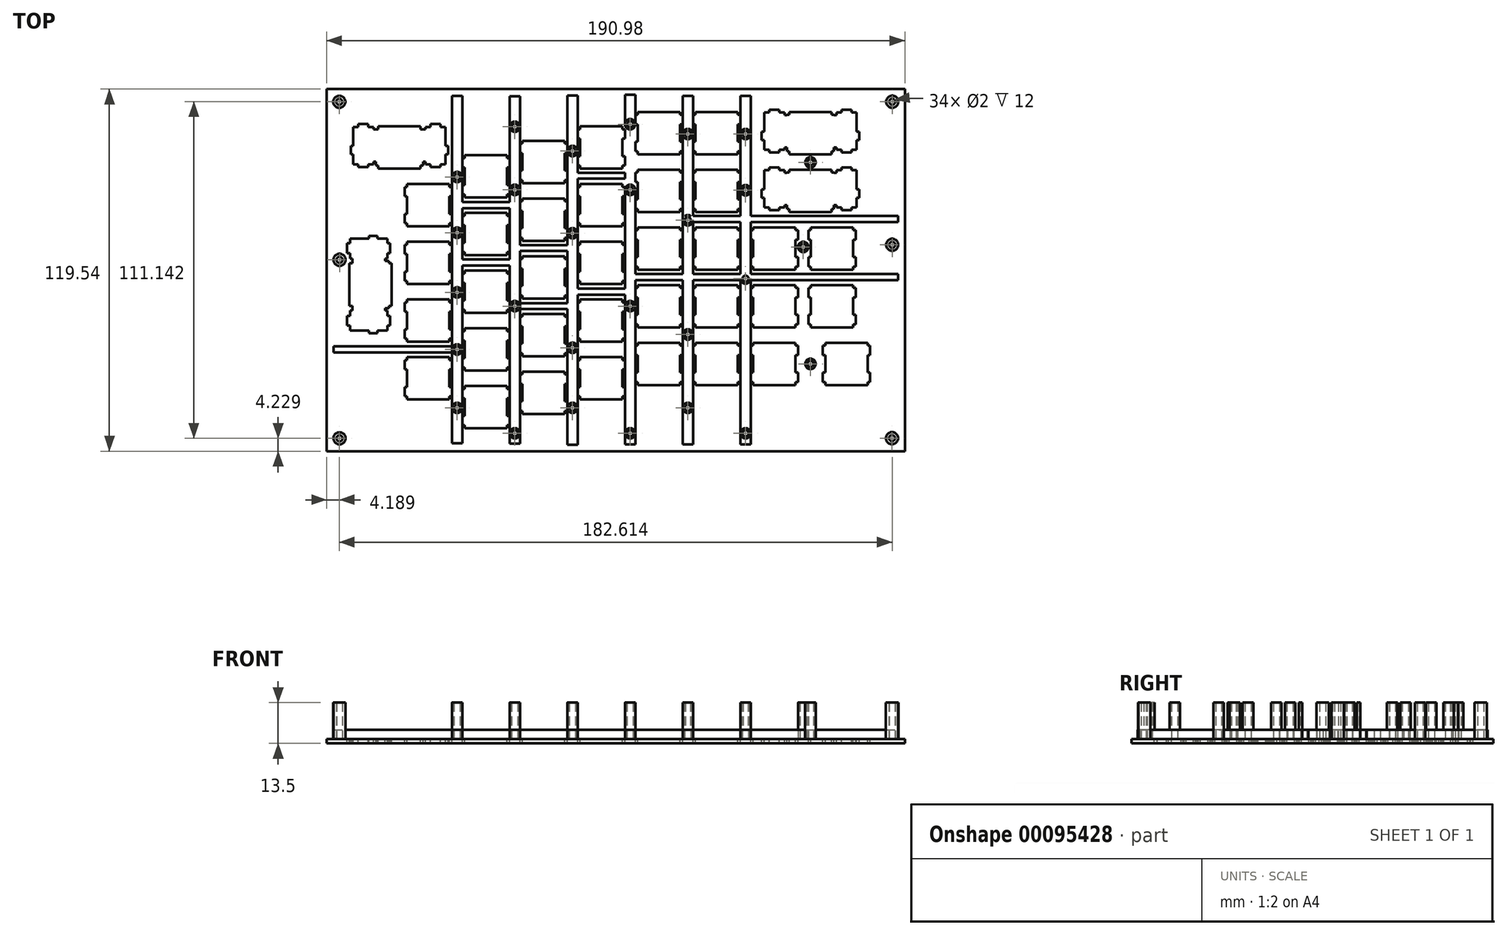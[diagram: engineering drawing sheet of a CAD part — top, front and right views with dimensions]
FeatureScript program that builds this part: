
annotation { "Feature Type Name" : "Feature", "Feature Type Description" : "" }
export const myFeature = defineFeature(function(context is Context, id is Id, definition is map)
    precondition{}
    {
        {
            var Q0;
            Q0=qCreatedBy(makeId("Top.planeOp"),FACE);
            var sketch = newSketch(context, id + "F0", { "sketchPlane" : qUnion([Q0])});
            skLineSegment(sketch, "E0", {"start": v(-95.49, 59.77) * mm, "end": v(95.49, 59.77) * mm});
            skLineSegment(sketch, "E1", {"start": v(95.49, 59.77) * mm, "end": v(95.49, -59.77) * mm});
            skLineSegment(sketch, "E2", {"start": v(95.49, -59.77) * mm, "end": v(-95.49, -59.77) * mm});
            skLineSegment(sketch, "E3", {"start": v(-95.49, -59.77) * mm, "end": v(-95.49, 59.77) * mm});
            skLineSegment(sketch, "E4", {"start": v(-74.96, -2.24) * mm, "end": v(-74.96, -3.04) * mm});
            skLineSegment(sketch, "E5", {"start": v(-74.96, -3.04) * mm, "end": v(-76.23, -3.04) * mm});
            skLineSegment(sketch, "E6", {"start": v(-76.23, -3.04) * mm, "end": v(-76.23, -3.81) * mm});
            skLineSegment(sketch, "E7", {"start": v(-76.23, -3.81) * mm, "end": v(-75.43, -3.81) * mm});
            skLineSegment(sketch, "E8", {"start": v(-75.43, -3.81) * mm, "end": v(-75.43, -5.54) * mm});
            skLineSegment(sketch, "E9", {"start": v(-75.43, -5.54) * mm, "end": v(-74.51, -5.54) * mm});
            skLineSegment(sketch, "E10", {"start": v(-74.51, -5.54) * mm, "end": v(-74.51, -8.84) * mm});
            skLineSegment(sketch, "E11", {"start": v(-74.51, -8.84) * mm, "end": v(-75.43, -8.84) * mm});
            skLineSegment(sketch, "E12", {"start": v(-75.43, -8.84) * mm, "end": v(-75.43, -10.46) * mm});
            skLineSegment(sketch, "E13", {"start": v(-75.43, -10.46) * mm, "end": v(-78.66, -10.46) * mm});
            skLineSegment(sketch, "E14", {"start": v(-78.66, -10.46) * mm, "end": v(-78.66, -11.34) * mm});
            skLineSegment(sketch, "E15", {"start": v(-78.66, -11.34) * mm, "end": v(-81.46, -11.34) * mm});
            skLineSegment(sketch, "E16", {"start": v(-81.46, -11.34) * mm, "end": v(-81.46, -10.46) * mm});
            skLineSegment(sketch, "E17", {"start": v(-81.46, -10.46) * mm, "end": v(-87.73, -10.46) * mm});
            skLineSegment(sketch, "E18", {"start": v(-87.73, -10.46) * mm, "end": v(-87.73, -8.84) * mm});
            skLineSegment(sketch, "E19", {"start": v(-87.73, -8.84) * mm, "end": v(-88.71, -8.84) * mm});
            skLineSegment(sketch, "E20", {"start": v(-88.71, -8.84) * mm, "end": v(-88.71, -5.54) * mm});
            skLineSegment(sketch, "E21", {"start": v(-88.71, -5.54) * mm, "end": v(-87.73, -5.54) * mm});
            skLineSegment(sketch, "E22", {"start": v(-87.73, -5.54) * mm, "end": v(-87.73, -3.81) * mm});
            skLineSegment(sketch, "E23", {"start": v(-87.73, -3.81) * mm, "end": v(-86.93, -3.81) * mm});
            skLineSegment(sketch, "E24", {"start": v(-86.93, -3.81) * mm, "end": v(-86.93, -3.04) * mm});
            skLineSegment(sketch, "E25", {"start": v(-86.93, -3.04) * mm, "end": v(-86.96, -3.04) * mm});
            skLineSegment(sketch, "E26", {"start": v(-86.96, -3.04) * mm, "end": v(-86.96, -2.24) * mm});
            skLineSegment(sketch, "E27", {"start": v(-86.96, -2.24) * mm, "end": v(-87.96, -2.24) * mm});
            skLineSegment(sketch, "E28", {"start": v(-87.96, -2.24) * mm, "end": v(-87.96, 11.76) * mm});
            skLineSegment(sketch, "E29", {"start": v(-87.96, 11.76) * mm, "end": v(-86.96, 11.76) * mm});
            skLineSegment(sketch, "E30", {"start": v(-86.96, 11.76) * mm, "end": v(-86.96, 12.56) * mm});
            skLineSegment(sketch, "E31", {"start": v(-86.96, 12.56) * mm, "end": v(-86.93, 12.56) * mm});
            skLineSegment(sketch, "E32", {"start": v(-86.93, 12.56) * mm, "end": v(-86.93, 13.34) * mm});
            skLineSegment(sketch, "E33", {"start": v(-86.93, 13.34) * mm, "end": v(-87.73, 13.34) * mm});
            skLineSegment(sketch, "E34", {"start": v(-87.73, 13.34) * mm, "end": v(-87.73, 15.06) * mm});
            skLineSegment(sketch, "E35", {"start": v(-87.73, 15.06) * mm, "end": v(-88.71, 15.06) * mm});
            skLineSegment(sketch, "E36", {"start": v(-88.71, 15.06) * mm, "end": v(-88.71, 18.36) * mm});
            skLineSegment(sketch, "E37", {"start": v(-88.71, 18.36) * mm, "end": v(-87.73, 18.36) * mm});
            skLineSegment(sketch, "E38", {"start": v(-87.73, 18.36) * mm, "end": v(-87.73, 19.99) * mm});
            skLineSegment(sketch, "E39", {"start": v(-87.73, 19.99) * mm, "end": v(-81.46, 19.99) * mm});
            skLineSegment(sketch, "E40", {"start": v(-81.46, 19.99) * mm, "end": v(-81.46, 20.86) * mm});
            skLineSegment(sketch, "E41", {"start": v(-81.46, 20.86) * mm, "end": v(-78.66, 20.86) * mm});
            skLineSegment(sketch, "E42", {"start": v(-78.66, 20.86) * mm, "end": v(-78.66, 19.99) * mm});
            skLineSegment(sketch, "E43", {"start": v(-78.66, 19.99) * mm, "end": v(-75.43, 19.99) * mm});
            skLineSegment(sketch, "E44", {"start": v(-75.43, 19.99) * mm, "end": v(-75.43, 18.36) * mm});
            skLineSegment(sketch, "E45", {"start": v(-75.43, 18.36) * mm, "end": v(-74.51, 18.36) * mm});
            skLineSegment(sketch, "E46", {"start": v(-74.51, 18.36) * mm, "end": v(-74.51, 15.06) * mm});
            skLineSegment(sketch, "E47", {"start": v(-74.51, 15.06) * mm, "end": v(-75.43, 15.06) * mm});
            skLineSegment(sketch, "E48", {"start": v(-75.43, 15.06) * mm, "end": v(-75.43, 13.34) * mm});
            skLineSegment(sketch, "E49", {"start": v(-75.43, 13.34) * mm, "end": v(-76.23, 13.34) * mm});
            skLineSegment(sketch, "E50", {"start": v(-76.23, 13.34) * mm, "end": v(-76.23, 12.56) * mm});
            skLineSegment(sketch, "E51", {"start": v(-76.23, 12.56) * mm, "end": v(-74.96, 12.56) * mm});
            skLineSegment(sketch, "E52", {"start": v(-74.96, 12.56) * mm, "end": v(-74.96, 11.76) * mm});
            skLineSegment(sketch, "E53", {"start": v(-74.96, 11.76) * mm, "end": v(-73.96, 11.76) * mm});
            skLineSegment(sketch, "E54", {"start": v(-73.96, 11.76) * mm, "end": v(-73.96, -2.24) * mm});
            skLineSegment(sketch, "E55", {"start": v(-73.96, -2.24) * mm, "end": v(-74.96, -2.24) * mm});
            skLineSegment(sketch, "E56", {"start": v(-56.21, -40.98) * mm, "end": v(-56.21, -47.25) * mm});
            skLineSegment(sketch, "E57", {"start": v(-56.21, -47.25) * mm, "end": v(-57.84, -47.25) * mm});
            skLineSegment(sketch, "E58", {"start": v(-57.84, -47.25) * mm, "end": v(-57.84, -48.23) * mm});
            skLineSegment(sketch, "E59", {"start": v(-57.84, -48.23) * mm, "end": v(-61.14, -48.23) * mm});
            skLineSegment(sketch, "E60", {"start": v(-61.14, -48.23) * mm, "end": v(-61.14, -47.25) * mm});
            skLineSegment(sketch, "E61", {"start": v(-61.14, -47.25) * mm, "end": v(-62.86, -47.25) * mm});
            skLineSegment(sketch, "E62", {"start": v(-62.86, -47.25) * mm, "end": v(-62.86, -46.45) * mm});
            skLineSegment(sketch, "E63", {"start": v(-62.86, -46.45) * mm, "end": v(-63.64, -46.45) * mm});
            skLineSegment(sketch, "E64", {"start": v(-63.64, -46.45) * mm, "end": v(-63.64, -46.48) * mm});
            skLineSegment(sketch, "E65", {"start": v(-63.64, -46.48) * mm, "end": v(-64.44, -46.48) * mm});
            skLineSegment(sketch, "E66", {"start": v(-64.44, -46.48) * mm, "end": v(-64.44, -47.48) * mm});
            skLineSegment(sketch, "E67", {"start": v(-64.44, -47.48) * mm, "end": v(-78.44, -47.48) * mm});
            skLineSegment(sketch, "E68", {"start": v(-78.44, -47.48) * mm, "end": v(-78.44, -46.48) * mm});
            skLineSegment(sketch, "E69", {"start": v(-78.44, -46.48) * mm, "end": v(-79.24, -46.48) * mm});
            skLineSegment(sketch, "E70", {"start": v(-79.24, -46.48) * mm, "end": v(-79.24, -46.45) * mm});
            skLineSegment(sketch, "E71", {"start": v(-79.24, -46.45) * mm, "end": v(-80.01, -46.45) * mm});
            skLineSegment(sketch, "E72", {"start": v(-80.01, -46.45) * mm, "end": v(-80.01, -47.25) * mm});
            skLineSegment(sketch, "E73", {"start": v(-80.01, -47.25) * mm, "end": v(-81.74, -47.25) * mm});
            skLineSegment(sketch, "E74", {"start": v(-81.74, -47.25) * mm, "end": v(-81.74, -48.23) * mm});
            skLineSegment(sketch, "E75", {"start": v(-81.74, -48.23) * mm, "end": v(-85.04, -48.23) * mm});
            skLineSegment(sketch, "E76", {"start": v(-85.04, -48.23) * mm, "end": v(-85.04, -47.25) * mm});
            skLineSegment(sketch, "E77", {"start": v(-85.04, -47.25) * mm, "end": v(-86.66, -47.25) * mm});
            skLineSegment(sketch, "E78", {"start": v(-86.66, -47.25) * mm, "end": v(-86.66, -40.98) * mm});
            skLineSegment(sketch, "E79", {"start": v(-86.66, -40.98) * mm, "end": v(-87.54, -40.98) * mm});
            skLineSegment(sketch, "E80", {"start": v(-87.54, -40.98) * mm, "end": v(-87.54, -38.18) * mm});
            skLineSegment(sketch, "E81", {"start": v(-87.54, -38.18) * mm, "end": v(-86.66, -38.18) * mm});
            skLineSegment(sketch, "E82", {"start": v(-86.66, -38.18) * mm, "end": v(-86.66, -34.95) * mm});
            skLineSegment(sketch, "E83", {"start": v(-86.66, -34.95) * mm, "end": v(-85.04, -34.95) * mm});
            skLineSegment(sketch, "E84", {"start": v(-85.04, -34.95) * mm, "end": v(-85.04, -34.03) * mm});
            skLineSegment(sketch, "E85", {"start": v(-85.04, -34.03) * mm, "end": v(-81.74, -34.03) * mm});
            skLineSegment(sketch, "E86", {"start": v(-81.74, -34.03) * mm, "end": v(-81.74, -34.95) * mm});
            skLineSegment(sketch, "E87", {"start": v(-81.74, -34.95) * mm, "end": v(-80.01, -34.95) * mm});
            skLineSegment(sketch, "E88", {"start": v(-80.01, -34.95) * mm, "end": v(-80.01, -35.75) * mm});
            skLineSegment(sketch, "E89", {"start": v(-80.01, -35.75) * mm, "end": v(-79.24, -35.75) * mm});
            skLineSegment(sketch, "E90", {"start": v(-79.24, -35.75) * mm, "end": v(-79.24, -34.48) * mm});
            skLineSegment(sketch, "E91", {"start": v(-79.24, -34.48) * mm, "end": v(-78.44, -34.48) * mm});
            skLineSegment(sketch, "E92", {"start": v(-78.44, -34.48) * mm, "end": v(-78.44, -33.48) * mm});
            skLineSegment(sketch, "E93", {"start": v(-78.44, -33.48) * mm, "end": v(-64.44, -33.48) * mm});
            skLineSegment(sketch, "E94", {"start": v(-64.44, -33.48) * mm, "end": v(-64.44, -34.48) * mm});
            skLineSegment(sketch, "E95", {"start": v(-64.44, -34.48) * mm, "end": v(-63.64, -34.48) * mm});
            skLineSegment(sketch, "E96", {"start": v(-63.64, -34.48) * mm, "end": v(-63.64, -35.75) * mm});
            skLineSegment(sketch, "E97", {"start": v(-63.64, -35.75) * mm, "end": v(-62.86, -35.75) * mm});
            skLineSegment(sketch, "E98", {"start": v(-62.86, -35.75) * mm, "end": v(-62.86, -34.95) * mm});
            skLineSegment(sketch, "E99", {"start": v(-62.86, -34.95) * mm, "end": v(-61.14, -34.95) * mm});
            skLineSegment(sketch, "E100", {"start": v(-61.14, -34.95) * mm, "end": v(-61.14, -34.03) * mm});
            skLineSegment(sketch, "E101", {"start": v(-61.14, -34.03) * mm, "end": v(-57.84, -34.03) * mm});
            skLineSegment(sketch, "E102", {"start": v(-57.84, -34.03) * mm, "end": v(-57.84, -34.95) * mm});
            skLineSegment(sketch, "E103", {"start": v(-57.84, -34.95) * mm, "end": v(-56.21, -34.95) * mm});
            skLineSegment(sketch, "E104", {"start": v(-56.21, -34.95) * mm, "end": v(-56.21, -38.18) * mm});
            skLineSegment(sketch, "E105", {"start": v(-56.21, -38.18) * mm, "end": v(-55.34, -38.18) * mm});
            skLineSegment(sketch, "E106", {"start": v(-55.34, -38.18) * mm, "end": v(-55.34, -40.98) * mm});
            skLineSegment(sketch, "E107", {"start": v(-55.34, -40.98) * mm, "end": v(-56.21, -40.98) * mm});
            skLineSegment(sketch, "E108", {"start": v(-54.91, 29.72) * mm, "end": v(-54.91, 28.72) * mm});
            skLineSegment(sketch, "E109", {"start": v(-54.91, 28.72) * mm, "end": v(-68.91, 28.72) * mm});
            skLineSegment(sketch, "E110", {"start": v(-68.91, 28.72) * mm, "end": v(-68.91, 29.72) * mm});
            skLineSegment(sketch, "E111", {"start": v(-68.91, 29.72) * mm, "end": v(-69.71, 29.72) * mm});
            skLineSegment(sketch, "E112", {"start": v(-69.71, 29.72) * mm, "end": v(-69.71, 32.82) * mm});
            skLineSegment(sketch, "E113", {"start": v(-69.71, 32.82) * mm, "end": v(-68.91, 32.82) * mm});
            skLineSegment(sketch, "E114", {"start": v(-68.91, 32.82) * mm, "end": v(-68.91, 38.62) * mm});
            skLineSegment(sketch, "E115", {"start": v(-68.91, 38.62) * mm, "end": v(-69.71, 38.62) * mm});
            skLineSegment(sketch, "E116", {"start": v(-69.71, 38.62) * mm, "end": v(-69.71, 41.72) * mm});
            skLineSegment(sketch, "E117", {"start": v(-69.71, 41.72) * mm, "end": v(-68.91, 41.72) * mm});
            skLineSegment(sketch, "E118", {"start": v(-68.91, 41.72) * mm, "end": v(-68.91, 42.72) * mm});
            skLineSegment(sketch, "E119", {"start": v(-68.91, 42.72) * mm, "end": v(-54.91, 42.72) * mm});
            skLineSegment(sketch, "E120", {"start": v(-54.91, 42.72) * mm, "end": v(-54.91, 41.72) * mm});
            skLineSegment(sketch, "E121", {"start": v(-54.91, 41.72) * mm, "end": v(-54.11, 41.72) * mm});
            skLineSegment(sketch, "E122", {"start": v(-54.11, 41.72) * mm, "end": v(-54.11, 38.62) * mm});
            skLineSegment(sketch, "E123", {"start": v(-54.11, 38.62) * mm, "end": v(-54.91, 38.62) * mm});
            skLineSegment(sketch, "E124", {"start": v(-54.91, 38.62) * mm, "end": v(-54.91, 32.82) * mm});
            skLineSegment(sketch, "E125", {"start": v(-54.91, 32.82) * mm, "end": v(-54.11, 32.82) * mm});
            skLineSegment(sketch, "E126", {"start": v(-54.11, 32.82) * mm, "end": v(-54.11, 29.72) * mm});
            skLineSegment(sketch, "E127", {"start": v(-54.11, 29.72) * mm, "end": v(-54.91, 29.72) * mm});
            skLineSegment(sketch, "E128", {"start": v(-54.91, 10.67) * mm, "end": v(-54.91, 9.67) * mm});
            skLineSegment(sketch, "E129", {"start": v(-54.91, 9.67) * mm, "end": v(-68.91, 9.67) * mm});
            skLineSegment(sketch, "E130", {"start": v(-68.91, 9.67) * mm, "end": v(-68.91, 10.67) * mm});
            skLineSegment(sketch, "E131", {"start": v(-68.91, 10.67) * mm, "end": v(-69.71, 10.67) * mm});
            skLineSegment(sketch, "E132", {"start": v(-69.71, 10.67) * mm, "end": v(-69.71, 13.77) * mm});
            skLineSegment(sketch, "E133", {"start": v(-69.71, 13.77) * mm, "end": v(-68.91, 13.77) * mm});
            skLineSegment(sketch, "E134", {"start": v(-68.91, 13.77) * mm, "end": v(-68.91, 19.57) * mm});
            skLineSegment(sketch, "E135", {"start": v(-68.91, 19.57) * mm, "end": v(-69.71, 19.57) * mm});
            skLineSegment(sketch, "E136", {"start": v(-69.71, 19.57) * mm, "end": v(-69.71, 22.67) * mm});
            skLineSegment(sketch, "E137", {"start": v(-69.71, 22.67) * mm, "end": v(-68.91, 22.67) * mm});
            skLineSegment(sketch, "E138", {"start": v(-68.91, 22.67) * mm, "end": v(-68.91, 23.67) * mm});
            skLineSegment(sketch, "E139", {"start": v(-68.91, 23.67) * mm, "end": v(-54.91, 23.67) * mm});
            skLineSegment(sketch, "E140", {"start": v(-54.91, 23.67) * mm, "end": v(-54.91, 22.67) * mm});
            skLineSegment(sketch, "E141", {"start": v(-54.91, 22.67) * mm, "end": v(-54.11, 22.67) * mm});
            skLineSegment(sketch, "E142", {"start": v(-54.11, 22.67) * mm, "end": v(-54.11, 19.57) * mm});
            skLineSegment(sketch, "E143", {"start": v(-54.11, 19.57) * mm, "end": v(-54.91, 19.57) * mm});
            skLineSegment(sketch, "E144", {"start": v(-54.91, 19.57) * mm, "end": v(-54.91, 13.77) * mm});
            skLineSegment(sketch, "E145", {"start": v(-54.91, 13.77) * mm, "end": v(-54.11, 13.77) * mm});
            skLineSegment(sketch, "E146", {"start": v(-54.11, 13.77) * mm, "end": v(-54.11, 10.67) * mm});
            skLineSegment(sketch, "E147", {"start": v(-54.11, 10.67) * mm, "end": v(-54.91, 10.67) * mm});
            skLineSegment(sketch, "E148", {"start": v(-54.91, -8.38) * mm, "end": v(-54.91, -9.38) * mm});
            skLineSegment(sketch, "E149", {"start": v(-54.91, -9.38) * mm, "end": v(-68.91, -9.38) * mm});
            skLineSegment(sketch, "E150", {"start": v(-68.91, -9.38) * mm, "end": v(-68.91, -8.38) * mm});
            skLineSegment(sketch, "E151", {"start": v(-68.91, -8.38) * mm, "end": v(-69.71, -8.38) * mm});
            skLineSegment(sketch, "E152", {"start": v(-69.71, -8.38) * mm, "end": v(-69.71, -5.28) * mm});
            skLineSegment(sketch, "E153", {"start": v(-69.71, -5.28) * mm, "end": v(-68.91, -5.28) * mm});
            skLineSegment(sketch, "E154", {"start": v(-68.91, -5.28) * mm, "end": v(-68.91, 0.52) * mm});
            skLineSegment(sketch, "E155", {"start": v(-68.91, 0.52) * mm, "end": v(-69.71, 0.52) * mm});
            skLineSegment(sketch, "E156", {"start": v(-69.71, 0.52) * mm, "end": v(-69.71, 3.62) * mm});
            skLineSegment(sketch, "E157", {"start": v(-69.71, 3.62) * mm, "end": v(-68.91, 3.62) * mm});
            skLineSegment(sketch, "E158", {"start": v(-68.91, 3.62) * mm, "end": v(-68.91, 4.62) * mm});
            skLineSegment(sketch, "E159", {"start": v(-68.91, 4.62) * mm, "end": v(-54.91, 4.62) * mm});
            skLineSegment(sketch, "E160", {"start": v(-54.91, 4.62) * mm, "end": v(-54.91, 3.62) * mm});
            skLineSegment(sketch, "E161", {"start": v(-54.91, 3.62) * mm, "end": v(-54.11, 3.62) * mm});
            skLineSegment(sketch, "E162", {"start": v(-54.11, 3.62) * mm, "end": v(-54.11, 0.52) * mm});
            skLineSegment(sketch, "E163", {"start": v(-54.11, 0.52) * mm, "end": v(-54.91, 0.52) * mm});
            skLineSegment(sketch, "E164", {"start": v(-54.91, 0.52) * mm, "end": v(-54.91, -5.28) * mm});
            skLineSegment(sketch, "E165", {"start": v(-54.91, -5.28) * mm, "end": v(-54.11, -5.28) * mm});
            skLineSegment(sketch, "E166", {"start": v(-54.11, -5.28) * mm, "end": v(-54.11, -8.38) * mm});
            skLineSegment(sketch, "E167", {"start": v(-54.11, -8.38) * mm, "end": v(-54.91, -8.38) * mm});
            skLineSegment(sketch, "E168", {"start": v(-54.91, -27.43) * mm, "end": v(-54.91, -28.43) * mm});
            skLineSegment(sketch, "E169", {"start": v(-54.91, -28.43) * mm, "end": v(-68.91, -28.43) * mm});
            skLineSegment(sketch, "E170", {"start": v(-68.91, -28.43) * mm, "end": v(-68.91, -27.43) * mm});
            skLineSegment(sketch, "E171", {"start": v(-68.91, -27.43) * mm, "end": v(-69.71, -27.43) * mm});
            skLineSegment(sketch, "E172", {"start": v(-69.71, -27.43) * mm, "end": v(-69.71, -24.33) * mm});
            skLineSegment(sketch, "E173", {"start": v(-69.71, -24.33) * mm, "end": v(-68.91, -24.33) * mm});
            skLineSegment(sketch, "E174", {"start": v(-68.91, -24.33) * mm, "end": v(-68.91, -18.53) * mm});
            skLineSegment(sketch, "E175", {"start": v(-68.91, -18.53) * mm, "end": v(-69.71, -18.53) * mm});
            skLineSegment(sketch, "E176", {"start": v(-69.71, -18.53) * mm, "end": v(-69.71, -15.43) * mm});
            skLineSegment(sketch, "E177", {"start": v(-69.71, -15.43) * mm, "end": v(-68.91, -15.43) * mm});
            skLineSegment(sketch, "E178", {"start": v(-68.91, -15.43) * mm, "end": v(-68.91, -14.43) * mm});
            skLineSegment(sketch, "E179", {"start": v(-68.91, -14.43) * mm, "end": v(-54.91, -14.43) * mm});
            skLineSegment(sketch, "E180", {"start": v(-54.91, -14.43) * mm, "end": v(-54.91, -15.43) * mm});
            skLineSegment(sketch, "E181", {"start": v(-54.91, -15.43) * mm, "end": v(-54.11, -15.43) * mm});
            skLineSegment(sketch, "E182", {"start": v(-54.11, -15.43) * mm, "end": v(-54.11, -18.53) * mm});
            skLineSegment(sketch, "E183", {"start": v(-54.11, -18.53) * mm, "end": v(-54.91, -18.53) * mm});
            skLineSegment(sketch, "E184", {"start": v(-54.91, -18.53) * mm, "end": v(-54.91, -24.33) * mm});
            skLineSegment(sketch, "E185", {"start": v(-54.91, -24.33) * mm, "end": v(-54.11, -24.33) * mm});
            skLineSegment(sketch, "E186", {"start": v(-54.11, -24.33) * mm, "end": v(-54.11, -27.43) * mm});
            skLineSegment(sketch, "E187", {"start": v(-54.11, -27.43) * mm, "end": v(-54.91, -27.43) * mm});
            skLineSegment(sketch, "E188", {"start": v(-35.86, 39.24) * mm, "end": v(-35.86, 38.24) * mm});
            skLineSegment(sketch, "E189", {"start": v(-35.86, 38.24) * mm, "end": v(-49.86, 38.24) * mm});
            skLineSegment(sketch, "E190", {"start": v(-49.86, 38.24) * mm, "end": v(-49.86, 39.24) * mm});
            skLineSegment(sketch, "E191", {"start": v(-49.86, 39.24) * mm, "end": v(-50.66, 39.24) * mm});
            skLineSegment(sketch, "E192", {"start": v(-50.66, 39.24) * mm, "end": v(-50.66, 42.34) * mm});
            skLineSegment(sketch, "E193", {"start": v(-50.66, 42.34) * mm, "end": v(-49.86, 42.34) * mm});
            skLineSegment(sketch, "E194", {"start": v(-49.86, 42.34) * mm, "end": v(-49.86, 48.14) * mm});
            skLineSegment(sketch, "E195", {"start": v(-49.86, 48.14) * mm, "end": v(-50.66, 48.14) * mm});
            skLineSegment(sketch, "E196", {"start": v(-50.66, 48.14) * mm, "end": v(-50.66, 51.24) * mm});
            skLineSegment(sketch, "E197", {"start": v(-50.66, 51.24) * mm, "end": v(-49.86, 51.24) * mm});
            skLineSegment(sketch, "E198", {"start": v(-49.86, 51.24) * mm, "end": v(-49.86, 52.24) * mm});
            skLineSegment(sketch, "E199", {"start": v(-49.86, 52.24) * mm, "end": v(-35.86, 52.24) * mm});
            skLineSegment(sketch, "E200", {"start": v(-35.86, 52.24) * mm, "end": v(-35.86, 51.24) * mm});
            skLineSegment(sketch, "E201", {"start": v(-35.86, 51.24) * mm, "end": v(-35.06, 51.24) * mm});
            skLineSegment(sketch, "E202", {"start": v(-35.06, 51.24) * mm, "end": v(-35.06, 48.14) * mm});
            skLineSegment(sketch, "E203", {"start": v(-35.06, 48.14) * mm, "end": v(-35.86, 48.14) * mm});
            skLineSegment(sketch, "E204", {"start": v(-35.86, 48.14) * mm, "end": v(-35.86, 42.34) * mm});
            skLineSegment(sketch, "E205", {"start": v(-35.86, 42.34) * mm, "end": v(-35.06, 42.34) * mm});
            skLineSegment(sketch, "E206", {"start": v(-35.06, 42.34) * mm, "end": v(-35.06, 39.24) * mm});
            skLineSegment(sketch, "E207", {"start": v(-35.06, 39.24) * mm, "end": v(-35.86, 39.24) * mm});
            skLineSegment(sketch, "E208", {"start": v(-35.86, 20.2) * mm, "end": v(-35.86, 19.2) * mm});
            skLineSegment(sketch, "E209", {"start": v(-35.86, 19.2) * mm, "end": v(-49.86, 19.2) * mm});
            skLineSegment(sketch, "E210", {"start": v(-49.86, 19.2) * mm, "end": v(-49.86, 20.2) * mm});
            skLineSegment(sketch, "E211", {"start": v(-49.86, 20.2) * mm, "end": v(-50.66, 20.2) * mm});
            skLineSegment(sketch, "E212", {"start": v(-50.66, 20.2) * mm, "end": v(-50.66, 23.3) * mm});
            skLineSegment(sketch, "E213", {"start": v(-50.66, 23.3) * mm, "end": v(-49.86, 23.3) * mm});
            skLineSegment(sketch, "E214", {"start": v(-49.86, 23.3) * mm, "end": v(-49.86, 29.1) * mm});
            skLineSegment(sketch, "E215", {"start": v(-49.86, 29.1) * mm, "end": v(-50.66, 29.1) * mm});
            skLineSegment(sketch, "E216", {"start": v(-50.66, 29.1) * mm, "end": v(-50.66, 32.2) * mm});
            skLineSegment(sketch, "E217", {"start": v(-50.66, 32.2) * mm, "end": v(-49.86, 32.2) * mm});
            skLineSegment(sketch, "E218", {"start": v(-49.86, 32.2) * mm, "end": v(-49.86, 33.2) * mm});
            skLineSegment(sketch, "E219", {"start": v(-49.86, 33.2) * mm, "end": v(-35.86, 33.2) * mm});
            skLineSegment(sketch, "E220", {"start": v(-35.86, 33.2) * mm, "end": v(-35.86, 32.2) * mm});
            skLineSegment(sketch, "E221", {"start": v(-35.86, 32.2) * mm, "end": v(-35.06, 32.2) * mm});
            skLineSegment(sketch, "E222", {"start": v(-35.06, 32.2) * mm, "end": v(-35.06, 29.1) * mm});
            skLineSegment(sketch, "E223", {"start": v(-35.06, 29.1) * mm, "end": v(-35.86, 29.1) * mm});
            skLineSegment(sketch, "E224", {"start": v(-35.86, 29.1) * mm, "end": v(-35.86, 23.3) * mm});
            skLineSegment(sketch, "E225", {"start": v(-35.86, 23.3) * mm, "end": v(-35.06, 23.3) * mm});
            skLineSegment(sketch, "E226", {"start": v(-35.06, 23.3) * mm, "end": v(-35.06, 20.2) * mm});
            skLineSegment(sketch, "E227", {"start": v(-35.06, 20.2) * mm, "end": v(-35.86, 20.2) * mm});
            skLineSegment(sketch, "E228", {"start": v(-35.86, 1.14) * mm, "end": v(-35.86, 0.14) * mm});
            skLineSegment(sketch, "E229", {"start": v(-35.86, 0.14) * mm, "end": v(-49.86, 0.14) * mm});
            skLineSegment(sketch, "E230", {"start": v(-49.86, 0.14) * mm, "end": v(-49.86, 1.14) * mm});
            skLineSegment(sketch, "E231", {"start": v(-49.86, 1.14) * mm, "end": v(-50.66, 1.14) * mm});
            skLineSegment(sketch, "E232", {"start": v(-50.66, 1.14) * mm, "end": v(-50.66, 4.24) * mm});
            skLineSegment(sketch, "E233", {"start": v(-50.66, 4.24) * mm, "end": v(-49.86, 4.24) * mm});
            skLineSegment(sketch, "E234", {"start": v(-49.86, 4.24) * mm, "end": v(-49.86, 10.04) * mm});
            skLineSegment(sketch, "E235", {"start": v(-49.86, 10.04) * mm, "end": v(-50.66, 10.04) * mm});
            skLineSegment(sketch, "E236", {"start": v(-50.66, 10.04) * mm, "end": v(-50.66, 13.14) * mm});
            skLineSegment(sketch, "E237", {"start": v(-50.66, 13.14) * mm, "end": v(-49.86, 13.14) * mm});
            skLineSegment(sketch, "E238", {"start": v(-49.86, 13.14) * mm, "end": v(-49.86, 14.14) * mm});
            skLineSegment(sketch, "E239", {"start": v(-49.86, 14.14) * mm, "end": v(-35.86, 14.14) * mm});
            skLineSegment(sketch, "E240", {"start": v(-35.86, 14.14) * mm, "end": v(-35.86, 13.14) * mm});
            skLineSegment(sketch, "E241", {"start": v(-35.86, 13.14) * mm, "end": v(-35.06, 13.14) * mm});
            skLineSegment(sketch, "E242", {"start": v(-35.06, 13.14) * mm, "end": v(-35.06, 10.04) * mm});
            skLineSegment(sketch, "E243", {"start": v(-35.06, 10.04) * mm, "end": v(-35.86, 10.04) * mm});
            skLineSegment(sketch, "E244", {"start": v(-35.86, 10.04) * mm, "end": v(-35.86, 4.24) * mm});
            skLineSegment(sketch, "E245", {"start": v(-35.86, 4.24) * mm, "end": v(-35.06, 4.24) * mm});
            skLineSegment(sketch, "E246", {"start": v(-35.06, 4.24) * mm, "end": v(-35.06, 1.14) * mm});
            skLineSegment(sketch, "E247", {"start": v(-35.06, 1.14) * mm, "end": v(-35.86, 1.14) * mm});
            skLineSegment(sketch, "E248", {"start": v(-35.86, -17.9) * mm, "end": v(-35.86, -18.9) * mm});
            skLineSegment(sketch, "E249", {"start": v(-35.86, -18.9) * mm, "end": v(-49.86, -18.9) * mm});
            skLineSegment(sketch, "E250", {"start": v(-49.86, -18.9) * mm, "end": v(-49.86, -17.9) * mm});
            skLineSegment(sketch, "E251", {"start": v(-49.86, -17.9) * mm, "end": v(-50.66, -17.9) * mm});
            skLineSegment(sketch, "E252", {"start": v(-50.66, -17.9) * mm, "end": v(-50.66, -14.8) * mm});
            skLineSegment(sketch, "E253", {"start": v(-50.66, -14.8) * mm, "end": v(-49.86, -14.8) * mm});
            skLineSegment(sketch, "E254", {"start": v(-49.86, -14.8) * mm, "end": v(-49.86, -9) * mm});
            skLineSegment(sketch, "E255", {"start": v(-49.86, -9) * mm, "end": v(-50.66, -9) * mm});
            skLineSegment(sketch, "E256", {"start": v(-50.66, -9) * mm, "end": v(-50.66, -5.9) * mm});
            skLineSegment(sketch, "E257", {"start": v(-50.66, -5.9) * mm, "end": v(-49.86, -5.9) * mm});
            skLineSegment(sketch, "E258", {"start": v(-49.86, -5.9) * mm, "end": v(-49.86, -4.9) * mm});
            skLineSegment(sketch, "E259", {"start": v(-49.86, -4.9) * mm, "end": v(-35.86, -4.9) * mm});
            skLineSegment(sketch, "E260", {"start": v(-35.86, -4.9) * mm, "end": v(-35.86, -5.9) * mm});
            skLineSegment(sketch, "E261", {"start": v(-35.86, -5.9) * mm, "end": v(-35.06, -5.9) * mm});
            skLineSegment(sketch, "E262", {"start": v(-35.06, -5.9) * mm, "end": v(-35.06, -9) * mm});
            skLineSegment(sketch, "E263", {"start": v(-35.06, -9) * mm, "end": v(-35.86, -9) * mm});
            skLineSegment(sketch, "E264", {"start": v(-35.86, -9) * mm, "end": v(-35.86, -14.8) * mm});
            skLineSegment(sketch, "E265", {"start": v(-35.86, -14.8) * mm, "end": v(-35.06, -14.8) * mm});
            skLineSegment(sketch, "E266", {"start": v(-35.06, -14.8) * mm, "end": v(-35.06, -17.9) * mm});
            skLineSegment(sketch, "E267", {"start": v(-35.06, -17.9) * mm, "end": v(-35.86, -17.9) * mm});
            skLineSegment(sketch, "E268", {"start": v(-35.86, -36.96) * mm, "end": v(-35.86, -37.96) * mm});
            skLineSegment(sketch, "E269", {"start": v(-35.86, -37.96) * mm, "end": v(-49.86, -37.96) * mm});
            skLineSegment(sketch, "E270", {"start": v(-49.86, -37.96) * mm, "end": v(-49.86, -36.96) * mm});
            skLineSegment(sketch, "E271", {"start": v(-49.86, -36.96) * mm, "end": v(-50.66, -36.96) * mm});
            skLineSegment(sketch, "E272", {"start": v(-50.66, -36.96) * mm, "end": v(-50.66, -33.86) * mm});
            skLineSegment(sketch, "E273", {"start": v(-50.66, -33.86) * mm, "end": v(-49.86, -33.86) * mm});
            skLineSegment(sketch, "E274", {"start": v(-49.86, -33.86) * mm, "end": v(-49.86, -28.06) * mm});
            skLineSegment(sketch, "E275", {"start": v(-49.86, -28.06) * mm, "end": v(-50.66, -28.06) * mm});
            skLineSegment(sketch, "E276", {"start": v(-50.66, -28.06) * mm, "end": v(-50.66, -24.96) * mm});
            skLineSegment(sketch, "E277", {"start": v(-50.66, -24.96) * mm, "end": v(-49.86, -24.96) * mm});
            skLineSegment(sketch, "E278", {"start": v(-49.86, -24.96) * mm, "end": v(-49.86, -23.96) * mm});
            skLineSegment(sketch, "E279", {"start": v(-49.86, -23.96) * mm, "end": v(-35.86, -23.96) * mm});
            skLineSegment(sketch, "E280", {"start": v(-35.86, -23.96) * mm, "end": v(-35.86, -24.96) * mm});
            skLineSegment(sketch, "E281", {"start": v(-35.86, -24.96) * mm, "end": v(-35.06, -24.96) * mm});
            skLineSegment(sketch, "E282", {"start": v(-35.06, -24.96) * mm, "end": v(-35.06, -28.06) * mm});
            skLineSegment(sketch, "E283", {"start": v(-35.06, -28.06) * mm, "end": v(-35.86, -28.06) * mm});
            skLineSegment(sketch, "E284", {"start": v(-35.86, -28.06) * mm, "end": v(-35.86, -33.86) * mm});
            skLineSegment(sketch, "E285", {"start": v(-35.86, -33.86) * mm, "end": v(-35.06, -33.86) * mm});
            skLineSegment(sketch, "E286", {"start": v(-35.06, -33.86) * mm, "end": v(-35.06, -36.96) * mm});
            skLineSegment(sketch, "E287", {"start": v(-35.06, -36.96) * mm, "end": v(-35.86, -36.96) * mm});
            skLineSegment(sketch, "E288", {"start": v(-16.81, 34.48) * mm, "end": v(-16.81, 33.48) * mm});
            skLineSegment(sketch, "E289", {"start": v(-16.81, 33.48) * mm, "end": v(-30.81, 33.48) * mm});
            skLineSegment(sketch, "E290", {"start": v(-30.81, 33.48) * mm, "end": v(-30.81, 34.48) * mm});
            skLineSegment(sketch, "E291", {"start": v(-30.81, 34.48) * mm, "end": v(-31.61, 34.48) * mm});
            skLineSegment(sketch, "E292", {"start": v(-31.61, 34.48) * mm, "end": v(-31.61, 37.58) * mm});
            skLineSegment(sketch, "E293", {"start": v(-31.61, 37.58) * mm, "end": v(-30.81, 37.58) * mm});
            skLineSegment(sketch, "E294", {"start": v(-30.81, 37.58) * mm, "end": v(-30.81, 43.38) * mm});
            skLineSegment(sketch, "E295", {"start": v(-30.81, 43.38) * mm, "end": v(-31.61, 43.38) * mm});
            skLineSegment(sketch, "E296", {"start": v(-31.61, 43.38) * mm, "end": v(-31.61, 46.48) * mm});
            skLineSegment(sketch, "E297", {"start": v(-31.61, 46.48) * mm, "end": v(-30.81, 46.48) * mm});
            skLineSegment(sketch, "E298", {"start": v(-30.81, 46.48) * mm, "end": v(-30.81, 47.48) * mm});
            skLineSegment(sketch, "E299", {"start": v(-30.81, 47.48) * mm, "end": v(-16.81, 47.48) * mm});
            skLineSegment(sketch, "E300", {"start": v(-16.81, 47.48) * mm, "end": v(-16.81, 46.48) * mm});
            skLineSegment(sketch, "E301", {"start": v(-16.81, 46.48) * mm, "end": v(-16.01, 46.48) * mm});
            skLineSegment(sketch, "E302", {"start": v(-16.01, 46.48) * mm, "end": v(-16.01, 43.38) * mm});
            skLineSegment(sketch, "E303", {"start": v(-16.01, 43.38) * mm, "end": v(-16.81, 43.38) * mm});
            skLineSegment(sketch, "E304", {"start": v(-16.81, 43.38) * mm, "end": v(-16.81, 37.58) * mm});
            skLineSegment(sketch, "E305", {"start": v(-16.81, 37.58) * mm, "end": v(-16.01, 37.58) * mm});
            skLineSegment(sketch, "E306", {"start": v(-16.01, 37.58) * mm, "end": v(-16.01, 34.48) * mm});
            skLineSegment(sketch, "E307", {"start": v(-16.01, 34.48) * mm, "end": v(-16.81, 34.48) * mm});
            skLineSegment(sketch, "E308", {"start": v(-16.81, 15.43) * mm, "end": v(-16.81, 14.43) * mm});
            skLineSegment(sketch, "E309", {"start": v(-16.81, 14.43) * mm, "end": v(-30.81, 14.43) * mm});
            skLineSegment(sketch, "E310", {"start": v(-30.81, 14.43) * mm, "end": v(-30.81, 15.43) * mm});
            skLineSegment(sketch, "E311", {"start": v(-30.81, 15.43) * mm, "end": v(-31.61, 15.43) * mm});
            skLineSegment(sketch, "E312", {"start": v(-31.61, 15.43) * mm, "end": v(-31.61, 18.53) * mm});
            skLineSegment(sketch, "E313", {"start": v(-31.61, 18.53) * mm, "end": v(-30.81, 18.53) * mm});
            skLineSegment(sketch, "E314", {"start": v(-30.81, 18.53) * mm, "end": v(-30.81, 24.33) * mm});
            skLineSegment(sketch, "E315", {"start": v(-30.81, 24.33) * mm, "end": v(-31.61, 24.33) * mm});
            skLineSegment(sketch, "E316", {"start": v(-31.61, 24.33) * mm, "end": v(-31.61, 27.43) * mm});
            skLineSegment(sketch, "E317", {"start": v(-31.61, 27.43) * mm, "end": v(-30.81, 27.43) * mm});
            skLineSegment(sketch, "E318", {"start": v(-30.81, 27.43) * mm, "end": v(-30.81, 28.43) * mm});
            skLineSegment(sketch, "E319", {"start": v(-30.81, 28.43) * mm, "end": v(-16.81, 28.43) * mm});
            skLineSegment(sketch, "E320", {"start": v(-16.81, 28.43) * mm, "end": v(-16.81, 27.43) * mm});
            skLineSegment(sketch, "E321", {"start": v(-16.81, 27.43) * mm, "end": v(-16.01, 27.43) * mm});
            skLineSegment(sketch, "E322", {"start": v(-16.01, 27.43) * mm, "end": v(-16.01, 24.33) * mm});
            skLineSegment(sketch, "E323", {"start": v(-16.01, 24.33) * mm, "end": v(-16.81, 24.33) * mm});
            skLineSegment(sketch, "E324", {"start": v(-16.81, 24.33) * mm, "end": v(-16.81, 18.53) * mm});
            skLineSegment(sketch, "E325", {"start": v(-16.81, 18.53) * mm, "end": v(-16.01, 18.53) * mm});
            skLineSegment(sketch, "E326", {"start": v(-16.01, 18.53) * mm, "end": v(-16.01, 15.43) * mm});
            skLineSegment(sketch, "E327", {"start": v(-16.01, 15.43) * mm, "end": v(-16.81, 15.43) * mm});
            skLineSegment(sketch, "E328", {"start": v(-16.81, -3.62) * mm, "end": v(-16.81, -4.62) * mm});
            skLineSegment(sketch, "E329", {"start": v(-16.81, -4.62) * mm, "end": v(-30.81, -4.62) * mm});
            skLineSegment(sketch, "E330", {"start": v(-30.81, -4.62) * mm, "end": v(-30.81, -3.62) * mm});
            skLineSegment(sketch, "E331", {"start": v(-30.81, -3.62) * mm, "end": v(-31.61, -3.62) * mm});
            skLineSegment(sketch, "E332", {"start": v(-31.61, -3.62) * mm, "end": v(-31.61, -0.52) * mm});
            skLineSegment(sketch, "E333", {"start": v(-31.61, -0.52) * mm, "end": v(-30.81, -0.52) * mm});
            skLineSegment(sketch, "E334", {"start": v(-30.81, -0.52) * mm, "end": v(-30.81, 5.28) * mm});
            skLineSegment(sketch, "E335", {"start": v(-30.81, 5.28) * mm, "end": v(-31.61, 5.28) * mm});
            skLineSegment(sketch, "E336", {"start": v(-31.61, 5.28) * mm, "end": v(-31.61, 8.38) * mm});
            skLineSegment(sketch, "E337", {"start": v(-31.61, 8.38) * mm, "end": v(-30.81, 8.38) * mm});
            skLineSegment(sketch, "E338", {"start": v(-30.81, 8.38) * mm, "end": v(-30.81, 9.38) * mm});
            skLineSegment(sketch, "E339", {"start": v(-30.81, 9.38) * mm, "end": v(-16.81, 9.38) * mm});
            skLineSegment(sketch, "E340", {"start": v(-16.81, 9.38) * mm, "end": v(-16.81, 8.38) * mm});
            skLineSegment(sketch, "E341", {"start": v(-16.81, 8.38) * mm, "end": v(-16.01, 8.38) * mm});
            skLineSegment(sketch, "E342", {"start": v(-16.01, 8.38) * mm, "end": v(-16.01, 5.28) * mm});
            skLineSegment(sketch, "E343", {"start": v(-16.01, 5.28) * mm, "end": v(-16.81, 5.28) * mm});
            skLineSegment(sketch, "E344", {"start": v(-16.81, 5.28) * mm, "end": v(-16.81, -0.52) * mm});
            skLineSegment(sketch, "E345", {"start": v(-16.81, -0.52) * mm, "end": v(-16.01, -0.52) * mm});
            skLineSegment(sketch, "E346", {"start": v(-16.01, -0.52) * mm, "end": v(-16.01, -3.62) * mm});
            skLineSegment(sketch, "E347", {"start": v(-16.01, -3.62) * mm, "end": v(-16.81, -3.62) * mm});
            skLineSegment(sketch, "E348", {"start": v(-16.81, -22.67) * mm, "end": v(-16.81, -23.67) * mm});
            skLineSegment(sketch, "E349", {"start": v(-16.81, -23.67) * mm, "end": v(-30.81, -23.67) * mm});
            skLineSegment(sketch, "E350", {"start": v(-30.81, -23.67) * mm, "end": v(-30.81, -22.67) * mm});
            skLineSegment(sketch, "E351", {"start": v(-30.81, -22.67) * mm, "end": v(-31.61, -22.67) * mm});
            skLineSegment(sketch, "E352", {"start": v(-31.61, -22.67) * mm, "end": v(-31.61, -19.57) * mm});
            skLineSegment(sketch, "E353", {"start": v(-31.61, -19.57) * mm, "end": v(-30.81, -19.57) * mm});
            skLineSegment(sketch, "E354", {"start": v(-30.81, -19.57) * mm, "end": v(-30.81, -13.77) * mm});
            skLineSegment(sketch, "E355", {"start": v(-30.81, -13.77) * mm, "end": v(-31.61, -13.77) * mm});
            skLineSegment(sketch, "E356", {"start": v(-31.61, -13.77) * mm, "end": v(-31.61, -10.67) * mm});
            skLineSegment(sketch, "E357", {"start": v(-31.61, -10.67) * mm, "end": v(-30.81, -10.67) * mm});
            skLineSegment(sketch, "E358", {"start": v(-30.81, -10.67) * mm, "end": v(-30.81, -9.67) * mm});
            skLineSegment(sketch, "E359", {"start": v(-30.81, -9.67) * mm, "end": v(-16.81, -9.67) * mm});
            skLineSegment(sketch, "E360", {"start": v(-16.81, -9.67) * mm, "end": v(-16.81, -10.67) * mm});
            skLineSegment(sketch, "E361", {"start": v(-16.81, -10.67) * mm, "end": v(-16.01, -10.67) * mm});
            skLineSegment(sketch, "E362", {"start": v(-16.01, -10.67) * mm, "end": v(-16.01, -13.77) * mm});
            skLineSegment(sketch, "E363", {"start": v(-16.01, -13.77) * mm, "end": v(-16.81, -13.77) * mm});
            skLineSegment(sketch, "E364", {"start": v(-16.81, -13.77) * mm, "end": v(-16.81, -19.57) * mm});
            skLineSegment(sketch, "E365", {"start": v(-16.81, -19.57) * mm, "end": v(-16.01, -19.57) * mm});
            skLineSegment(sketch, "E366", {"start": v(-16.01, -19.57) * mm, "end": v(-16.01, -22.67) * mm});
            skLineSegment(sketch, "E367", {"start": v(-16.01, -22.67) * mm, "end": v(-16.81, -22.67) * mm});
            skLineSegment(sketch, "E368", {"start": v(-16.81, -41.72) * mm, "end": v(-16.81, -42.72) * mm});
            skLineSegment(sketch, "E369", {"start": v(-16.81, -42.72) * mm, "end": v(-30.81, -42.72) * mm});
            skLineSegment(sketch, "E370", {"start": v(-30.81, -42.72) * mm, "end": v(-30.81, -41.72) * mm});
            skLineSegment(sketch, "E371", {"start": v(-30.81, -41.72) * mm, "end": v(-31.61, -41.72) * mm});
            skLineSegment(sketch, "E372", {"start": v(-31.61, -41.72) * mm, "end": v(-31.61, -38.62) * mm});
            skLineSegment(sketch, "E373", {"start": v(-31.61, -38.62) * mm, "end": v(-30.81, -38.62) * mm});
            skLineSegment(sketch, "E374", {"start": v(-30.81, -38.62) * mm, "end": v(-30.81, -32.82) * mm});
            skLineSegment(sketch, "E375", {"start": v(-30.81, -32.82) * mm, "end": v(-31.61, -32.82) * mm});
            skLineSegment(sketch, "E376", {"start": v(-31.61, -32.82) * mm, "end": v(-31.61, -29.72) * mm});
            skLineSegment(sketch, "E377", {"start": v(-31.61, -29.72) * mm, "end": v(-30.81, -29.72) * mm});
            skLineSegment(sketch, "E378", {"start": v(-30.81, -29.72) * mm, "end": v(-30.81, -28.72) * mm});
            skLineSegment(sketch, "E379", {"start": v(-30.81, -28.72) * mm, "end": v(-16.81, -28.72) * mm});
            skLineSegment(sketch, "E380", {"start": v(-16.81, -28.72) * mm, "end": v(-16.81, -29.72) * mm});
            skLineSegment(sketch, "E381", {"start": v(-16.81, -29.72) * mm, "end": v(-16.01, -29.72) * mm});
            skLineSegment(sketch, "E382", {"start": v(-16.01, -29.72) * mm, "end": v(-16.01, -32.82) * mm});
            skLineSegment(sketch, "E383", {"start": v(-16.01, -32.82) * mm, "end": v(-16.81, -32.82) * mm});
            skLineSegment(sketch, "E384", {"start": v(-16.81, -32.82) * mm, "end": v(-16.81, -38.62) * mm});
            skLineSegment(sketch, "E385", {"start": v(-16.81, -38.62) * mm, "end": v(-16.01, -38.62) * mm});
            skLineSegment(sketch, "E386", {"start": v(-16.01, -38.62) * mm, "end": v(-16.01, -41.72) * mm});
            skLineSegment(sketch, "E387", {"start": v(-16.01, -41.72) * mm, "end": v(-16.81, -41.72) * mm});
            skLineSegment(sketch, "E388", {"start": v(2.24, 29.72) * mm, "end": v(2.24, 28.72) * mm});
            skLineSegment(sketch, "E389", {"start": v(2.24, 28.72) * mm, "end": v(-11.76, 28.72) * mm});
            skLineSegment(sketch, "E390", {"start": v(-11.76, 28.72) * mm, "end": v(-11.76, 29.72) * mm});
            skLineSegment(sketch, "E391", {"start": v(-11.76, 29.72) * mm, "end": v(-12.56, 29.72) * mm});
            skLineSegment(sketch, "E392", {"start": v(-12.56, 29.72) * mm, "end": v(-12.56, 32.82) * mm});
            skLineSegment(sketch, "E393", {"start": v(-12.56, 32.82) * mm, "end": v(-11.76, 32.82) * mm});
            skLineSegment(sketch, "E394", {"start": v(-11.76, 32.82) * mm, "end": v(-11.76, 38.62) * mm});
            skLineSegment(sketch, "E395", {"start": v(-11.76, 38.62) * mm, "end": v(-12.56, 38.62) * mm});
            skLineSegment(sketch, "E396", {"start": v(-12.56, 38.62) * mm, "end": v(-12.56, 41.72) * mm});
            skLineSegment(sketch, "E397", {"start": v(-12.56, 41.72) * mm, "end": v(-11.76, 41.72) * mm});
            skLineSegment(sketch, "E398", {"start": v(-11.76, 41.72) * mm, "end": v(-11.76, 42.72) * mm});
            skLineSegment(sketch, "E399", {"start": v(-11.76, 42.72) * mm, "end": v(2.24, 42.72) * mm});
            skLineSegment(sketch, "E400", {"start": v(2.24, 42.72) * mm, "end": v(2.24, 41.72) * mm});
            skLineSegment(sketch, "E401", {"start": v(2.24, 41.72) * mm, "end": v(3.04, 41.72) * mm});
            skLineSegment(sketch, "E402", {"start": v(3.04, 41.72) * mm, "end": v(3.04, 38.62) * mm});
            skLineSegment(sketch, "E403", {"start": v(3.04, 38.62) * mm, "end": v(2.24, 38.62) * mm});
            skLineSegment(sketch, "E404", {"start": v(2.24, 38.62) * mm, "end": v(2.24, 32.82) * mm});
            skLineSegment(sketch, "E405", {"start": v(2.24, 32.82) * mm, "end": v(3.04, 32.82) * mm});
            skLineSegment(sketch, "E406", {"start": v(3.04, 32.82) * mm, "end": v(3.04, 29.72) * mm});
            skLineSegment(sketch, "E407", {"start": v(3.04, 29.72) * mm, "end": v(2.24, 29.72) * mm});
            skLineSegment(sketch, "E408", {"start": v(2.24, 10.67) * mm, "end": v(2.24, 9.67) * mm});
            skLineSegment(sketch, "E409", {"start": v(2.24, 9.67) * mm, "end": v(-11.76, 9.67) * mm});
            skLineSegment(sketch, "E410", {"start": v(-11.76, 9.67) * mm, "end": v(-11.76, 10.67) * mm});
            skLineSegment(sketch, "E411", {"start": v(-11.76, 10.67) * mm, "end": v(-12.56, 10.67) * mm});
            skLineSegment(sketch, "E412", {"start": v(-12.56, 10.67) * mm, "end": v(-12.56, 13.77) * mm});
            skLineSegment(sketch, "E413", {"start": v(-12.56, 13.77) * mm, "end": v(-11.76, 13.77) * mm});
            skLineSegment(sketch, "E414", {"start": v(-11.76, 13.77) * mm, "end": v(-11.76, 19.57) * mm});
            skLineSegment(sketch, "E415", {"start": v(-11.76, 19.57) * mm, "end": v(-12.56, 19.57) * mm});
            skLineSegment(sketch, "E416", {"start": v(-12.56, 19.57) * mm, "end": v(-12.56, 22.67) * mm});
            skLineSegment(sketch, "E417", {"start": v(-12.56, 22.67) * mm, "end": v(-11.76, 22.67) * mm});
            skLineSegment(sketch, "E418", {"start": v(-11.76, 22.67) * mm, "end": v(-11.76, 23.67) * mm});
            skLineSegment(sketch, "E419", {"start": v(-11.76, 23.67) * mm, "end": v(2.24, 23.67) * mm});
            skLineSegment(sketch, "E420", {"start": v(2.24, 23.67) * mm, "end": v(2.24, 22.67) * mm});
            skLineSegment(sketch, "E421", {"start": v(2.24, 22.67) * mm, "end": v(3.04, 22.67) * mm});
            skLineSegment(sketch, "E422", {"start": v(3.04, 22.67) * mm, "end": v(3.04, 19.57) * mm});
            skLineSegment(sketch, "E423", {"start": v(3.04, 19.57) * mm, "end": v(2.24, 19.57) * mm});
            skLineSegment(sketch, "E424", {"start": v(2.24, 19.57) * mm, "end": v(2.24, 13.77) * mm});
            skLineSegment(sketch, "E425", {"start": v(2.24, 13.77) * mm, "end": v(3.04, 13.77) * mm});
            skLineSegment(sketch, "E426", {"start": v(3.04, 13.77) * mm, "end": v(3.04, 10.67) * mm});
            skLineSegment(sketch, "E427", {"start": v(3.04, 10.67) * mm, "end": v(2.24, 10.67) * mm});
            skLineSegment(sketch, "E428", {"start": v(2.24, -8.38) * mm, "end": v(2.24, -9.38) * mm});
            skLineSegment(sketch, "E429", {"start": v(2.24, -9.38) * mm, "end": v(-11.76, -9.38) * mm});
            skLineSegment(sketch, "E430", {"start": v(-11.76, -9.38) * mm, "end": v(-11.76, -8.38) * mm});
            skLineSegment(sketch, "E431", {"start": v(-11.76, -8.38) * mm, "end": v(-12.56, -8.38) * mm});
            skLineSegment(sketch, "E432", {"start": v(-12.56, -8.38) * mm, "end": v(-12.56, -5.28) * mm});
            skLineSegment(sketch, "E433", {"start": v(-12.56, -5.28) * mm, "end": v(-11.76, -5.28) * mm});
            skLineSegment(sketch, "E434", {"start": v(-11.76, -5.28) * mm, "end": v(-11.76, 0.52) * mm});
            skLineSegment(sketch, "E435", {"start": v(-11.76, 0.52) * mm, "end": v(-12.56, 0.52) * mm});
            skLineSegment(sketch, "E436", {"start": v(-12.56, 0.52) * mm, "end": v(-12.56, 3.62) * mm});
            skLineSegment(sketch, "E437", {"start": v(-12.56, 3.62) * mm, "end": v(-11.76, 3.62) * mm});
            skLineSegment(sketch, "E438", {"start": v(-11.76, 3.62) * mm, "end": v(-11.76, 4.62) * mm});
            skLineSegment(sketch, "E439", {"start": v(-11.76, 4.62) * mm, "end": v(2.24, 4.62) * mm});
            skLineSegment(sketch, "E440", {"start": v(2.24, 4.62) * mm, "end": v(2.24, 3.62) * mm});
            skLineSegment(sketch, "E441", {"start": v(2.24, 3.62) * mm, "end": v(3.04, 3.62) * mm});
            skLineSegment(sketch, "E442", {"start": v(3.04, 3.62) * mm, "end": v(3.04, 0.52) * mm});
            skLineSegment(sketch, "E443", {"start": v(3.04, 0.52) * mm, "end": v(2.24, 0.52) * mm});
            skLineSegment(sketch, "E444", {"start": v(2.24, 0.52) * mm, "end": v(2.24, -5.28) * mm});
            skLineSegment(sketch, "E445", {"start": v(2.24, -5.28) * mm, "end": v(3.04, -5.28) * mm});
            skLineSegment(sketch, "E446", {"start": v(3.04, -5.28) * mm, "end": v(3.04, -8.38) * mm});
            skLineSegment(sketch, "E447", {"start": v(3.04, -8.38) * mm, "end": v(2.24, -8.38) * mm});
            skLineSegment(sketch, "E448", {"start": v(2.24, -27.43) * mm, "end": v(2.24, -28.43) * mm});
            skLineSegment(sketch, "E449", {"start": v(2.24, -28.43) * mm, "end": v(-11.76, -28.43) * mm});
            skLineSegment(sketch, "E450", {"start": v(-11.76, -28.43) * mm, "end": v(-11.76, -27.43) * mm});
            skLineSegment(sketch, "E451", {"start": v(-11.76, -27.43) * mm, "end": v(-12.56, -27.43) * mm});
            skLineSegment(sketch, "E452", {"start": v(-12.56, -27.43) * mm, "end": v(-12.56, -24.33) * mm});
            skLineSegment(sketch, "E453", {"start": v(-12.56, -24.33) * mm, "end": v(-11.76, -24.33) * mm});
            skLineSegment(sketch, "E454", {"start": v(-11.76, -24.33) * mm, "end": v(-11.76, -18.53) * mm});
            skLineSegment(sketch, "E455", {"start": v(-11.76, -18.53) * mm, "end": v(-12.56, -18.53) * mm});
            skLineSegment(sketch, "E456", {"start": v(-12.56, -18.53) * mm, "end": v(-12.56, -15.43) * mm});
            skLineSegment(sketch, "E457", {"start": v(-12.56, -15.43) * mm, "end": v(-11.76, -15.43) * mm});
            skLineSegment(sketch, "E458", {"start": v(-11.76, -15.43) * mm, "end": v(-11.76, -14.43) * mm});
            skLineSegment(sketch, "E459", {"start": v(-11.76, -14.43) * mm, "end": v(2.24, -14.43) * mm});
            skLineSegment(sketch, "E460", {"start": v(2.24, -14.43) * mm, "end": v(2.24, -15.43) * mm});
            skLineSegment(sketch, "E461", {"start": v(2.24, -15.43) * mm, "end": v(3.04, -15.43) * mm});
            skLineSegment(sketch, "E462", {"start": v(3.04, -15.43) * mm, "end": v(3.04, -18.53) * mm});
            skLineSegment(sketch, "E463", {"start": v(3.04, -18.53) * mm, "end": v(2.24, -18.53) * mm});
            skLineSegment(sketch, "E464", {"start": v(2.24, -18.53) * mm, "end": v(2.24, -24.33) * mm});
            skLineSegment(sketch, "E465", {"start": v(2.24, -24.33) * mm, "end": v(3.04, -24.33) * mm});
            skLineSegment(sketch, "E466", {"start": v(3.04, -24.33) * mm, "end": v(3.04, -27.43) * mm});
            skLineSegment(sketch, "E467", {"start": v(3.04, -27.43) * mm, "end": v(2.24, -27.43) * mm});
            skLineSegment(sketch, "E468", {"start": v(2.24, -46.48) * mm, "end": v(2.24, -47.48) * mm});
            skLineSegment(sketch, "E469", {"start": v(2.24, -47.48) * mm, "end": v(-11.76, -47.48) * mm});
            skLineSegment(sketch, "E470", {"start": v(-11.76, -47.48) * mm, "end": v(-11.76, -46.48) * mm});
            skLineSegment(sketch, "E471", {"start": v(-11.76, -46.48) * mm, "end": v(-12.56, -46.48) * mm});
            skLineSegment(sketch, "E472", {"start": v(-12.56, -46.48) * mm, "end": v(-12.56, -43.38) * mm});
            skLineSegment(sketch, "E473", {"start": v(-12.56, -43.38) * mm, "end": v(-11.76, -43.38) * mm});
            skLineSegment(sketch, "E474", {"start": v(-11.76, -43.38) * mm, "end": v(-11.76, -37.58) * mm});
            skLineSegment(sketch, "E475", {"start": v(-11.76, -37.58) * mm, "end": v(-12.56, -37.58) * mm});
            skLineSegment(sketch, "E476", {"start": v(-12.56, -37.58) * mm, "end": v(-12.56, -34.48) * mm});
            skLineSegment(sketch, "E477", {"start": v(-12.56, -34.48) * mm, "end": v(-11.76, -34.48) * mm});
            skLineSegment(sketch, "E478", {"start": v(-11.76, -34.48) * mm, "end": v(-11.76, -33.48) * mm});
            skLineSegment(sketch, "E479", {"start": v(-11.76, -33.48) * mm, "end": v(2.24, -33.48) * mm});
            skLineSegment(sketch, "E480", {"start": v(2.24, -33.48) * mm, "end": v(2.24, -34.48) * mm});
            skLineSegment(sketch, "E481", {"start": v(2.24, -34.48) * mm, "end": v(3.04, -34.48) * mm});
            skLineSegment(sketch, "E482", {"start": v(3.04, -34.48) * mm, "end": v(3.04, -37.58) * mm});
            skLineSegment(sketch, "E483", {"start": v(3.04, -37.58) * mm, "end": v(2.24, -37.58) * mm});
            skLineSegment(sketch, "E484", {"start": v(2.24, -37.58) * mm, "end": v(2.24, -43.38) * mm});
            skLineSegment(sketch, "E485", {"start": v(2.24, -43.38) * mm, "end": v(3.04, -43.38) * mm});
            skLineSegment(sketch, "E486", {"start": v(3.04, -43.38) * mm, "end": v(3.04, -46.48) * mm});
            skLineSegment(sketch, "E487", {"start": v(3.04, -46.48) * mm, "end": v(2.24, -46.48) * mm});
            skLineSegment(sketch, "E488", {"start": v(21.29, 24.96) * mm, "end": v(21.29, 23.96) * mm});
            skLineSegment(sketch, "E489", {"start": v(21.29, 23.96) * mm, "end": v(7.29, 23.96) * mm});
            skLineSegment(sketch, "E490", {"start": v(7.29, 23.96) * mm, "end": v(7.29, 24.96) * mm});
            skLineSegment(sketch, "E491", {"start": v(7.29, 24.96) * mm, "end": v(6.49, 24.96) * mm});
            skLineSegment(sketch, "E492", {"start": v(6.49, 24.96) * mm, "end": v(6.49, 28.06) * mm});
            skLineSegment(sketch, "E493", {"start": v(6.49, 28.06) * mm, "end": v(7.29, 28.06) * mm});
            skLineSegment(sketch, "E494", {"start": v(7.29, 28.06) * mm, "end": v(7.29, 33.86) * mm});
            skLineSegment(sketch, "E495", {"start": v(7.29, 33.86) * mm, "end": v(6.49, 33.86) * mm});
            skLineSegment(sketch, "E496", {"start": v(6.49, 33.86) * mm, "end": v(6.49, 36.96) * mm});
            skLineSegment(sketch, "E497", {"start": v(6.49, 36.96) * mm, "end": v(7.29, 36.96) * mm});
            skLineSegment(sketch, "E498", {"start": v(7.29, 36.96) * mm, "end": v(7.29, 37.96) * mm});
            skLineSegment(sketch, "E499", {"start": v(7.29, 37.96) * mm, "end": v(21.29, 37.96) * mm});
            skLineSegment(sketch, "E500", {"start": v(21.29, 37.96) * mm, "end": v(21.29, 36.96) * mm});
            skLineSegment(sketch, "E501", {"start": v(21.29, 36.96) * mm, "end": v(22.09, 36.96) * mm});
            skLineSegment(sketch, "E502", {"start": v(22.09, 36.96) * mm, "end": v(22.09, 33.86) * mm});
            skLineSegment(sketch, "E503", {"start": v(22.09, 33.86) * mm, "end": v(21.29, 33.86) * mm});
            skLineSegment(sketch, "E504", {"start": v(21.29, 33.86) * mm, "end": v(21.29, 28.06) * mm});
            skLineSegment(sketch, "E505", {"start": v(21.29, 28.06) * mm, "end": v(22.09, 28.06) * mm});
            skLineSegment(sketch, "E506", {"start": v(22.09, 28.06) * mm, "end": v(22.09, 24.96) * mm});
            skLineSegment(sketch, "E507", {"start": v(22.09, 24.96) * mm, "end": v(21.29, 24.96) * mm});
            skLineSegment(sketch, "E508", {"start": v(21.29, 5.9) * mm, "end": v(21.29, 4.9) * mm});
            skLineSegment(sketch, "E509", {"start": v(21.29, 4.9) * mm, "end": v(7.29, 4.9) * mm});
            skLineSegment(sketch, "E510", {"start": v(7.29, 4.9) * mm, "end": v(7.29, 5.9) * mm});
            skLineSegment(sketch, "E511", {"start": v(7.29, 5.9) * mm, "end": v(6.49, 5.9) * mm});
            skLineSegment(sketch, "E512", {"start": v(6.49, 5.9) * mm, "end": v(6.49, 9) * mm});
            skLineSegment(sketch, "E513", {"start": v(6.49, 9) * mm, "end": v(7.29, 9) * mm});
            skLineSegment(sketch, "E514", {"start": v(7.29, 9) * mm, "end": v(7.29, 14.8) * mm});
            skLineSegment(sketch, "E515", {"start": v(7.29, 14.8) * mm, "end": v(6.49, 14.8) * mm});
            skLineSegment(sketch, "E516", {"start": v(6.49, 14.8) * mm, "end": v(6.49, 17.9) * mm});
            skLineSegment(sketch, "E517", {"start": v(6.49, 17.9) * mm, "end": v(7.29, 17.9) * mm});
            skLineSegment(sketch, "E518", {"start": v(7.29, 17.9) * mm, "end": v(7.29, 18.9) * mm});
            skLineSegment(sketch, "E519", {"start": v(7.29, 18.9) * mm, "end": v(21.29, 18.9) * mm});
            skLineSegment(sketch, "E520", {"start": v(21.29, 18.9) * mm, "end": v(21.29, 17.9) * mm});
            skLineSegment(sketch, "E521", {"start": v(21.29, 17.9) * mm, "end": v(22.09, 17.9) * mm});
            skLineSegment(sketch, "E522", {"start": v(22.09, 17.9) * mm, "end": v(22.09, 14.8) * mm});
            skLineSegment(sketch, "E523", {"start": v(22.09, 14.8) * mm, "end": v(21.29, 14.8) * mm});
            skLineSegment(sketch, "E524", {"start": v(21.29, 14.8) * mm, "end": v(21.29, 9) * mm});
            skLineSegment(sketch, "E525", {"start": v(21.29, 9) * mm, "end": v(22.09, 9) * mm});
            skLineSegment(sketch, "E526", {"start": v(22.09, 9) * mm, "end": v(22.09, 5.9) * mm});
            skLineSegment(sketch, "E527", {"start": v(22.09, 5.9) * mm, "end": v(21.29, 5.9) * mm});
            skLineSegment(sketch, "E528", {"start": v(21.29, -13.14) * mm, "end": v(21.29, -14.14) * mm});
            skLineSegment(sketch, "E529", {"start": v(21.29, -14.14) * mm, "end": v(7.29, -14.14) * mm});
            skLineSegment(sketch, "E530", {"start": v(7.29, -14.14) * mm, "end": v(7.29, -13.14) * mm});
            skLineSegment(sketch, "E531", {"start": v(7.29, -13.14) * mm, "end": v(6.49, -13.14) * mm});
            skLineSegment(sketch, "E532", {"start": v(6.49, -13.14) * mm, "end": v(6.49, -10.04) * mm});
            skLineSegment(sketch, "E533", {"start": v(6.49, -10.04) * mm, "end": v(7.29, -10.04) * mm});
            skLineSegment(sketch, "E534", {"start": v(7.29, -10.04) * mm, "end": v(7.29, -4.24) * mm});
            skLineSegment(sketch, "E535", {"start": v(7.29, -4.24) * mm, "end": v(6.49, -4.24) * mm});
            skLineSegment(sketch, "E536", {"start": v(6.49, -4.24) * mm, "end": v(6.49, -1.14) * mm});
            skLineSegment(sketch, "E537", {"start": v(6.49, -1.14) * mm, "end": v(7.29, -1.14) * mm});
            skLineSegment(sketch, "E538", {"start": v(7.29, -1.14) * mm, "end": v(7.29, -0.14) * mm});
            skLineSegment(sketch, "E539", {"start": v(7.29, -0.14) * mm, "end": v(21.29, -0.14) * mm});
            skLineSegment(sketch, "E540", {"start": v(21.29, -0.14) * mm, "end": v(21.29, -1.14) * mm});
            skLineSegment(sketch, "E541", {"start": v(21.29, -1.14) * mm, "end": v(22.09, -1.14) * mm});
            skLineSegment(sketch, "E542", {"start": v(22.09, -1.14) * mm, "end": v(22.09, -4.24) * mm});
            skLineSegment(sketch, "E543", {"start": v(22.09, -4.24) * mm, "end": v(21.29, -4.24) * mm});
            skLineSegment(sketch, "E544", {"start": v(21.29, -4.24) * mm, "end": v(21.29, -10.04) * mm});
            skLineSegment(sketch, "E545", {"start": v(21.29, -10.04) * mm, "end": v(22.09, -10.04) * mm});
            skLineSegment(sketch, "E546", {"start": v(22.09, -10.04) * mm, "end": v(22.09, -13.14) * mm});
            skLineSegment(sketch, "E547", {"start": v(22.09, -13.14) * mm, "end": v(21.29, -13.14) * mm});
            skLineSegment(sketch, "E548", {"start": v(21.29, -32.2) * mm, "end": v(21.29, -33.2) * mm});
            skLineSegment(sketch, "E549", {"start": v(21.29, -33.2) * mm, "end": v(7.29, -33.2) * mm});
            skLineSegment(sketch, "E550", {"start": v(7.29, -33.2) * mm, "end": v(7.29, -32.2) * mm});
            skLineSegment(sketch, "E551", {"start": v(7.29, -32.2) * mm, "end": v(6.49, -32.2) * mm});
            skLineSegment(sketch, "E552", {"start": v(6.49, -32.2) * mm, "end": v(6.49, -29.1) * mm});
            skLineSegment(sketch, "E553", {"start": v(6.49, -29.1) * mm, "end": v(7.29, -29.1) * mm});
            skLineSegment(sketch, "E554", {"start": v(7.29, -29.1) * mm, "end": v(7.29, -23.3) * mm});
            skLineSegment(sketch, "E555", {"start": v(7.29, -23.3) * mm, "end": v(6.49, -23.3) * mm});
            skLineSegment(sketch, "E556", {"start": v(6.49, -23.3) * mm, "end": v(6.49, -20.2) * mm});
            skLineSegment(sketch, "E557", {"start": v(6.49, -20.2) * mm, "end": v(7.29, -20.2) * mm});
            skLineSegment(sketch, "E558", {"start": v(7.29, -20.2) * mm, "end": v(7.29, -19.2) * mm});
            skLineSegment(sketch, "E559", {"start": v(7.29, -19.2) * mm, "end": v(21.29, -19.2) * mm});
            skLineSegment(sketch, "E560", {"start": v(21.29, -19.2) * mm, "end": v(21.29, -20.2) * mm});
            skLineSegment(sketch, "E561", {"start": v(21.29, -20.2) * mm, "end": v(22.09, -20.2) * mm});
            skLineSegment(sketch, "E562", {"start": v(22.09, -20.2) * mm, "end": v(22.09, -23.3) * mm});
            skLineSegment(sketch, "E563", {"start": v(22.09, -23.3) * mm, "end": v(21.29, -23.3) * mm});
            skLineSegment(sketch, "E564", {"start": v(21.29, -23.3) * mm, "end": v(21.29, -29.1) * mm});
            skLineSegment(sketch, "E565", {"start": v(21.29, -29.1) * mm, "end": v(22.09, -29.1) * mm});
            skLineSegment(sketch, "E566", {"start": v(22.09, -29.1) * mm, "end": v(22.09, -32.2) * mm});
            skLineSegment(sketch, "E567", {"start": v(22.09, -32.2) * mm, "end": v(21.29, -32.2) * mm});
            skLineSegment(sketch, "E568", {"start": v(21.29, -51.24) * mm, "end": v(21.29, -52.24) * mm});
            skLineSegment(sketch, "E569", {"start": v(21.29, -52.24) * mm, "end": v(7.29, -52.24) * mm});
            skLineSegment(sketch, "E570", {"start": v(7.29, -52.24) * mm, "end": v(7.29, -51.24) * mm});
            skLineSegment(sketch, "E571", {"start": v(7.29, -51.24) * mm, "end": v(6.49, -51.24) * mm});
            skLineSegment(sketch, "E572", {"start": v(6.49, -51.24) * mm, "end": v(6.49, -48.14) * mm});
            skLineSegment(sketch, "E573", {"start": v(6.49, -48.14) * mm, "end": v(7.29, -48.14) * mm});
            skLineSegment(sketch, "E574", {"start": v(7.29, -48.14) * mm, "end": v(7.29, -42.34) * mm});
            skLineSegment(sketch, "E575", {"start": v(7.29, -42.34) * mm, "end": v(6.49, -42.34) * mm});
            skLineSegment(sketch, "E576", {"start": v(6.49, -42.34) * mm, "end": v(6.49, -39.24) * mm});
            skLineSegment(sketch, "E577", {"start": v(6.49, -39.24) * mm, "end": v(7.29, -39.24) * mm});
            skLineSegment(sketch, "E578", {"start": v(7.29, -39.24) * mm, "end": v(7.29, -38.24) * mm});
            skLineSegment(sketch, "E579", {"start": v(7.29, -38.24) * mm, "end": v(21.29, -38.24) * mm});
            skLineSegment(sketch, "E580", {"start": v(21.29, -38.24) * mm, "end": v(21.29, -39.24) * mm});
            skLineSegment(sketch, "E581", {"start": v(21.29, -39.24) * mm, "end": v(22.09, -39.24) * mm});
            skLineSegment(sketch, "E582", {"start": v(22.09, -39.24) * mm, "end": v(22.09, -42.34) * mm});
            skLineSegment(sketch, "E583", {"start": v(22.09, -42.34) * mm, "end": v(21.29, -42.34) * mm});
            skLineSegment(sketch, "E584", {"start": v(21.29, -42.34) * mm, "end": v(21.29, -48.14) * mm});
            skLineSegment(sketch, "E585", {"start": v(21.29, -48.14) * mm, "end": v(22.09, -48.14) * mm});
            skLineSegment(sketch, "E586", {"start": v(22.09, -48.14) * mm, "end": v(22.09, -51.24) * mm});
            skLineSegment(sketch, "E587", {"start": v(22.09, -51.24) * mm, "end": v(21.29, -51.24) * mm});
            skLineSegment(sketch, "E588", {"start": v(40.34, 24.96) * mm, "end": v(40.34, 23.96) * mm});
            skLineSegment(sketch, "E589", {"start": v(40.34, 23.96) * mm, "end": v(26.34, 23.96) * mm});
            skLineSegment(sketch, "E590", {"start": v(26.34, 23.96) * mm, "end": v(26.34, 24.96) * mm});
            skLineSegment(sketch, "E591", {"start": v(26.34, 24.96) * mm, "end": v(25.54, 24.96) * mm});
            skLineSegment(sketch, "E592", {"start": v(25.54, 24.96) * mm, "end": v(25.54, 28.06) * mm});
            skLineSegment(sketch, "E593", {"start": v(25.54, 28.06) * mm, "end": v(26.34, 28.06) * mm});
            skLineSegment(sketch, "E594", {"start": v(26.34, 28.06) * mm, "end": v(26.34, 33.86) * mm});
            skLineSegment(sketch, "E595", {"start": v(26.34, 33.86) * mm, "end": v(25.54, 33.86) * mm});
            skLineSegment(sketch, "E596", {"start": v(25.54, 33.86) * mm, "end": v(25.54, 36.96) * mm});
            skLineSegment(sketch, "E597", {"start": v(25.54, 36.96) * mm, "end": v(26.34, 36.96) * mm});
            skLineSegment(sketch, "E598", {"start": v(26.34, 36.96) * mm, "end": v(26.34, 37.96) * mm});
            skLineSegment(sketch, "E599", {"start": v(26.34, 37.96) * mm, "end": v(40.34, 37.96) * mm});
            skLineSegment(sketch, "E600", {"start": v(40.34, 37.96) * mm, "end": v(40.34, 36.96) * mm});
            skLineSegment(sketch, "E601", {"start": v(40.34, 36.96) * mm, "end": v(41.14, 36.96) * mm});
            skLineSegment(sketch, "E602", {"start": v(41.14, 36.96) * mm, "end": v(41.14, 33.86) * mm});
            skLineSegment(sketch, "E603", {"start": v(41.14, 33.86) * mm, "end": v(40.34, 33.86) * mm});
            skLineSegment(sketch, "E604", {"start": v(40.34, 33.86) * mm, "end": v(40.34, 28.06) * mm});
            skLineSegment(sketch, "E605", {"start": v(40.34, 28.06) * mm, "end": v(41.14, 28.06) * mm});
            skLineSegment(sketch, "E606", {"start": v(41.14, 28.06) * mm, "end": v(41.14, 24.96) * mm});
            skLineSegment(sketch, "E607", {"start": v(41.14, 24.96) * mm, "end": v(40.34, 24.96) * mm});
            skLineSegment(sketch, "E608", {"start": v(40.34, 5.9) * mm, "end": v(40.34, 4.9) * mm});
            skLineSegment(sketch, "E609", {"start": v(40.34, 4.9) * mm, "end": v(26.34, 4.9) * mm});
            skLineSegment(sketch, "E610", {"start": v(26.34, 4.9) * mm, "end": v(26.34, 5.9) * mm});
            skLineSegment(sketch, "E611", {"start": v(26.34, 5.9) * mm, "end": v(25.54, 5.9) * mm});
            skLineSegment(sketch, "E612", {"start": v(25.54, 5.9) * mm, "end": v(25.54, 9) * mm});
            skLineSegment(sketch, "E613", {"start": v(25.54, 9) * mm, "end": v(26.34, 9) * mm});
            skLineSegment(sketch, "E614", {"start": v(26.34, 9) * mm, "end": v(26.34, 14.8) * mm});
            skLineSegment(sketch, "E615", {"start": v(26.34, 14.8) * mm, "end": v(25.54, 14.8) * mm});
            skLineSegment(sketch, "E616", {"start": v(25.54, 14.8) * mm, "end": v(25.54, 17.9) * mm});
            skLineSegment(sketch, "E617", {"start": v(25.54, 17.9) * mm, "end": v(26.34, 17.9) * mm});
            skLineSegment(sketch, "E618", {"start": v(26.34, 17.9) * mm, "end": v(26.34, 18.9) * mm});
            skLineSegment(sketch, "E619", {"start": v(26.34, 18.9) * mm, "end": v(40.34, 18.9) * mm});
            skLineSegment(sketch, "E620", {"start": v(40.34, 18.9) * mm, "end": v(40.34, 17.9) * mm});
            skLineSegment(sketch, "E621", {"start": v(40.34, 17.9) * mm, "end": v(41.14, 17.9) * mm});
            skLineSegment(sketch, "E622", {"start": v(41.14, 17.9) * mm, "end": v(41.14, 14.8) * mm});
            skLineSegment(sketch, "E623", {"start": v(41.14, 14.8) * mm, "end": v(40.34, 14.8) * mm});
            skLineSegment(sketch, "E624", {"start": v(40.34, 14.8) * mm, "end": v(40.34, 9) * mm});
            skLineSegment(sketch, "E625", {"start": v(40.34, 9) * mm, "end": v(41.14, 9) * mm});
            skLineSegment(sketch, "E626", {"start": v(41.14, 9) * mm, "end": v(41.14, 5.9) * mm});
            skLineSegment(sketch, "E627", {"start": v(41.14, 5.9) * mm, "end": v(40.34, 5.9) * mm});
            skLineSegment(sketch, "E628", {"start": v(40.34, -13.14) * mm, "end": v(40.34, -14.14) * mm});
            skLineSegment(sketch, "E629", {"start": v(40.34, -14.14) * mm, "end": v(26.34, -14.14) * mm});
            skLineSegment(sketch, "E630", {"start": v(26.34, -14.14) * mm, "end": v(26.34, -13.14) * mm});
            skLineSegment(sketch, "E631", {"start": v(26.34, -13.14) * mm, "end": v(25.54, -13.14) * mm});
            skLineSegment(sketch, "E632", {"start": v(25.54, -13.14) * mm, "end": v(25.54, -10.04) * mm});
            skLineSegment(sketch, "E633", {"start": v(25.54, -10.04) * mm, "end": v(26.34, -10.04) * mm});
            skLineSegment(sketch, "E634", {"start": v(26.34, -10.04) * mm, "end": v(26.34, -4.24) * mm});
            skLineSegment(sketch, "E635", {"start": v(26.34, -4.24) * mm, "end": v(25.54, -4.24) * mm});
            skLineSegment(sketch, "E636", {"start": v(25.54, -4.24) * mm, "end": v(25.54, -1.14) * mm});
            skLineSegment(sketch, "E637", {"start": v(25.54, -1.14) * mm, "end": v(26.34, -1.14) * mm});
            skLineSegment(sketch, "E638", {"start": v(26.34, -1.14) * mm, "end": v(26.34, -0.14) * mm});
            skLineSegment(sketch, "E639", {"start": v(26.34, -0.14) * mm, "end": v(40.34, -0.14) * mm});
            skLineSegment(sketch, "E640", {"start": v(40.34, -0.14) * mm, "end": v(40.34, -1.14) * mm});
            skLineSegment(sketch, "E641", {"start": v(40.34, -1.14) * mm, "end": v(41.14, -1.14) * mm});
            skLineSegment(sketch, "E642", {"start": v(41.14, -1.14) * mm, "end": v(41.14, -4.24) * mm});
            skLineSegment(sketch, "E643", {"start": v(41.14, -4.24) * mm, "end": v(40.34, -4.24) * mm});
            skLineSegment(sketch, "E644", {"start": v(40.34, -4.24) * mm, "end": v(40.34, -10.04) * mm});
            skLineSegment(sketch, "E645", {"start": v(40.34, -10.04) * mm, "end": v(41.14, -10.04) * mm});
            skLineSegment(sketch, "E646", {"start": v(41.14, -10.04) * mm, "end": v(41.14, -13.14) * mm});
            skLineSegment(sketch, "E647", {"start": v(41.14, -13.14) * mm, "end": v(40.34, -13.14) * mm});
            skLineSegment(sketch, "E648", {"start": v(40.34, -32.2) * mm, "end": v(40.34, -33.2) * mm});
            skLineSegment(sketch, "E649", {"start": v(40.34, -33.2) * mm, "end": v(26.34, -33.2) * mm});
            skLineSegment(sketch, "E650", {"start": v(26.34, -33.2) * mm, "end": v(26.34, -32.2) * mm});
            skLineSegment(sketch, "E651", {"start": v(26.34, -32.2) * mm, "end": v(25.54, -32.2) * mm});
            skLineSegment(sketch, "E652", {"start": v(25.54, -32.2) * mm, "end": v(25.54, -29.1) * mm});
            skLineSegment(sketch, "E653", {"start": v(25.54, -29.1) * mm, "end": v(26.34, -29.1) * mm});
            skLineSegment(sketch, "E654", {"start": v(26.34, -29.1) * mm, "end": v(26.34, -23.3) * mm});
            skLineSegment(sketch, "E655", {"start": v(26.34, -23.3) * mm, "end": v(25.54, -23.3) * mm});
            skLineSegment(sketch, "E656", {"start": v(25.54, -23.3) * mm, "end": v(25.54, -20.2) * mm});
            skLineSegment(sketch, "E657", {"start": v(25.54, -20.2) * mm, "end": v(26.34, -20.2) * mm});
            skLineSegment(sketch, "E658", {"start": v(26.34, -20.2) * mm, "end": v(26.34, -19.2) * mm});
            skLineSegment(sketch, "E659", {"start": v(26.34, -19.2) * mm, "end": v(40.34, -19.2) * mm});
            skLineSegment(sketch, "E660", {"start": v(40.34, -19.2) * mm, "end": v(40.34, -20.2) * mm});
            skLineSegment(sketch, "E661", {"start": v(40.34, -20.2) * mm, "end": v(41.14, -20.2) * mm});
            skLineSegment(sketch, "E662", {"start": v(41.14, -20.2) * mm, "end": v(41.14, -23.3) * mm});
            skLineSegment(sketch, "E663", {"start": v(41.14, -23.3) * mm, "end": v(40.34, -23.3) * mm});
            skLineSegment(sketch, "E664", {"start": v(40.34, -23.3) * mm, "end": v(40.34, -29.1) * mm});
            skLineSegment(sketch, "E665", {"start": v(40.34, -29.1) * mm, "end": v(41.14, -29.1) * mm});
            skLineSegment(sketch, "E666", {"start": v(41.14, -29.1) * mm, "end": v(41.14, -32.2) * mm});
            skLineSegment(sketch, "E667", {"start": v(41.14, -32.2) * mm, "end": v(40.34, -32.2) * mm});
            skLineSegment(sketch, "E668", {"start": v(40.34, -51.24) * mm, "end": v(40.34, -52.24) * mm});
            skLineSegment(sketch, "E669", {"start": v(40.34, -52.24) * mm, "end": v(26.34, -52.24) * mm});
            skLineSegment(sketch, "E670", {"start": v(26.34, -52.24) * mm, "end": v(26.34, -51.24) * mm});
            skLineSegment(sketch, "E671", {"start": v(26.34, -51.24) * mm, "end": v(25.54, -51.24) * mm});
            skLineSegment(sketch, "E672", {"start": v(25.54, -51.24) * mm, "end": v(25.54, -48.14) * mm});
            skLineSegment(sketch, "E673", {"start": v(25.54, -48.14) * mm, "end": v(26.34, -48.14) * mm});
            skLineSegment(sketch, "E674", {"start": v(26.34, -48.14) * mm, "end": v(26.34, -42.34) * mm});
            skLineSegment(sketch, "E675", {"start": v(26.34, -42.34) * mm, "end": v(25.54, -42.34) * mm});
            skLineSegment(sketch, "E676", {"start": v(25.54, -42.34) * mm, "end": v(25.54, -39.24) * mm});
            skLineSegment(sketch, "E677", {"start": v(25.54, -39.24) * mm, "end": v(26.34, -39.24) * mm});
            skLineSegment(sketch, "E678", {"start": v(26.34, -39.24) * mm, "end": v(26.34, -38.24) * mm});
            skLineSegment(sketch, "E679", {"start": v(26.34, -38.24) * mm, "end": v(40.34, -38.24) * mm});
            skLineSegment(sketch, "E680", {"start": v(40.34, -38.24) * mm, "end": v(40.34, -39.24) * mm});
            skLineSegment(sketch, "E681", {"start": v(40.34, -39.24) * mm, "end": v(41.14, -39.24) * mm});
            skLineSegment(sketch, "E682", {"start": v(41.14, -39.24) * mm, "end": v(41.14, -42.34) * mm});
            skLineSegment(sketch, "E683", {"start": v(41.14, -42.34) * mm, "end": v(40.34, -42.34) * mm});
            skLineSegment(sketch, "E684", {"start": v(40.34, -42.34) * mm, "end": v(40.34, -48.14) * mm});
            skLineSegment(sketch, "E685", {"start": v(40.34, -48.14) * mm, "end": v(41.14, -48.14) * mm});
            skLineSegment(sketch, "E686", {"start": v(41.14, -48.14) * mm, "end": v(41.14, -51.24) * mm});
            skLineSegment(sketch, "E687", {"start": v(41.14, -51.24) * mm, "end": v(40.34, -51.24) * mm});
            skLineSegment(sketch, "E688", {"start": v(59.39, 24.96) * mm, "end": v(59.39, 23.96) * mm});
            skLineSegment(sketch, "E689", {"start": v(59.39, 23.96) * mm, "end": v(45.39, 23.96) * mm});
            skLineSegment(sketch, "E690", {"start": v(45.39, 23.96) * mm, "end": v(45.39, 24.96) * mm});
            skLineSegment(sketch, "E691", {"start": v(45.39, 24.96) * mm, "end": v(44.59, 24.96) * mm});
            skLineSegment(sketch, "E692", {"start": v(44.59, 24.96) * mm, "end": v(44.59, 28.06) * mm});
            skLineSegment(sketch, "E693", {"start": v(44.59, 28.06) * mm, "end": v(45.39, 28.06) * mm});
            skLineSegment(sketch, "E694", {"start": v(45.39, 28.06) * mm, "end": v(45.39, 33.86) * mm});
            skLineSegment(sketch, "E695", {"start": v(45.39, 33.86) * mm, "end": v(44.59, 33.86) * mm});
            skLineSegment(sketch, "E696", {"start": v(44.59, 33.86) * mm, "end": v(44.59, 36.96) * mm});
            skLineSegment(sketch, "E697", {"start": v(44.59, 36.96) * mm, "end": v(45.39, 36.96) * mm});
            skLineSegment(sketch, "E698", {"start": v(45.39, 36.96) * mm, "end": v(45.39, 37.96) * mm});
            skLineSegment(sketch, "E699", {"start": v(45.39, 37.96) * mm, "end": v(59.39, 37.96) * mm});
            skLineSegment(sketch, "E700", {"start": v(59.39, 37.96) * mm, "end": v(59.39, 36.96) * mm});
            skLineSegment(sketch, "E701", {"start": v(59.39, 36.96) * mm, "end": v(60.19, 36.96) * mm});
            skLineSegment(sketch, "E702", {"start": v(60.19, 36.96) * mm, "end": v(60.19, 33.86) * mm});
            skLineSegment(sketch, "E703", {"start": v(60.19, 33.86) * mm, "end": v(59.39, 33.86) * mm});
            skLineSegment(sketch, "E704", {"start": v(59.39, 33.86) * mm, "end": v(59.39, 28.06) * mm});
            skLineSegment(sketch, "E705", {"start": v(59.39, 28.06) * mm, "end": v(60.19, 28.06) * mm});
            skLineSegment(sketch, "E706", {"start": v(60.19, 28.06) * mm, "end": v(60.19, 24.96) * mm});
            skLineSegment(sketch, "E707", {"start": v(60.19, 24.96) * mm, "end": v(59.39, 24.96) * mm});
            skLineSegment(sketch, "E708", {"start": v(59.39, 5.9) * mm, "end": v(59.39, 4.9) * mm});
            skLineSegment(sketch, "E709", {"start": v(59.39, 4.9) * mm, "end": v(45.39, 4.9) * mm});
            skLineSegment(sketch, "E710", {"start": v(45.39, 4.9) * mm, "end": v(45.39, 5.9) * mm});
            skLineSegment(sketch, "E711", {"start": v(45.39, 5.9) * mm, "end": v(44.59, 5.9) * mm});
            skLineSegment(sketch, "E712", {"start": v(44.59, 5.9) * mm, "end": v(44.59, 9) * mm});
            skLineSegment(sketch, "E713", {"start": v(44.59, 9) * mm, "end": v(45.39, 9) * mm});
            skLineSegment(sketch, "E714", {"start": v(45.39, 9) * mm, "end": v(45.39, 14.8) * mm});
            skLineSegment(sketch, "E715", {"start": v(45.39, 14.8) * mm, "end": v(44.59, 14.8) * mm});
            skLineSegment(sketch, "E716", {"start": v(44.59, 14.8) * mm, "end": v(44.59, 17.9) * mm});
            skLineSegment(sketch, "E717", {"start": v(44.59, 17.9) * mm, "end": v(45.39, 17.9) * mm});
            skLineSegment(sketch, "E718", {"start": v(45.39, 17.9) * mm, "end": v(45.39, 18.9) * mm});
            skLineSegment(sketch, "E719", {"start": v(45.39, 18.9) * mm, "end": v(59.39, 18.9) * mm});
            skLineSegment(sketch, "E720", {"start": v(59.39, 18.9) * mm, "end": v(59.39, 17.9) * mm});
            skLineSegment(sketch, "E721", {"start": v(59.39, 17.9) * mm, "end": v(60.19, 17.9) * mm});
            skLineSegment(sketch, "E722", {"start": v(60.19, 17.9) * mm, "end": v(60.19, 14.8) * mm});
            skLineSegment(sketch, "E723", {"start": v(60.19, 14.8) * mm, "end": v(59.39, 14.8) * mm});
            skLineSegment(sketch, "E724", {"start": v(59.39, 14.8) * mm, "end": v(59.39, 9) * mm});
            skLineSegment(sketch, "E725", {"start": v(59.39, 9) * mm, "end": v(60.19, 9) * mm});
            skLineSegment(sketch, "E726", {"start": v(60.19, 9) * mm, "end": v(60.19, 5.9) * mm});
            skLineSegment(sketch, "E727", {"start": v(60.19, 5.9) * mm, "end": v(59.39, 5.9) * mm});
            skLineSegment(sketch, "E728", {"start": v(59.39, -13.14) * mm, "end": v(59.39, -14.14) * mm});
            skLineSegment(sketch, "E729", {"start": v(59.39, -14.14) * mm, "end": v(45.39, -14.14) * mm});
            skLineSegment(sketch, "E730", {"start": v(45.39, -14.14) * mm, "end": v(45.39, -13.14) * mm});
            skLineSegment(sketch, "E731", {"start": v(45.39, -13.14) * mm, "end": v(44.59, -13.14) * mm});
            skLineSegment(sketch, "E732", {"start": v(44.59, -13.14) * mm, "end": v(44.59, -10.04) * mm});
            skLineSegment(sketch, "E733", {"start": v(44.59, -10.04) * mm, "end": v(45.39, -10.04) * mm});
            skLineSegment(sketch, "E734", {"start": v(45.39, -10.04) * mm, "end": v(45.39, -4.24) * mm});
            skLineSegment(sketch, "E735", {"start": v(45.39, -4.24) * mm, "end": v(44.59, -4.24) * mm});
            skLineSegment(sketch, "E736", {"start": v(44.59, -4.24) * mm, "end": v(44.59, -1.14) * mm});
            skLineSegment(sketch, "E737", {"start": v(44.59, -1.14) * mm, "end": v(45.39, -1.14) * mm});
            skLineSegment(sketch, "E738", {"start": v(45.39, -1.14) * mm, "end": v(45.39, -0.14) * mm});
            skLineSegment(sketch, "E739", {"start": v(45.39, -0.14) * mm, "end": v(59.39, -0.14) * mm});
            skLineSegment(sketch, "E740", {"start": v(59.39, -0.14) * mm, "end": v(59.39, -1.14) * mm});
            skLineSegment(sketch, "E741", {"start": v(59.39, -1.14) * mm, "end": v(60.19, -1.14) * mm});
            skLineSegment(sketch, "E742", {"start": v(60.19, -1.14) * mm, "end": v(60.19, -4.24) * mm});
            skLineSegment(sketch, "E743", {"start": v(60.19, -4.24) * mm, "end": v(59.39, -4.24) * mm});
            skLineSegment(sketch, "E744", {"start": v(59.39, -4.24) * mm, "end": v(59.39, -10.04) * mm});
            skLineSegment(sketch, "E745", {"start": v(59.39, -10.04) * mm, "end": v(60.19, -10.04) * mm});
            skLineSegment(sketch, "E746", {"start": v(60.19, -10.04) * mm, "end": v(60.19, -13.14) * mm});
            skLineSegment(sketch, "E747", {"start": v(60.19, -13.14) * mm, "end": v(59.39, -13.14) * mm});
            skLineSegment(sketch, "E748", {"start": v(78.44, 5.9) * mm, "end": v(78.44, 4.9) * mm});
            skLineSegment(sketch, "E749", {"start": v(78.44, 4.9) * mm, "end": v(64.44, 4.9) * mm});
            skLineSegment(sketch, "E750", {"start": v(64.44, 4.9) * mm, "end": v(64.44, 5.9) * mm});
            skLineSegment(sketch, "E751", {"start": v(64.44, 5.9) * mm, "end": v(63.64, 5.9) * mm});
            skLineSegment(sketch, "E752", {"start": v(63.64, 5.9) * mm, "end": v(63.64, 9) * mm});
            skLineSegment(sketch, "E753", {"start": v(63.64, 9) * mm, "end": v(64.44, 9) * mm});
            skLineSegment(sketch, "E754", {"start": v(64.44, 9) * mm, "end": v(64.44, 14.8) * mm});
            skLineSegment(sketch, "E755", {"start": v(64.44, 14.8) * mm, "end": v(63.64, 14.8) * mm});
            skLineSegment(sketch, "E756", {"start": v(63.64, 14.8) * mm, "end": v(63.64, 17.9) * mm});
            skLineSegment(sketch, "E757", {"start": v(63.64, 17.9) * mm, "end": v(64.44, 17.9) * mm});
            skLineSegment(sketch, "E758", {"start": v(64.44, 17.9) * mm, "end": v(64.44, 18.9) * mm});
            skLineSegment(sketch, "E759", {"start": v(64.44, 18.9) * mm, "end": v(78.44, 18.9) * mm});
            skLineSegment(sketch, "E760", {"start": v(78.44, 18.9) * mm, "end": v(78.44, 17.9) * mm});
            skLineSegment(sketch, "E761", {"start": v(78.44, 17.9) * mm, "end": v(79.24, 17.9) * mm});
            skLineSegment(sketch, "E762", {"start": v(79.24, 17.9) * mm, "end": v(79.24, 14.8) * mm});
            skLineSegment(sketch, "E763", {"start": v(79.24, 14.8) * mm, "end": v(78.44, 14.8) * mm});
            skLineSegment(sketch, "E764", {"start": v(78.44, 14.8) * mm, "end": v(78.44, 9) * mm});
            skLineSegment(sketch, "E765", {"start": v(78.44, 9) * mm, "end": v(79.24, 9) * mm});
            skLineSegment(sketch, "E766", {"start": v(79.24, 9) * mm, "end": v(79.24, 5.9) * mm});
            skLineSegment(sketch, "E767", {"start": v(79.24, 5.9) * mm, "end": v(78.44, 5.9) * mm});
            skLineSegment(sketch, "E768", {"start": v(78.44, -13.14) * mm, "end": v(78.44, -14.14) * mm});
            skLineSegment(sketch, "E769", {"start": v(78.44, -14.14) * mm, "end": v(64.44, -14.14) * mm});
            skLineSegment(sketch, "E770", {"start": v(64.44, -14.14) * mm, "end": v(64.44, -13.14) * mm});
            skLineSegment(sketch, "E771", {"start": v(64.44, -13.14) * mm, "end": v(63.64, -13.14) * mm});
            skLineSegment(sketch, "E772", {"start": v(63.64, -13.14) * mm, "end": v(63.64, -10.04) * mm});
            skLineSegment(sketch, "E773", {"start": v(63.64, -10.04) * mm, "end": v(64.44, -10.04) * mm});
            skLineSegment(sketch, "E774", {"start": v(64.44, -10.04) * mm, "end": v(64.44, -4.24) * mm});
            skLineSegment(sketch, "E775", {"start": v(64.44, -4.24) * mm, "end": v(63.64, -4.24) * mm});
            skLineSegment(sketch, "E776", {"start": v(63.64, -4.24) * mm, "end": v(63.64, -1.14) * mm});
            skLineSegment(sketch, "E777", {"start": v(63.64, -1.14) * mm, "end": v(64.44, -1.14) * mm});
            skLineSegment(sketch, "E778", {"start": v(64.44, -1.14) * mm, "end": v(64.44, -0.14) * mm});
            skLineSegment(sketch, "E779", {"start": v(64.44, -0.14) * mm, "end": v(78.44, -0.14) * mm});
            skLineSegment(sketch, "E780", {"start": v(78.44, -0.14) * mm, "end": v(78.44, -1.14) * mm});
            skLineSegment(sketch, "E781", {"start": v(78.44, -1.14) * mm, "end": v(79.24, -1.14) * mm});
            skLineSegment(sketch, "E782", {"start": v(79.24, -1.14) * mm, "end": v(79.24, -4.24) * mm});
            skLineSegment(sketch, "E783", {"start": v(79.24, -4.24) * mm, "end": v(78.44, -4.24) * mm});
            skLineSegment(sketch, "E784", {"start": v(78.44, -4.24) * mm, "end": v(78.44, -10.04) * mm});
            skLineSegment(sketch, "E785", {"start": v(78.44, -10.04) * mm, "end": v(79.24, -10.04) * mm});
            skLineSegment(sketch, "E786", {"start": v(79.24, -10.04) * mm, "end": v(79.24, -13.14) * mm});
            skLineSegment(sketch, "E787", {"start": v(79.24, -13.14) * mm, "end": v(78.44, -13.14) * mm});
            skLineSegment(sketch, "E788", {"start": v(79.52, -26.7) * mm, "end": v(79.52, -32.96) * mm});
            skLineSegment(sketch, "E789", {"start": v(79.52, -32.96) * mm, "end": v(77.9, -32.96) * mm});
            skLineSegment(sketch, "E790", {"start": v(77.9, -32.96) * mm, "end": v(77.9, -33.94) * mm});
            skLineSegment(sketch, "E791", {"start": v(77.9, -33.94) * mm, "end": v(74.6, -33.94) * mm});
            skLineSegment(sketch, "E792", {"start": v(74.6, -33.94) * mm, "end": v(74.6, -32.96) * mm});
            skLineSegment(sketch, "E793", {"start": v(74.6, -32.96) * mm, "end": v(72.87, -32.96) * mm});
            skLineSegment(sketch, "E794", {"start": v(72.87, -32.96) * mm, "end": v(72.87, -32.16) * mm});
            skLineSegment(sketch, "E795", {"start": v(72.87, -32.16) * mm, "end": v(72.1, -32.16) * mm});
            skLineSegment(sketch, "E796", {"start": v(72.1, -32.16) * mm, "end": v(72.1, -32.2) * mm});
            skLineSegment(sketch, "E797", {"start": v(72.1, -32.2) * mm, "end": v(71.3, -32.2) * mm});
            skLineSegment(sketch, "E798", {"start": v(71.3, -32.2) * mm, "end": v(71.3, -33.2) * mm});
            skLineSegment(sketch, "E799", {"start": v(71.3, -33.2) * mm, "end": v(57.3, -33.2) * mm});
            skLineSegment(sketch, "E800", {"start": v(57.3, -33.2) * mm, "end": v(57.3, -32.2) * mm});
            skLineSegment(sketch, "E801", {"start": v(57.3, -32.2) * mm, "end": v(56.5, -32.2) * mm});
            skLineSegment(sketch, "E802", {"start": v(56.5, -32.2) * mm, "end": v(56.5, -32.16) * mm});
            skLineSegment(sketch, "E803", {"start": v(56.5, -32.16) * mm, "end": v(55.72, -32.16) * mm});
            skLineSegment(sketch, "E804", {"start": v(55.72, -32.16) * mm, "end": v(55.72, -32.96) * mm});
            skLineSegment(sketch, "E805", {"start": v(55.72, -32.96) * mm, "end": v(54, -32.96) * mm});
            skLineSegment(sketch, "E806", {"start": v(54, -32.96) * mm, "end": v(54, -33.94) * mm});
            skLineSegment(sketch, "E807", {"start": v(54, -33.94) * mm, "end": v(50.7, -33.94) * mm});
            skLineSegment(sketch, "E808", {"start": v(50.7, -33.94) * mm, "end": v(50.7, -32.96) * mm});
            skLineSegment(sketch, "E809", {"start": v(50.7, -32.96) * mm, "end": v(49.07, -32.96) * mm});
            skLineSegment(sketch, "E810", {"start": v(49.07, -32.96) * mm, "end": v(49.07, -26.7) * mm});
            skLineSegment(sketch, "E811", {"start": v(49.07, -26.7) * mm, "end": v(48.2, -26.7) * mm});
            skLineSegment(sketch, "E812", {"start": v(48.2, -26.7) * mm, "end": v(48.2, -23.9) * mm});
            skLineSegment(sketch, "E813", {"start": v(48.2, -23.9) * mm, "end": v(49.07, -23.9) * mm});
            skLineSegment(sketch, "E814", {"start": v(49.07, -23.9) * mm, "end": v(49.07, -20.66) * mm});
            skLineSegment(sketch, "E815", {"start": v(49.07, -20.66) * mm, "end": v(50.7, -20.66) * mm});
            skLineSegment(sketch, "E816", {"start": v(50.7, -20.66) * mm, "end": v(50.7, -19.74) * mm});
            skLineSegment(sketch, "E817", {"start": v(50.7, -19.74) * mm, "end": v(54, -19.74) * mm});
            skLineSegment(sketch, "E818", {"start": v(54, -19.74) * mm, "end": v(54, -20.66) * mm});
            skLineSegment(sketch, "E819", {"start": v(54, -20.66) * mm, "end": v(55.72, -20.66) * mm});
            skLineSegment(sketch, "E820", {"start": v(55.72, -20.66) * mm, "end": v(55.72, -21.46) * mm});
            skLineSegment(sketch, "E821", {"start": v(55.72, -21.46) * mm, "end": v(56.5, -21.46) * mm});
            skLineSegment(sketch, "E822", {"start": v(56.5, -21.46) * mm, "end": v(56.5, -20.2) * mm});
            skLineSegment(sketch, "E823", {"start": v(56.5, -20.2) * mm, "end": v(57.3, -20.2) * mm});
            skLineSegment(sketch, "E824", {"start": v(57.3, -20.2) * mm, "end": v(57.3, -19.2) * mm});
            skLineSegment(sketch, "E825", {"start": v(57.3, -19.2) * mm, "end": v(71.3, -19.2) * mm});
            skLineSegment(sketch, "E826", {"start": v(71.3, -19.2) * mm, "end": v(71.3, -20.2) * mm});
            skLineSegment(sketch, "E827", {"start": v(71.3, -20.2) * mm, "end": v(72.1, -20.2) * mm});
            skLineSegment(sketch, "E828", {"start": v(72.1, -20.2) * mm, "end": v(72.1, -21.46) * mm});
            skLineSegment(sketch, "E829", {"start": v(72.1, -21.46) * mm, "end": v(72.87, -21.46) * mm});
            skLineSegment(sketch, "E830", {"start": v(72.87, -21.46) * mm, "end": v(72.87, -20.66) * mm});
            skLineSegment(sketch, "E831", {"start": v(72.87, -20.66) * mm, "end": v(74.6, -20.66) * mm});
            skLineSegment(sketch, "E832", {"start": v(74.6, -20.66) * mm, "end": v(74.6, -19.74) * mm});
            skLineSegment(sketch, "E833", {"start": v(74.6, -19.74) * mm, "end": v(77.9, -19.74) * mm});
            skLineSegment(sketch, "E834", {"start": v(77.9, -19.74) * mm, "end": v(77.9, -20.66) * mm});
            skLineSegment(sketch, "E835", {"start": v(77.9, -20.66) * mm, "end": v(79.52, -20.66) * mm});
            skLineSegment(sketch, "E836", {"start": v(79.52, -20.66) * mm, "end": v(79.52, -23.9) * mm});
            skLineSegment(sketch, "E837", {"start": v(79.52, -23.9) * mm, "end": v(80.4, -23.9) * mm});
            skLineSegment(sketch, "E838", {"start": v(80.4, -23.9) * mm, "end": v(80.4, -26.7) * mm});
            skLineSegment(sketch, "E839", {"start": v(80.4, -26.7) * mm, "end": v(79.52, -26.7) * mm});
            skLineSegment(sketch, "E840", {"start": v(79.52, -45.74) * mm, "end": v(79.52, -52.01) * mm});
            skLineSegment(sketch, "E841", {"start": v(79.52, -52.01) * mm, "end": v(77.9, -52.01) * mm});
            skLineSegment(sketch, "E842", {"start": v(77.9, -52.01) * mm, "end": v(77.9, -53) * mm});
            skLineSegment(sketch, "E843", {"start": v(77.9, -53) * mm, "end": v(74.6, -53) * mm});
            skLineSegment(sketch, "E844", {"start": v(74.6, -53) * mm, "end": v(74.6, -52.01) * mm});
            skLineSegment(sketch, "E845", {"start": v(74.6, -52.01) * mm, "end": v(72.87, -52.01) * mm});
            skLineSegment(sketch, "E846", {"start": v(72.87, -52.01) * mm, "end": v(72.87, -51.21) * mm});
            skLineSegment(sketch, "E847", {"start": v(72.87, -51.21) * mm, "end": v(72.1, -51.21) * mm});
            skLineSegment(sketch, "E848", {"start": v(72.1, -51.21) * mm, "end": v(72.1, -51.24) * mm});
            skLineSegment(sketch, "E849", {"start": v(72.1, -51.24) * mm, "end": v(71.3, -51.24) * mm});
            skLineSegment(sketch, "E850", {"start": v(71.3, -51.24) * mm, "end": v(71.3, -52.24) * mm});
            skLineSegment(sketch, "E851", {"start": v(71.3, -52.24) * mm, "end": v(57.3, -52.24) * mm});
            skLineSegment(sketch, "E852", {"start": v(57.3, -52.24) * mm, "end": v(57.3, -51.24) * mm});
            skLineSegment(sketch, "E853", {"start": v(57.3, -51.24) * mm, "end": v(56.5, -51.24) * mm});
            skLineSegment(sketch, "E854", {"start": v(56.5, -51.24) * mm, "end": v(56.5, -51.21) * mm});
            skLineSegment(sketch, "E855", {"start": v(56.5, -51.21) * mm, "end": v(55.72, -51.21) * mm});
            skLineSegment(sketch, "E856", {"start": v(55.72, -51.21) * mm, "end": v(55.72, -52.01) * mm});
            skLineSegment(sketch, "E857", {"start": v(55.72, -52.01) * mm, "end": v(54, -52.01) * mm});
            skLineSegment(sketch, "E858", {"start": v(54, -52.01) * mm, "end": v(54, -53) * mm});
            skLineSegment(sketch, "E859", {"start": v(54, -53) * mm, "end": v(50.7, -53) * mm});
            skLineSegment(sketch, "E860", {"start": v(50.7, -53) * mm, "end": v(50.7, -52.01) * mm});
            skLineSegment(sketch, "E861", {"start": v(50.7, -52.01) * mm, "end": v(49.07, -52.01) * mm});
            skLineSegment(sketch, "E862", {"start": v(49.07, -52.01) * mm, "end": v(49.07, -45.74) * mm});
            skLineSegment(sketch, "E863", {"start": v(49.07, -45.74) * mm, "end": v(48.2, -45.74) * mm});
            skLineSegment(sketch, "E864", {"start": v(48.2, -45.74) * mm, "end": v(48.2, -42.94) * mm});
            skLineSegment(sketch, "E865", {"start": v(48.2, -42.94) * mm, "end": v(49.07, -42.94) * mm});
            skLineSegment(sketch, "E866", {"start": v(49.07, -42.94) * mm, "end": v(49.07, -39.71) * mm});
            skLineSegment(sketch, "E867", {"start": v(49.07, -39.71) * mm, "end": v(50.7, -39.71) * mm});
            skLineSegment(sketch, "E868", {"start": v(50.7, -39.71) * mm, "end": v(50.7, -38.8) * mm});
            skLineSegment(sketch, "E869", {"start": v(50.7, -38.8) * mm, "end": v(54, -38.8) * mm});
            skLineSegment(sketch, "E870", {"start": v(54, -38.8) * mm, "end": v(54, -39.71) * mm});
            skLineSegment(sketch, "E871", {"start": v(54, -39.71) * mm, "end": v(55.72, -39.71) * mm});
            skLineSegment(sketch, "E872", {"start": v(55.72, -39.71) * mm, "end": v(55.72, -40.51) * mm});
            skLineSegment(sketch, "E873", {"start": v(55.72, -40.51) * mm, "end": v(56.5, -40.51) * mm});
            skLineSegment(sketch, "E874", {"start": v(56.5, -40.51) * mm, "end": v(56.5, -39.24) * mm});
            skLineSegment(sketch, "E875", {"start": v(56.5, -39.24) * mm, "end": v(57.3, -39.24) * mm});
            skLineSegment(sketch, "E876", {"start": v(57.3, -39.24) * mm, "end": v(57.3, -38.24) * mm});
            skLineSegment(sketch, "E877", {"start": v(57.3, -38.24) * mm, "end": v(71.3, -38.24) * mm});
            skLineSegment(sketch, "E878", {"start": v(71.3, -38.24) * mm, "end": v(71.3, -39.24) * mm});
            skLineSegment(sketch, "E879", {"start": v(71.3, -39.24) * mm, "end": v(72.1, -39.24) * mm});
            skLineSegment(sketch, "E880", {"start": v(72.1, -39.24) * mm, "end": v(72.1, -40.51) * mm});
            skLineSegment(sketch, "E881", {"start": v(72.1, -40.51) * mm, "end": v(72.87, -40.51) * mm});
            skLineSegment(sketch, "E882", {"start": v(72.87, -40.51) * mm, "end": v(72.87, -39.71) * mm});
            skLineSegment(sketch, "E883", {"start": v(72.87, -39.71) * mm, "end": v(74.6, -39.71) * mm});
            skLineSegment(sketch, "E884", {"start": v(74.6, -39.71) * mm, "end": v(74.6, -38.8) * mm});
            skLineSegment(sketch, "E885", {"start": v(74.6, -38.8) * mm, "end": v(77.9, -38.8) * mm});
            skLineSegment(sketch, "E886", {"start": v(77.9, -38.8) * mm, "end": v(77.9, -39.71) * mm});
            skLineSegment(sketch, "E887", {"start": v(77.9, -39.71) * mm, "end": v(79.52, -39.71) * mm});
            skLineSegment(sketch, "E888", {"start": v(79.52, -39.71) * mm, "end": v(79.52, -42.94) * mm});
            skLineSegment(sketch, "E889", {"start": v(79.52, -42.94) * mm, "end": v(80.4, -42.94) * mm});
            skLineSegment(sketch, "E890", {"start": v(80.4, -42.94) * mm, "end": v(80.4, -45.74) * mm});
            skLineSegment(sketch, "E891", {"start": v(80.4, -45.74) * mm, "end": v(79.52, -45.74) * mm});
            skLineSegment(sketch, "E892", {"start": v(83.2, 24.96) * mm, "end": v(83.2, 23.96) * mm});
            skLineSegment(sketch, "E893", {"start": v(83.2, 23.96) * mm, "end": v(69.2, 23.96) * mm});
            skLineSegment(sketch, "E894", {"start": v(69.2, 23.96) * mm, "end": v(69.2, 24.96) * mm});
            skLineSegment(sketch, "E895", {"start": v(69.2, 24.96) * mm, "end": v(68.4, 24.96) * mm});
            skLineSegment(sketch, "E896", {"start": v(68.4, 24.96) * mm, "end": v(68.4, 28.06) * mm});
            skLineSegment(sketch, "E897", {"start": v(68.4, 28.06) * mm, "end": v(69.2, 28.06) * mm});
            skLineSegment(sketch, "E898", {"start": v(69.2, 28.06) * mm, "end": v(69.2, 33.86) * mm});
            skLineSegment(sketch, "E899", {"start": v(69.2, 33.86) * mm, "end": v(68.4, 33.86) * mm});
            skLineSegment(sketch, "E900", {"start": v(68.4, 33.86) * mm, "end": v(68.4, 36.96) * mm});
            skLineSegment(sketch, "E901", {"start": v(68.4, 36.96) * mm, "end": v(69.2, 36.96) * mm});
            skLineSegment(sketch, "E902", {"start": v(69.2, 36.96) * mm, "end": v(69.2, 37.96) * mm});
            skLineSegment(sketch, "E903", {"start": v(69.2, 37.96) * mm, "end": v(83.2, 37.96) * mm});
            skLineSegment(sketch, "E904", {"start": v(83.2, 37.96) * mm, "end": v(83.2, 36.96) * mm});
            skLineSegment(sketch, "E905", {"start": v(83.2, 36.96) * mm, "end": v(84, 36.96) * mm});
            skLineSegment(sketch, "E906", {"start": v(84, 36.96) * mm, "end": v(84, 33.86) * mm});
            skLineSegment(sketch, "E907", {"start": v(84, 33.86) * mm, "end": v(83.2, 33.86) * mm});
            skLineSegment(sketch, "E908", {"start": v(83.2, 33.86) * mm, "end": v(83.2, 28.06) * mm});
            skLineSegment(sketch, "E909", {"start": v(83.2, 28.06) * mm, "end": v(84, 28.06) * mm});
            skLineSegment(sketch, "E910", {"start": v(84, 28.06) * mm, "end": v(84, 24.96) * mm});
            skLineSegment(sketch, "E911", {"start": v(84, 24.96) * mm, "end": v(83.2, 24.96) * mm});
            skSolve(sketch);
        }
        {
            var Q0;
            Q0=makeQuery(id+"F0.imprint","IMPRINT",FACE,{"disambiguationData":[TD([[makeQuery(id+"F0.imprint","IMPRINT",EDGE,{"derivedFrom":sQuery(id+"F0.wireOp",EDGE,"E0")}),-1.0]])]});
            extrude(context, id + "F1", {"entities" : qUnion([Q0]), "depth" : 1.5 * mm});
        }
        {
            var Q0;
            Q0=qCreatedBy(makeId("Top.planeOp"),FACE);
            var sketch = newSketch(context, id + "F2", { "sketchPlane" : qUnion([Q0])});
            skLineSegment(sketch, "E912", {"start": v(-81.1, 0) * mm, "end": v(82.96, 0) * mm, "construction": true});
            skSolve(sketch);
        }
        {
            var Q0;
            Q0=makeQuery(id+"F1.opExtrude","SWEPT_BODY",BODY,{"disambiguationData":[OSD([sQuery(id+"F0.wireOp",EDGE,"E0"),sQuery(id+"F0.wireOp",EDGE,"E1"),sQuery(id+"F0.wireOp",EDGE,"E2"),sQuery(id+"F0.wireOp",EDGE,"E3"),sQuery(id+"F0.wireOp",EDGE,"E4"),sQuery(id+"F0.wireOp",EDGE,"E5"),sQuery(id+"F0.wireOp",EDGE,"E6"),sQuery(id+"F0.wireOp",EDGE,"E7"),sQuery(id+"F0.wireOp",EDGE,"E8"),sQuery(id+"F0.wireOp",EDGE,"E9"),sQuery(id+"F0.wireOp",EDGE,"E10"),sQuery(id+"F0.wireOp",EDGE,"E11"),sQuery(id+"F0.wireOp",EDGE,"E12"),sQuery(id+"F0.wireOp",EDGE,"E13"),sQuery(id+"F0.wireOp",EDGE,"E14"),sQuery(id+"F0.wireOp",EDGE,"E15"),sQuery(id+"F0.wireOp",EDGE,"E16"),sQuery(id+"F0.wireOp",EDGE,"E17"),sQuery(id+"F0.wireOp",EDGE,"E18"),sQuery(id+"F0.wireOp",EDGE,"E19"),sQuery(id+"F0.wireOp",EDGE,"E20"),sQuery(id+"F0.wireOp",EDGE,"E21"),sQuery(id+"F0.wireOp",EDGE,"E22"),sQuery(id+"F0.wireOp",EDGE,"E23"),sQuery(id+"F0.wireOp",EDGE,"E24"),sQuery(id+"F0.wireOp",EDGE,"E25"),sQuery(id+"F0.wireOp",EDGE,"E26"),sQuery(id+"F0.wireOp",EDGE,"E27"),sQuery(id+"F0.wireOp",EDGE,"E28"),sQuery(id+"F0.wireOp",EDGE,"E29"),sQuery(id+"F0.wireOp",EDGE,"E30"),sQuery(id+"F0.wireOp",EDGE,"E31"),sQuery(id+"F0.wireOp",EDGE,"E32"),sQuery(id+"F0.wireOp",EDGE,"E33"),sQuery(id+"F0.wireOp",EDGE,"E34"),sQuery(id+"F0.wireOp",EDGE,"E35"),sQuery(id+"F0.wireOp",EDGE,"E36"),sQuery(id+"F0.wireOp",EDGE,"E37"),sQuery(id+"F0.wireOp",EDGE,"E38"),sQuery(id+"F0.wireOp",EDGE,"E39"),sQuery(id+"F0.wireOp",EDGE,"E40"),sQuery(id+"F0.wireOp",EDGE,"E41"),sQuery(id+"F0.wireOp",EDGE,"E42"),sQuery(id+"F0.wireOp",EDGE,"E43"),sQuery(id+"F0.wireOp",EDGE,"E44"),sQuery(id+"F0.wireOp",EDGE,"E45"),sQuery(id+"F0.wireOp",EDGE,"E46"),sQuery(id+"F0.wireOp",EDGE,"E47"),sQuery(id+"F0.wireOp",EDGE,"E48"),sQuery(id+"F0.wireOp",EDGE,"E49"),sQuery(id+"F0.wireOp",EDGE,"E50"),sQuery(id+"F0.wireOp",EDGE,"E51"),sQuery(id+"F0.wireOp",EDGE,"E52"),sQuery(id+"F0.wireOp",EDGE,"E53"),sQuery(id+"F0.wireOp",EDGE,"E54"),sQuery(id+"F0.wireOp",EDGE,"E55"),sQuery(id+"F0.wireOp",EDGE,"E56"),sQuery(id+"F0.wireOp",EDGE,"E57"),sQuery(id+"F0.wireOp",EDGE,"E58"),sQuery(id+"F0.wireOp",EDGE,"E59"),sQuery(id+"F0.wireOp",EDGE,"E60"),sQuery(id+"F0.wireOp",EDGE,"E61"),sQuery(id+"F0.wireOp",EDGE,"E62"),sQuery(id+"F0.wireOp",EDGE,"E63"),sQuery(id+"F0.wireOp",EDGE,"E64"),sQuery(id+"F0.wireOp",EDGE,"E65"),sQuery(id+"F0.wireOp",EDGE,"E66"),sQuery(id+"F0.wireOp",EDGE,"E67"),sQuery(id+"F0.wireOp",EDGE,"E68"),sQuery(id+"F0.wireOp",EDGE,"E69"),sQuery(id+"F0.wireOp",EDGE,"E70"),sQuery(id+"F0.wireOp",EDGE,"E71"),sQuery(id+"F0.wireOp",EDGE,"E72"),sQuery(id+"F0.wireOp",EDGE,"E73"),sQuery(id+"F0.wireOp",EDGE,"E74"),sQuery(id+"F0.wireOp",EDGE,"E75"),sQuery(id+"F0.wireOp",EDGE,"E76"),sQuery(id+"F0.wireOp",EDGE,"E77"),sQuery(id+"F0.wireOp",EDGE,"E78"),sQuery(id+"F0.wireOp",EDGE,"E79"),sQuery(id+"F0.wireOp",EDGE,"E80"),sQuery(id+"F0.wireOp",EDGE,"E81"),sQuery(id+"F0.wireOp",EDGE,"E82"),sQuery(id+"F0.wireOp",EDGE,"E83"),sQuery(id+"F0.wireOp",EDGE,"E84"),sQuery(id+"F0.wireOp",EDGE,"E85"),sQuery(id+"F0.wireOp",EDGE,"E86"),sQuery(id+"F0.wireOp",EDGE,"E87"),sQuery(id+"F0.wireOp",EDGE,"E88"),sQuery(id+"F0.wireOp",EDGE,"E89"),sQuery(id+"F0.wireOp",EDGE,"E90"),sQuery(id+"F0.wireOp",EDGE,"E91"),sQuery(id+"F0.wireOp",EDGE,"E92"),sQuery(id+"F0.wireOp",EDGE,"E93"),sQuery(id+"F0.wireOp",EDGE,"E94"),sQuery(id+"F0.wireOp",EDGE,"E95"),sQuery(id+"F0.wireOp",EDGE,"E96"),sQuery(id+"F0.wireOp",EDGE,"E97"),sQuery(id+"F0.wireOp",EDGE,"E98"),sQuery(id+"F0.wireOp",EDGE,"E99"),sQuery(id+"F0.wireOp",EDGE,"E100"),sQuery(id+"F0.wireOp",EDGE,"E101"),sQuery(id+"F0.wireOp",EDGE,"E102"),sQuery(id+"F0.wireOp",EDGE,"E103"),sQuery(id+"F0.wireOp",EDGE,"E104"),sQuery(id+"F0.wireOp",EDGE,"E105"),sQuery(id+"F0.wireOp",EDGE,"E106"),sQuery(id+"F0.wireOp",EDGE,"E107"),sQuery(id+"F0.wireOp",EDGE,"E108"),sQuery(id+"F0.wireOp",EDGE,"E109"),sQuery(id+"F0.wireOp",EDGE,"E110"),sQuery(id+"F0.wireOp",EDGE,"E111"),sQuery(id+"F0.wireOp",EDGE,"E112"),sQuery(id+"F0.wireOp",EDGE,"E113"),sQuery(id+"F0.wireOp",EDGE,"E114"),sQuery(id+"F0.wireOp",EDGE,"E115"),sQuery(id+"F0.wireOp",EDGE,"E116"),sQuery(id+"F0.wireOp",EDGE,"E117"),sQuery(id+"F0.wireOp",EDGE,"E118"),sQuery(id+"F0.wireOp",EDGE,"E119"),sQuery(id+"F0.wireOp",EDGE,"E120"),sQuery(id+"F0.wireOp",EDGE,"E121"),sQuery(id+"F0.wireOp",EDGE,"E122"),sQuery(id+"F0.wireOp",EDGE,"E123"),sQuery(id+"F0.wireOp",EDGE,"E124"),sQuery(id+"F0.wireOp",EDGE,"E125"),sQuery(id+"F0.wireOp",EDGE,"E126"),sQuery(id+"F0.wireOp",EDGE,"E127"),sQuery(id+"F0.wireOp",EDGE,"E128"),sQuery(id+"F0.wireOp",EDGE,"E129"),sQuery(id+"F0.wireOp",EDGE,"E130"),sQuery(id+"F0.wireOp",EDGE,"E131"),sQuery(id+"F0.wireOp",EDGE,"E132"),sQuery(id+"F0.wireOp",EDGE,"E133"),sQuery(id+"F0.wireOp",EDGE,"E134"),sQuery(id+"F0.wireOp",EDGE,"E135"),sQuery(id+"F0.wireOp",EDGE,"E136"),sQuery(id+"F0.wireOp",EDGE,"E137"),sQuery(id+"F0.wireOp",EDGE,"E138"),sQuery(id+"F0.wireOp",EDGE,"E139"),sQuery(id+"F0.wireOp",EDGE,"E140"),sQuery(id+"F0.wireOp",EDGE,"E141"),sQuery(id+"F0.wireOp",EDGE,"E142"),sQuery(id+"F0.wireOp",EDGE,"E143"),sQuery(id+"F0.wireOp",EDGE,"E144"),sQuery(id+"F0.wireOp",EDGE,"E145"),sQuery(id+"F0.wireOp",EDGE,"E146"),sQuery(id+"F0.wireOp",EDGE,"E147"),sQuery(id+"F0.wireOp",EDGE,"E148"),sQuery(id+"F0.wireOp",EDGE,"E149"),sQuery(id+"F0.wireOp",EDGE,"E150"),sQuery(id+"F0.wireOp",EDGE,"E151"),sQuery(id+"F0.wireOp",EDGE,"E152"),sQuery(id+"F0.wireOp",EDGE,"E153"),sQuery(id+"F0.wireOp",EDGE,"E154"),sQuery(id+"F0.wireOp",EDGE,"E155"),sQuery(id+"F0.wireOp",EDGE,"E156"),sQuery(id+"F0.wireOp",EDGE,"E157"),sQuery(id+"F0.wireOp",EDGE,"E158"),sQuery(id+"F0.wireOp",EDGE,"E159"),sQuery(id+"F0.wireOp",EDGE,"E160"),sQuery(id+"F0.wireOp",EDGE,"E161"),sQuery(id+"F0.wireOp",EDGE,"E162"),sQuery(id+"F0.wireOp",EDGE,"E163"),sQuery(id+"F0.wireOp",EDGE,"E164"),sQuery(id+"F0.wireOp",EDGE,"E165"),sQuery(id+"F0.wireOp",EDGE,"E166"),sQuery(id+"F0.wireOp",EDGE,"E167"),sQuery(id+"F0.wireOp",EDGE,"E168"),sQuery(id+"F0.wireOp",EDGE,"E169"),sQuery(id+"F0.wireOp",EDGE,"E170"),sQuery(id+"F0.wireOp",EDGE,"E171"),sQuery(id+"F0.wireOp",EDGE,"E172"),sQuery(id+"F0.wireOp",EDGE,"E173"),sQuery(id+"F0.wireOp",EDGE,"E174"),sQuery(id+"F0.wireOp",EDGE,"E175"),sQuery(id+"F0.wireOp",EDGE,"E176"),sQuery(id+"F0.wireOp",EDGE,"E177"),sQuery(id+"F0.wireOp",EDGE,"E178"),sQuery(id+"F0.wireOp",EDGE,"E179"),sQuery(id+"F0.wireOp",EDGE,"E180"),sQuery(id+"F0.wireOp",EDGE,"E181"),sQuery(id+"F0.wireOp",EDGE,"E182"),sQuery(id+"F0.wireOp",EDGE,"E183"),sQuery(id+"F0.wireOp",EDGE,"E184"),sQuery(id+"F0.wireOp",EDGE,"E185"),sQuery(id+"F0.wireOp",EDGE,"E186"),sQuery(id+"F0.wireOp",EDGE,"E187"),sQuery(id+"F0.wireOp",EDGE,"E188"),sQuery(id+"F0.wireOp",EDGE,"E189"),sQuery(id+"F0.wireOp",EDGE,"E190"),sQuery(id+"F0.wireOp",EDGE,"E191"),sQuery(id+"F0.wireOp",EDGE,"E192"),sQuery(id+"F0.wireOp",EDGE,"E193"),sQuery(id+"F0.wireOp",EDGE,"E194"),sQuery(id+"F0.wireOp",EDGE,"E195"),sQuery(id+"F0.wireOp",EDGE,"E196"),sQuery(id+"F0.wireOp",EDGE,"E197"),sQuery(id+"F0.wireOp",EDGE,"E198"),sQuery(id+"F0.wireOp",EDGE,"E199"),sQuery(id+"F0.wireOp",EDGE,"E200"),sQuery(id+"F0.wireOp",EDGE,"E201"),sQuery(id+"F0.wireOp",EDGE,"E202"),sQuery(id+"F0.wireOp",EDGE,"E203"),sQuery(id+"F0.wireOp",EDGE,"E204"),sQuery(id+"F0.wireOp",EDGE,"E205"),sQuery(id+"F0.wireOp",EDGE,"E206"),sQuery(id+"F0.wireOp",EDGE,"E207"),sQuery(id+"F0.wireOp",EDGE,"E208"),sQuery(id+"F0.wireOp",EDGE,"E209"),sQuery(id+"F0.wireOp",EDGE,"E210"),sQuery(id+"F0.wireOp",EDGE,"E211"),sQuery(id+"F0.wireOp",EDGE,"E212"),sQuery(id+"F0.wireOp",EDGE,"E213"),sQuery(id+"F0.wireOp",EDGE,"E214"),sQuery(id+"F0.wireOp",EDGE,"E215"),sQuery(id+"F0.wireOp",EDGE,"E216"),sQuery(id+"F0.wireOp",EDGE,"E217"),sQuery(id+"F0.wireOp",EDGE,"E218"),sQuery(id+"F0.wireOp",EDGE,"E219"),sQuery(id+"F0.wireOp",EDGE,"E220"),sQuery(id+"F0.wireOp",EDGE,"E221"),sQuery(id+"F0.wireOp",EDGE,"E222"),sQuery(id+"F0.wireOp",EDGE,"E223"),sQuery(id+"F0.wireOp",EDGE,"E224"),sQuery(id+"F0.wireOp",EDGE,"E225"),sQuery(id+"F0.wireOp",EDGE,"E226"),sQuery(id+"F0.wireOp",EDGE,"E227"),sQuery(id+"F0.wireOp",EDGE,"E228"),sQuery(id+"F0.wireOp",EDGE,"E229"),sQuery(id+"F0.wireOp",EDGE,"E230"),sQuery(id+"F0.wireOp",EDGE,"E231"),sQuery(id+"F0.wireOp",EDGE,"E232"),sQuery(id+"F0.wireOp",EDGE,"E233"),sQuery(id+"F0.wireOp",EDGE,"E234"),sQuery(id+"F0.wireOp",EDGE,"E235"),sQuery(id+"F0.wireOp",EDGE,"E236"),sQuery(id+"F0.wireOp",EDGE,"E237"),sQuery(id+"F0.wireOp",EDGE,"E238"),sQuery(id+"F0.wireOp",EDGE,"E239"),sQuery(id+"F0.wireOp",EDGE,"E240"),sQuery(id+"F0.wireOp",EDGE,"E241"),sQuery(id+"F0.wireOp",EDGE,"E242"),sQuery(id+"F0.wireOp",EDGE,"E243"),sQuery(id+"F0.wireOp",EDGE,"E244"),sQuery(id+"F0.wireOp",EDGE,"E245"),sQuery(id+"F0.wireOp",EDGE,"E246"),sQuery(id+"F0.wireOp",EDGE,"E247"),sQuery(id+"F0.wireOp",EDGE,"E248"),sQuery(id+"F0.wireOp",EDGE,"E249"),sQuery(id+"F0.wireOp",EDGE,"E250"),sQuery(id+"F0.wireOp",EDGE,"E251"),sQuery(id+"F0.wireOp",EDGE,"E252"),sQuery(id+"F0.wireOp",EDGE,"E253"),sQuery(id+"F0.wireOp",EDGE,"E254"),sQuery(id+"F0.wireOp",EDGE,"E255"),sQuery(id+"F0.wireOp",EDGE,"E256"),sQuery(id+"F0.wireOp",EDGE,"E257"),sQuery(id+"F0.wireOp",EDGE,"E258"),sQuery(id+"F0.wireOp",EDGE,"E259"),sQuery(id+"F0.wireOp",EDGE,"E260"),sQuery(id+"F0.wireOp",EDGE,"E261"),sQuery(id+"F0.wireOp",EDGE,"E262"),sQuery(id+"F0.wireOp",EDGE,"E263"),sQuery(id+"F0.wireOp",EDGE,"E264"),sQuery(id+"F0.wireOp",EDGE,"E265"),sQuery(id+"F0.wireOp",EDGE,"E266"),sQuery(id+"F0.wireOp",EDGE,"E267"),sQuery(id+"F0.wireOp",EDGE,"E268"),sQuery(id+"F0.wireOp",EDGE,"E269"),sQuery(id+"F0.wireOp",EDGE,"E270"),sQuery(id+"F0.wireOp",EDGE,"E271"),sQuery(id+"F0.wireOp",EDGE,"E272"),sQuery(id+"F0.wireOp",EDGE,"E273"),sQuery(id+"F0.wireOp",EDGE,"E274"),sQuery(id+"F0.wireOp",EDGE,"E275"),sQuery(id+"F0.wireOp",EDGE,"E276"),sQuery(id+"F0.wireOp",EDGE,"E277"),sQuery(id+"F0.wireOp",EDGE,"E278"),sQuery(id+"F0.wireOp",EDGE,"E279"),sQuery(id+"F0.wireOp",EDGE,"E280"),sQuery(id+"F0.wireOp",EDGE,"E281"),sQuery(id+"F0.wireOp",EDGE,"E282"),sQuery(id+"F0.wireOp",EDGE,"E283"),sQuery(id+"F0.wireOp",EDGE,"E284"),sQuery(id+"F0.wireOp",EDGE,"E285"),sQuery(id+"F0.wireOp",EDGE,"E286"),sQuery(id+"F0.wireOp",EDGE,"E287"),sQuery(id+"F0.wireOp",EDGE,"E288"),sQuery(id+"F0.wireOp",EDGE,"E289"),sQuery(id+"F0.wireOp",EDGE,"E290"),sQuery(id+"F0.wireOp",EDGE,"E291"),sQuery(id+"F0.wireOp",EDGE,"E292"),sQuery(id+"F0.wireOp",EDGE,"E293"),sQuery(id+"F0.wireOp",EDGE,"E294"),sQuery(id+"F0.wireOp",EDGE,"E295"),sQuery(id+"F0.wireOp",EDGE,"E296"),sQuery(id+"F0.wireOp",EDGE,"E297"),sQuery(id+"F0.wireOp",EDGE,"E298"),sQuery(id+"F0.wireOp",EDGE,"E299"),sQuery(id+"F0.wireOp",EDGE,"E300"),sQuery(id+"F0.wireOp",EDGE,"E301"),sQuery(id+"F0.wireOp",EDGE,"E302"),sQuery(id+"F0.wireOp",EDGE,"E303"),sQuery(id+"F0.wireOp",EDGE,"E304"),sQuery(id+"F0.wireOp",EDGE,"E305"),sQuery(id+"F0.wireOp",EDGE,"E306"),sQuery(id+"F0.wireOp",EDGE,"E307"),sQuery(id+"F0.wireOp",EDGE,"E308"),sQuery(id+"F0.wireOp",EDGE,"E309"),sQuery(id+"F0.wireOp",EDGE,"E310"),sQuery(id+"F0.wireOp",EDGE,"E311"),sQuery(id+"F0.wireOp",EDGE,"E312"),sQuery(id+"F0.wireOp",EDGE,"E313"),sQuery(id+"F0.wireOp",EDGE,"E314"),sQuery(id+"F0.wireOp",EDGE,"E315"),sQuery(id+"F0.wireOp",EDGE,"E316"),sQuery(id+"F0.wireOp",EDGE,"E317"),sQuery(id+"F0.wireOp",EDGE,"E318"),sQuery(id+"F0.wireOp",EDGE,"E319"),sQuery(id+"F0.wireOp",EDGE,"E320"),sQuery(id+"F0.wireOp",EDGE,"E321"),sQuery(id+"F0.wireOp",EDGE,"E322"),sQuery(id+"F0.wireOp",EDGE,"E323"),sQuery(id+"F0.wireOp",EDGE,"E324"),sQuery(id+"F0.wireOp",EDGE,"E325"),sQuery(id+"F0.wireOp",EDGE,"E326"),sQuery(id+"F0.wireOp",EDGE,"E327"),sQuery(id+"F0.wireOp",EDGE,"E328"),sQuery(id+"F0.wireOp",EDGE,"E329"),sQuery(id+"F0.wireOp",EDGE,"E330"),sQuery(id+"F0.wireOp",EDGE,"E331"),sQuery(id+"F0.wireOp",EDGE,"E332"),sQuery(id+"F0.wireOp",EDGE,"E333"),sQuery(id+"F0.wireOp",EDGE,"E334"),sQuery(id+"F0.wireOp",EDGE,"E335"),sQuery(id+"F0.wireOp",EDGE,"E336"),sQuery(id+"F0.wireOp",EDGE,"E337"),sQuery(id+"F0.wireOp",EDGE,"E338"),sQuery(id+"F0.wireOp",EDGE,"E339"),sQuery(id+"F0.wireOp",EDGE,"E340"),sQuery(id+"F0.wireOp",EDGE,"E341"),sQuery(id+"F0.wireOp",EDGE,"E342"),sQuery(id+"F0.wireOp",EDGE,"E343"),sQuery(id+"F0.wireOp",EDGE,"E344"),sQuery(id+"F0.wireOp",EDGE,"E345"),sQuery(id+"F0.wireOp",EDGE,"E346"),sQuery(id+"F0.wireOp",EDGE,"E347"),sQuery(id+"F0.wireOp",EDGE,"E348"),sQuery(id+"F0.wireOp",EDGE,"E349"),sQuery(id+"F0.wireOp",EDGE,"E350"),sQuery(id+"F0.wireOp",EDGE,"E351"),sQuery(id+"F0.wireOp",EDGE,"E352"),sQuery(id+"F0.wireOp",EDGE,"E353"),sQuery(id+"F0.wireOp",EDGE,"E354"),sQuery(id+"F0.wireOp",EDGE,"E355"),sQuery(id+"F0.wireOp",EDGE,"E356"),sQuery(id+"F0.wireOp",EDGE,"E357"),sQuery(id+"F0.wireOp",EDGE,"E358"),sQuery(id+"F0.wireOp",EDGE,"E359"),sQuery(id+"F0.wireOp",EDGE,"E360"),sQuery(id+"F0.wireOp",EDGE,"E361"),sQuery(id+"F0.wireOp",EDGE,"E362"),sQuery(id+"F0.wireOp",EDGE,"E363"),sQuery(id+"F0.wireOp",EDGE,"E364"),sQuery(id+"F0.wireOp",EDGE,"E365"),sQuery(id+"F0.wireOp",EDGE,"E366"),sQuery(id+"F0.wireOp",EDGE,"E367"),sQuery(id+"F0.wireOp",EDGE,"E368"),sQuery(id+"F0.wireOp",EDGE,"E369"),sQuery(id+"F0.wireOp",EDGE,"E370"),sQuery(id+"F0.wireOp",EDGE,"E371"),sQuery(id+"F0.wireOp",EDGE,"E372"),sQuery(id+"F0.wireOp",EDGE,"E373"),sQuery(id+"F0.wireOp",EDGE,"E374"),sQuery(id+"F0.wireOp",EDGE,"E375"),sQuery(id+"F0.wireOp",EDGE,"E376"),sQuery(id+"F0.wireOp",EDGE,"E377"),sQuery(id+"F0.wireOp",EDGE,"E378"),sQuery(id+"F0.wireOp",EDGE,"E379"),sQuery(id+"F0.wireOp",EDGE,"E380"),sQuery(id+"F0.wireOp",EDGE,"E381"),sQuery(id+"F0.wireOp",EDGE,"E382"),sQuery(id+"F0.wireOp",EDGE,"E383"),sQuery(id+"F0.wireOp",EDGE,"E384"),sQuery(id+"F0.wireOp",EDGE,"E385"),sQuery(id+"F0.wireOp",EDGE,"E386"),sQuery(id+"F0.wireOp",EDGE,"E387"),sQuery(id+"F0.wireOp",EDGE,"E388"),sQuery(id+"F0.wireOp",EDGE,"E389"),sQuery(id+"F0.wireOp",EDGE,"E390"),sQuery(id+"F0.wireOp",EDGE,"E391"),sQuery(id+"F0.wireOp",EDGE,"E392"),sQuery(id+"F0.wireOp",EDGE,"E393"),sQuery(id+"F0.wireOp",EDGE,"E394"),sQuery(id+"F0.wireOp",EDGE,"E395"),sQuery(id+"F0.wireOp",EDGE,"E396"),sQuery(id+"F0.wireOp",EDGE,"E397"),sQuery(id+"F0.wireOp",EDGE,"E398"),sQuery(id+"F0.wireOp",EDGE,"E399"),sQuery(id+"F0.wireOp",EDGE,"E400"),sQuery(id+"F0.wireOp",EDGE,"E401"),sQuery(id+"F0.wireOp",EDGE,"E402"),sQuery(id+"F0.wireOp",EDGE,"E403"),sQuery(id+"F0.wireOp",EDGE,"E404"),sQuery(id+"F0.wireOp",EDGE,"E405"),sQuery(id+"F0.wireOp",EDGE,"E406"),sQuery(id+"F0.wireOp",EDGE,"E407"),sQuery(id+"F0.wireOp",EDGE,"E408"),sQuery(id+"F0.wireOp",EDGE,"E409"),sQuery(id+"F0.wireOp",EDGE,"E410"),sQuery(id+"F0.wireOp",EDGE,"E411"),sQuery(id+"F0.wireOp",EDGE,"E412"),sQuery(id+"F0.wireOp",EDGE,"E413"),sQuery(id+"F0.wireOp",EDGE,"E414"),sQuery(id+"F0.wireOp",EDGE,"E415"),sQuery(id+"F0.wireOp",EDGE,"E416"),sQuery(id+"F0.wireOp",EDGE,"E417"),sQuery(id+"F0.wireOp",EDGE,"E418"),sQuery(id+"F0.wireOp",EDGE,"E419"),sQuery(id+"F0.wireOp",EDGE,"E420"),sQuery(id+"F0.wireOp",EDGE,"E421"),sQuery(id+"F0.wireOp",EDGE,"E422"),sQuery(id+"F0.wireOp",EDGE,"E423"),sQuery(id+"F0.wireOp",EDGE,"E424"),sQuery(id+"F0.wireOp",EDGE,"E425"),sQuery(id+"F0.wireOp",EDGE,"E426"),sQuery(id+"F0.wireOp",EDGE,"E427"),sQuery(id+"F0.wireOp",EDGE,"E428"),sQuery(id+"F0.wireOp",EDGE,"E429"),sQuery(id+"F0.wireOp",EDGE,"E430"),sQuery(id+"F0.wireOp",EDGE,"E431"),sQuery(id+"F0.wireOp",EDGE,"E432"),sQuery(id+"F0.wireOp",EDGE,"E433"),sQuery(id+"F0.wireOp",EDGE,"E434"),sQuery(id+"F0.wireOp",EDGE,"E435"),sQuery(id+"F0.wireOp",EDGE,"E436"),sQuery(id+"F0.wireOp",EDGE,"E437"),sQuery(id+"F0.wireOp",EDGE,"E438"),sQuery(id+"F0.wireOp",EDGE,"E439"),sQuery(id+"F0.wireOp",EDGE,"E440"),sQuery(id+"F0.wireOp",EDGE,"E441"),sQuery(id+"F0.wireOp",EDGE,"E442"),sQuery(id+"F0.wireOp",EDGE,"E443"),sQuery(id+"F0.wireOp",EDGE,"E444"),sQuery(id+"F0.wireOp",EDGE,"E445"),sQuery(id+"F0.wireOp",EDGE,"E446"),sQuery(id+"F0.wireOp",EDGE,"E447"),sQuery(id+"F0.wireOp",EDGE,"E448"),sQuery(id+"F0.wireOp",EDGE,"E449"),sQuery(id+"F0.wireOp",EDGE,"E450"),sQuery(id+"F0.wireOp",EDGE,"E451"),sQuery(id+"F0.wireOp",EDGE,"E452"),sQuery(id+"F0.wireOp",EDGE,"E453"),sQuery(id+"F0.wireOp",EDGE,"E454"),sQuery(id+"F0.wireOp",EDGE,"E455"),sQuery(id+"F0.wireOp",EDGE,"E456"),sQuery(id+"F0.wireOp",EDGE,"E457"),sQuery(id+"F0.wireOp",EDGE,"E458"),sQuery(id+"F0.wireOp",EDGE,"E459"),sQuery(id+"F0.wireOp",EDGE,"E460"),sQuery(id+"F0.wireOp",EDGE,"E461"),sQuery(id+"F0.wireOp",EDGE,"E462"),sQuery(id+"F0.wireOp",EDGE,"E463"),sQuery(id+"F0.wireOp",EDGE,"E464"),sQuery(id+"F0.wireOp",EDGE,"E465"),sQuery(id+"F0.wireOp",EDGE,"E466"),sQuery(id+"F0.wireOp",EDGE,"E467"),sQuery(id+"F0.wireOp",EDGE,"E468"),sQuery(id+"F0.wireOp",EDGE,"E469"),sQuery(id+"F0.wireOp",EDGE,"E470"),sQuery(id+"F0.wireOp",EDGE,"E471"),sQuery(id+"F0.wireOp",EDGE,"E472"),sQuery(id+"F0.wireOp",EDGE,"E473"),sQuery(id+"F0.wireOp",EDGE,"E474"),sQuery(id+"F0.wireOp",EDGE,"E475"),sQuery(id+"F0.wireOp",EDGE,"E476"),sQuery(id+"F0.wireOp",EDGE,"E477"),sQuery(id+"F0.wireOp",EDGE,"E478"),sQuery(id+"F0.wireOp",EDGE,"E479"),sQuery(id+"F0.wireOp",EDGE,"E480"),sQuery(id+"F0.wireOp",EDGE,"E481"),sQuery(id+"F0.wireOp",EDGE,"E482"),sQuery(id+"F0.wireOp",EDGE,"E483"),sQuery(id+"F0.wireOp",EDGE,"E484"),sQuery(id+"F0.wireOp",EDGE,"E485"),sQuery(id+"F0.wireOp",EDGE,"E486"),sQuery(id+"F0.wireOp",EDGE,"E487"),sQuery(id+"F0.wireOp",EDGE,"E488"),sQuery(id+"F0.wireOp",EDGE,"E489"),sQuery(id+"F0.wireOp",EDGE,"E490"),sQuery(id+"F0.wireOp",EDGE,"E491"),sQuery(id+"F0.wireOp",EDGE,"E492"),sQuery(id+"F0.wireOp",EDGE,"E493"),sQuery(id+"F0.wireOp",EDGE,"E494"),sQuery(id+"F0.wireOp",EDGE,"E495"),sQuery(id+"F0.wireOp",EDGE,"E496"),sQuery(id+"F0.wireOp",EDGE,"E497"),sQuery(id+"F0.wireOp",EDGE,"E498"),sQuery(id+"F0.wireOp",EDGE,"E499"),sQuery(id+"F0.wireOp",EDGE,"E500"),sQuery(id+"F0.wireOp",EDGE,"E501"),sQuery(id+"F0.wireOp",EDGE,"E502"),sQuery(id+"F0.wireOp",EDGE,"E503"),sQuery(id+"F0.wireOp",EDGE,"E504"),sQuery(id+"F0.wireOp",EDGE,"E505"),sQuery(id+"F0.wireOp",EDGE,"E506"),sQuery(id+"F0.wireOp",EDGE,"E507"),sQuery(id+"F0.wireOp",EDGE,"E508"),sQuery(id+"F0.wireOp",EDGE,"E509"),sQuery(id+"F0.wireOp",EDGE,"E510"),sQuery(id+"F0.wireOp",EDGE,"E511"),sQuery(id+"F0.wireOp",EDGE,"E512"),sQuery(id+"F0.wireOp",EDGE,"E513"),sQuery(id+"F0.wireOp",EDGE,"E514"),sQuery(id+"F0.wireOp",EDGE,"E515"),sQuery(id+"F0.wireOp",EDGE,"E516"),sQuery(id+"F0.wireOp",EDGE,"E517"),sQuery(id+"F0.wireOp",EDGE,"E518"),sQuery(id+"F0.wireOp",EDGE,"E519"),sQuery(id+"F0.wireOp",EDGE,"E520"),sQuery(id+"F0.wireOp",EDGE,"E521"),sQuery(id+"F0.wireOp",EDGE,"E522"),sQuery(id+"F0.wireOp",EDGE,"E523"),sQuery(id+"F0.wireOp",EDGE,"E524"),sQuery(id+"F0.wireOp",EDGE,"E525"),sQuery(id+"F0.wireOp",EDGE,"E526"),sQuery(id+"F0.wireOp",EDGE,"E527"),sQuery(id+"F0.wireOp",EDGE,"E528"),sQuery(id+"F0.wireOp",EDGE,"E529"),sQuery(id+"F0.wireOp",EDGE,"E530"),sQuery(id+"F0.wireOp",EDGE,"E531"),sQuery(id+"F0.wireOp",EDGE,"E532"),sQuery(id+"F0.wireOp",EDGE,"E533"),sQuery(id+"F0.wireOp",EDGE,"E534"),sQuery(id+"F0.wireOp",EDGE,"E535"),sQuery(id+"F0.wireOp",EDGE,"E536"),sQuery(id+"F0.wireOp",EDGE,"E537"),sQuery(id+"F0.wireOp",EDGE,"E538"),sQuery(id+"F0.wireOp",EDGE,"E539"),sQuery(id+"F0.wireOp",EDGE,"E540"),sQuery(id+"F0.wireOp",EDGE,"E541"),sQuery(id+"F0.wireOp",EDGE,"E542"),sQuery(id+"F0.wireOp",EDGE,"E543"),sQuery(id+"F0.wireOp",EDGE,"E544"),sQuery(id+"F0.wireOp",EDGE,"E545"),sQuery(id+"F0.wireOp",EDGE,"E546"),sQuery(id+"F0.wireOp",EDGE,"E547"),sQuery(id+"F0.wireOp",EDGE,"E548"),sQuery(id+"F0.wireOp",EDGE,"E549"),sQuery(id+"F0.wireOp",EDGE,"E550"),sQuery(id+"F0.wireOp",EDGE,"E551"),sQuery(id+"F0.wireOp",EDGE,"E552"),sQuery(id+"F0.wireOp",EDGE,"E553"),sQuery(id+"F0.wireOp",EDGE,"E554"),sQuery(id+"F0.wireOp",EDGE,"E555"),sQuery(id+"F0.wireOp",EDGE,"E556"),sQuery(id+"F0.wireOp",EDGE,"E557"),sQuery(id+"F0.wireOp",EDGE,"E558"),sQuery(id+"F0.wireOp",EDGE,"E559"),sQuery(id+"F0.wireOp",EDGE,"E560"),sQuery(id+"F0.wireOp",EDGE,"E561"),sQuery(id+"F0.wireOp",EDGE,"E562"),sQuery(id+"F0.wireOp",EDGE,"E563"),sQuery(id+"F0.wireOp",EDGE,"E564"),sQuery(id+"F0.wireOp",EDGE,"E565"),sQuery(id+"F0.wireOp",EDGE,"E566"),sQuery(id+"F0.wireOp",EDGE,"E567"),sQuery(id+"F0.wireOp",EDGE,"E568"),sQuery(id+"F0.wireOp",EDGE,"E569"),sQuery(id+"F0.wireOp",EDGE,"E570"),sQuery(id+"F0.wireOp",EDGE,"E571"),sQuery(id+"F0.wireOp",EDGE,"E572"),sQuery(id+"F0.wireOp",EDGE,"E573"),sQuery(id+"F0.wireOp",EDGE,"E574"),sQuery(id+"F0.wireOp",EDGE,"E575"),sQuery(id+"F0.wireOp",EDGE,"E576"),sQuery(id+"F0.wireOp",EDGE,"E577"),sQuery(id+"F0.wireOp",EDGE,"E578"),sQuery(id+"F0.wireOp",EDGE,"E579"),sQuery(id+"F0.wireOp",EDGE,"E580"),sQuery(id+"F0.wireOp",EDGE,"E581"),sQuery(id+"F0.wireOp",EDGE,"E582"),sQuery(id+"F0.wireOp",EDGE,"E583"),sQuery(id+"F0.wireOp",EDGE,"E584"),sQuery(id+"F0.wireOp",EDGE,"E585"),sQuery(id+"F0.wireOp",EDGE,"E586"),sQuery(id+"F0.wireOp",EDGE,"E587"),sQuery(id+"F0.wireOp",EDGE,"E588"),sQuery(id+"F0.wireOp",EDGE,"E589"),sQuery(id+"F0.wireOp",EDGE,"E590"),sQuery(id+"F0.wireOp",EDGE,"E591"),sQuery(id+"F0.wireOp",EDGE,"E592"),sQuery(id+"F0.wireOp",EDGE,"E593"),sQuery(id+"F0.wireOp",EDGE,"E594"),sQuery(id+"F0.wireOp",EDGE,"E595"),sQuery(id+"F0.wireOp",EDGE,"E596"),sQuery(id+"F0.wireOp",EDGE,"E597"),sQuery(id+"F0.wireOp",EDGE,"E598"),sQuery(id+"F0.wireOp",EDGE,"E599"),sQuery(id+"F0.wireOp",EDGE,"E600"),sQuery(id+"F0.wireOp",EDGE,"E601"),sQuery(id+"F0.wireOp",EDGE,"E602"),sQuery(id+"F0.wireOp",EDGE,"E603"),sQuery(id+"F0.wireOp",EDGE,"E604"),sQuery(id+"F0.wireOp",EDGE,"E605"),sQuery(id+"F0.wireOp",EDGE,"E606"),sQuery(id+"F0.wireOp",EDGE,"E607"),sQuery(id+"F0.wireOp",EDGE,"E608"),sQuery(id+"F0.wireOp",EDGE,"E609"),sQuery(id+"F0.wireOp",EDGE,"E610"),sQuery(id+"F0.wireOp",EDGE,"E611"),sQuery(id+"F0.wireOp",EDGE,"E612"),sQuery(id+"F0.wireOp",EDGE,"E613"),sQuery(id+"F0.wireOp",EDGE,"E614"),sQuery(id+"F0.wireOp",EDGE,"E615"),sQuery(id+"F0.wireOp",EDGE,"E616"),sQuery(id+"F0.wireOp",EDGE,"E617"),sQuery(id+"F0.wireOp",EDGE,"E618"),sQuery(id+"F0.wireOp",EDGE,"E619"),sQuery(id+"F0.wireOp",EDGE,"E620"),sQuery(id+"F0.wireOp",EDGE,"E621"),sQuery(id+"F0.wireOp",EDGE,"E622"),sQuery(id+"F0.wireOp",EDGE,"E623"),sQuery(id+"F0.wireOp",EDGE,"E624"),sQuery(id+"F0.wireOp",EDGE,"E625"),sQuery(id+"F0.wireOp",EDGE,"E626"),sQuery(id+"F0.wireOp",EDGE,"E627"),sQuery(id+"F0.wireOp",EDGE,"E628"),sQuery(id+"F0.wireOp",EDGE,"E629"),sQuery(id+"F0.wireOp",EDGE,"E630"),sQuery(id+"F0.wireOp",EDGE,"E631"),sQuery(id+"F0.wireOp",EDGE,"E632"),sQuery(id+"F0.wireOp",EDGE,"E633"),sQuery(id+"F0.wireOp",EDGE,"E634"),sQuery(id+"F0.wireOp",EDGE,"E635"),sQuery(id+"F0.wireOp",EDGE,"E636"),sQuery(id+"F0.wireOp",EDGE,"E637"),sQuery(id+"F0.wireOp",EDGE,"E638"),sQuery(id+"F0.wireOp",EDGE,"E639"),sQuery(id+"F0.wireOp",EDGE,"E640"),sQuery(id+"F0.wireOp",EDGE,"E641"),sQuery(id+"F0.wireOp",EDGE,"E642"),sQuery(id+"F0.wireOp",EDGE,"E643"),sQuery(id+"F0.wireOp",EDGE,"E644"),sQuery(id+"F0.wireOp",EDGE,"E645"),sQuery(id+"F0.wireOp",EDGE,"E646"),sQuery(id+"F0.wireOp",EDGE,"E647"),sQuery(id+"F0.wireOp",EDGE,"E648"),sQuery(id+"F0.wireOp",EDGE,"E649"),sQuery(id+"F0.wireOp",EDGE,"E650"),sQuery(id+"F0.wireOp",EDGE,"E651"),sQuery(id+"F0.wireOp",EDGE,"E652"),sQuery(id+"F0.wireOp",EDGE,"E653"),sQuery(id+"F0.wireOp",EDGE,"E654"),sQuery(id+"F0.wireOp",EDGE,"E655"),sQuery(id+"F0.wireOp",EDGE,"E656"),sQuery(id+"F0.wireOp",EDGE,"E657"),sQuery(id+"F0.wireOp",EDGE,"E658"),sQuery(id+"F0.wireOp",EDGE,"E659"),sQuery(id+"F0.wireOp",EDGE,"E660"),sQuery(id+"F0.wireOp",EDGE,"E661"),sQuery(id+"F0.wireOp",EDGE,"E662"),sQuery(id+"F0.wireOp",EDGE,"E663"),sQuery(id+"F0.wireOp",EDGE,"E664"),sQuery(id+"F0.wireOp",EDGE,"E665"),sQuery(id+"F0.wireOp",EDGE,"E666"),sQuery(id+"F0.wireOp",EDGE,"E667"),sQuery(id+"F0.wireOp",EDGE,"E668"),sQuery(id+"F0.wireOp",EDGE,"E669"),sQuery(id+"F0.wireOp",EDGE,"E670"),sQuery(id+"F0.wireOp",EDGE,"E671"),sQuery(id+"F0.wireOp",EDGE,"E672"),sQuery(id+"F0.wireOp",EDGE,"E673"),sQuery(id+"F0.wireOp",EDGE,"E674"),sQuery(id+"F0.wireOp",EDGE,"E675"),sQuery(id+"F0.wireOp",EDGE,"E676"),sQuery(id+"F0.wireOp",EDGE,"E677"),sQuery(id+"F0.wireOp",EDGE,"E678"),sQuery(id+"F0.wireOp",EDGE,"E679"),sQuery(id+"F0.wireOp",EDGE,"E680"),sQuery(id+"F0.wireOp",EDGE,"E681"),sQuery(id+"F0.wireOp",EDGE,"E682"),sQuery(id+"F0.wireOp",EDGE,"E683"),sQuery(id+"F0.wireOp",EDGE,"E684"),sQuery(id+"F0.wireOp",EDGE,"E685"),sQuery(id+"F0.wireOp",EDGE,"E686"),sQuery(id+"F0.wireOp",EDGE,"E687"),sQuery(id+"F0.wireOp",EDGE,"E688"),sQuery(id+"F0.wireOp",EDGE,"E689"),sQuery(id+"F0.wireOp",EDGE,"E690"),sQuery(id+"F0.wireOp",EDGE,"E691"),sQuery(id+"F0.wireOp",EDGE,"E692"),sQuery(id+"F0.wireOp",EDGE,"E693"),sQuery(id+"F0.wireOp",EDGE,"E694"),sQuery(id+"F0.wireOp",EDGE,"E695"),sQuery(id+"F0.wireOp",EDGE,"E696"),sQuery(id+"F0.wireOp",EDGE,"E697"),sQuery(id+"F0.wireOp",EDGE,"E698"),sQuery(id+"F0.wireOp",EDGE,"E699"),sQuery(id+"F0.wireOp",EDGE,"E700"),sQuery(id+"F0.wireOp",EDGE,"E701"),sQuery(id+"F0.wireOp",EDGE,"E702"),sQuery(id+"F0.wireOp",EDGE,"E703"),sQuery(id+"F0.wireOp",EDGE,"E704"),sQuery(id+"F0.wireOp",EDGE,"E705"),sQuery(id+"F0.wireOp",EDGE,"E706"),sQuery(id+"F0.wireOp",EDGE,"E707"),sQuery(id+"F0.wireOp",EDGE,"E708"),sQuery(id+"F0.wireOp",EDGE,"E709"),sQuery(id+"F0.wireOp",EDGE,"E710"),sQuery(id+"F0.wireOp",EDGE,"E711"),sQuery(id+"F0.wireOp",EDGE,"E712"),sQuery(id+"F0.wireOp",EDGE,"E713"),sQuery(id+"F0.wireOp",EDGE,"E714"),sQuery(id+"F0.wireOp",EDGE,"E715"),sQuery(id+"F0.wireOp",EDGE,"E716"),sQuery(id+"F0.wireOp",EDGE,"E717"),sQuery(id+"F0.wireOp",EDGE,"E718"),sQuery(id+"F0.wireOp",EDGE,"E719"),sQuery(id+"F0.wireOp",EDGE,"E720"),sQuery(id+"F0.wireOp",EDGE,"E721"),sQuery(id+"F0.wireOp",EDGE,"E722"),sQuery(id+"F0.wireOp",EDGE,"E723"),sQuery(id+"F0.wireOp",EDGE,"E724"),sQuery(id+"F0.wireOp",EDGE,"E725"),sQuery(id+"F0.wireOp",EDGE,"E726"),sQuery(id+"F0.wireOp",EDGE,"E727"),sQuery(id+"F0.wireOp",EDGE,"E728"),sQuery(id+"F0.wireOp",EDGE,"E729"),sQuery(id+"F0.wireOp",EDGE,"E730"),sQuery(id+"F0.wireOp",EDGE,"E731"),sQuery(id+"F0.wireOp",EDGE,"E732"),sQuery(id+"F0.wireOp",EDGE,"E733"),sQuery(id+"F0.wireOp",EDGE,"E734"),sQuery(id+"F0.wireOp",EDGE,"E735"),sQuery(id+"F0.wireOp",EDGE,"E736"),sQuery(id+"F0.wireOp",EDGE,"E737"),sQuery(id+"F0.wireOp",EDGE,"E738"),sQuery(id+"F0.wireOp",EDGE,"E739"),sQuery(id+"F0.wireOp",EDGE,"E740"),sQuery(id+"F0.wireOp",EDGE,"E741"),sQuery(id+"F0.wireOp",EDGE,"E742"),sQuery(id+"F0.wireOp",EDGE,"E743"),sQuery(id+"F0.wireOp",EDGE,"E744"),sQuery(id+"F0.wireOp",EDGE,"E745"),sQuery(id+"F0.wireOp",EDGE,"E746"),sQuery(id+"F0.wireOp",EDGE,"E747"),sQuery(id+"F0.wireOp",EDGE,"E748"),sQuery(id+"F0.wireOp",EDGE,"E749"),sQuery(id+"F0.wireOp",EDGE,"E750"),sQuery(id+"F0.wireOp",EDGE,"E751"),sQuery(id+"F0.wireOp",EDGE,"E752"),sQuery(id+"F0.wireOp",EDGE,"E753"),sQuery(id+"F0.wireOp",EDGE,"E754"),sQuery(id+"F0.wireOp",EDGE,"E755"),sQuery(id+"F0.wireOp",EDGE,"E756"),sQuery(id+"F0.wireOp",EDGE,"E757"),sQuery(id+"F0.wireOp",EDGE,"E758"),sQuery(id+"F0.wireOp",EDGE,"E759"),sQuery(id+"F0.wireOp",EDGE,"E760"),sQuery(id+"F0.wireOp",EDGE,"E761"),sQuery(id+"F0.wireOp",EDGE,"E762"),sQuery(id+"F0.wireOp",EDGE,"E763"),sQuery(id+"F0.wireOp",EDGE,"E764"),sQuery(id+"F0.wireOp",EDGE,"E765"),sQuery(id+"F0.wireOp",EDGE,"E766"),sQuery(id+"F0.wireOp",EDGE,"E767"),sQuery(id+"F0.wireOp",EDGE,"E768"),sQuery(id+"F0.wireOp",EDGE,"E769"),sQuery(id+"F0.wireOp",EDGE,"E770"),sQuery(id+"F0.wireOp",EDGE,"E771"),sQuery(id+"F0.wireOp",EDGE,"E772"),sQuery(id+"F0.wireOp",EDGE,"E773"),sQuery(id+"F0.wireOp",EDGE,"E774"),sQuery(id+"F0.wireOp",EDGE,"E775"),sQuery(id+"F0.wireOp",EDGE,"E776"),sQuery(id+"F0.wireOp",EDGE,"E777"),sQuery(id+"F0.wireOp",EDGE,"E778"),sQuery(id+"F0.wireOp",EDGE,"E779"),sQuery(id+"F0.wireOp",EDGE,"E780"),sQuery(id+"F0.wireOp",EDGE,"E781"),sQuery(id+"F0.wireOp",EDGE,"E782"),sQuery(id+"F0.wireOp",EDGE,"E783"),sQuery(id+"F0.wireOp",EDGE,"E784"),sQuery(id+"F0.wireOp",EDGE,"E785"),sQuery(id+"F0.wireOp",EDGE,"E786"),sQuery(id+"F0.wireOp",EDGE,"E787"),sQuery(id+"F0.wireOp",EDGE,"E788"),sQuery(id+"F0.wireOp",EDGE,"E789"),sQuery(id+"F0.wireOp",EDGE,"E790"),sQuery(id+"F0.wireOp",EDGE,"E791"),sQuery(id+"F0.wireOp",EDGE,"E792"),sQuery(id+"F0.wireOp",EDGE,"E793"),sQuery(id+"F0.wireOp",EDGE,"E794"),sQuery(id+"F0.wireOp",EDGE,"E795"),sQuery(id+"F0.wireOp",EDGE,"E796"),sQuery(id+"F0.wireOp",EDGE,"E797"),sQuery(id+"F0.wireOp",EDGE,"E798"),sQuery(id+"F0.wireOp",EDGE,"E799"),sQuery(id+"F0.wireOp",EDGE,"E800"),sQuery(id+"F0.wireOp",EDGE,"E801"),sQuery(id+"F0.wireOp",EDGE,"E802"),sQuery(id+"F0.wireOp",EDGE,"E803"),sQuery(id+"F0.wireOp",EDGE,"E804"),sQuery(id+"F0.wireOp",EDGE,"E805"),sQuery(id+"F0.wireOp",EDGE,"E806"),sQuery(id+"F0.wireOp",EDGE,"E807"),sQuery(id+"F0.wireOp",EDGE,"E808"),sQuery(id+"F0.wireOp",EDGE,"E809"),sQuery(id+"F0.wireOp",EDGE,"E810"),sQuery(id+"F0.wireOp",EDGE,"E811"),sQuery(id+"F0.wireOp",EDGE,"E812"),sQuery(id+"F0.wireOp",EDGE,"E813"),sQuery(id+"F0.wireOp",EDGE,"E814"),sQuery(id+"F0.wireOp",EDGE,"E815"),sQuery(id+"F0.wireOp",EDGE,"E816"),sQuery(id+"F0.wireOp",EDGE,"E817"),sQuery(id+"F0.wireOp",EDGE,"E818"),sQuery(id+"F0.wireOp",EDGE,"E819"),sQuery(id+"F0.wireOp",EDGE,"E820"),sQuery(id+"F0.wireOp",EDGE,"E821"),sQuery(id+"F0.wireOp",EDGE,"E822"),sQuery(id+"F0.wireOp",EDGE,"E823"),sQuery(id+"F0.wireOp",EDGE,"E824"),sQuery(id+"F0.wireOp",EDGE,"E825"),sQuery(id+"F0.wireOp",EDGE,"E826"),sQuery(id+"F0.wireOp",EDGE,"E827"),sQuery(id+"F0.wireOp",EDGE,"E828"),sQuery(id+"F0.wireOp",EDGE,"E829"),sQuery(id+"F0.wireOp",EDGE,"E830"),sQuery(id+"F0.wireOp",EDGE,"E831"),sQuery(id+"F0.wireOp",EDGE,"E832"),sQuery(id+"F0.wireOp",EDGE,"E833"),sQuery(id+"F0.wireOp",EDGE,"E834"),sQuery(id+"F0.wireOp",EDGE,"E835"),sQuery(id+"F0.wireOp",EDGE,"E836"),sQuery(id+"F0.wireOp",EDGE,"E837"),sQuery(id+"F0.wireOp",EDGE,"E838"),sQuery(id+"F0.wireOp",EDGE,"E839"),sQuery(id+"F0.wireOp",EDGE,"E840"),sQuery(id+"F0.wireOp",EDGE,"E841"),sQuery(id+"F0.wireOp",EDGE,"E842"),sQuery(id+"F0.wireOp",EDGE,"E843"),sQuery(id+"F0.wireOp",EDGE,"E844"),sQuery(id+"F0.wireOp",EDGE,"E845"),sQuery(id+"F0.wireOp",EDGE,"E846"),sQuery(id+"F0.wireOp",EDGE,"E847"),sQuery(id+"F0.wireOp",EDGE,"E848"),sQuery(id+"F0.wireOp",EDGE,"E849"),sQuery(id+"F0.wireOp",EDGE,"E850"),sQuery(id+"F0.wireOp",EDGE,"E851"),sQuery(id+"F0.wireOp",EDGE,"E852"),sQuery(id+"F0.wireOp",EDGE,"E853"),sQuery(id+"F0.wireOp",EDGE,"E854"),sQuery(id+"F0.wireOp",EDGE,"E855"),sQuery(id+"F0.wireOp",EDGE,"E856"),sQuery(id+"F0.wireOp",EDGE,"E857"),sQuery(id+"F0.wireOp",EDGE,"E858"),sQuery(id+"F0.wireOp",EDGE,"E859"),sQuery(id+"F0.wireOp",EDGE,"E860"),sQuery(id+"F0.wireOp",EDGE,"E861"),sQuery(id+"F0.wireOp",EDGE,"E862"),sQuery(id+"F0.wireOp",EDGE,"E863"),sQuery(id+"F0.wireOp",EDGE,"E864"),sQuery(id+"F0.wireOp",EDGE,"E865"),sQuery(id+"F0.wireOp",EDGE,"E866"),sQuery(id+"F0.wireOp",EDGE,"E867"),sQuery(id+"F0.wireOp",EDGE,"E868"),sQuery(id+"F0.wireOp",EDGE,"E869"),sQuery(id+"F0.wireOp",EDGE,"E870"),sQuery(id+"F0.wireOp",EDGE,"E871"),sQuery(id+"F0.wireOp",EDGE,"E872"),sQuery(id+"F0.wireOp",EDGE,"E873"),sQuery(id+"F0.wireOp",EDGE,"E874"),sQuery(id+"F0.wireOp",EDGE,"E875"),sQuery(id+"F0.wireOp",EDGE,"E876"),sQuery(id+"F0.wireOp",EDGE,"E877"),sQuery(id+"F0.wireOp",EDGE,"E878"),sQuery(id+"F0.wireOp",EDGE,"E879"),sQuery(id+"F0.wireOp",EDGE,"E880"),sQuery(id+"F0.wireOp",EDGE,"E881"),sQuery(id+"F0.wireOp",EDGE,"E882"),sQuery(id+"F0.wireOp",EDGE,"E883"),sQuery(id+"F0.wireOp",EDGE,"E884"),sQuery(id+"F0.wireOp",EDGE,"E885"),sQuery(id+"F0.wireOp",EDGE,"E886"),sQuery(id+"F0.wireOp",EDGE,"E887"),sQuery(id+"F0.wireOp",EDGE,"E888"),sQuery(id+"F0.wireOp",EDGE,"E889"),sQuery(id+"F0.wireOp",EDGE,"E890"),sQuery(id+"F0.wireOp",EDGE,"E891"),sQuery(id+"F0.wireOp",EDGE,"E892"),sQuery(id+"F0.wireOp",EDGE,"E893"),sQuery(id+"F0.wireOp",EDGE,"E894"),sQuery(id+"F0.wireOp",EDGE,"E895"),sQuery(id+"F0.wireOp",EDGE,"E896"),sQuery(id+"F0.wireOp",EDGE,"E897"),sQuery(id+"F0.wireOp",EDGE,"E898"),sQuery(id+"F0.wireOp",EDGE,"E899"),sQuery(id+"F0.wireOp",EDGE,"E900"),sQuery(id+"F0.wireOp",EDGE,"E901"),sQuery(id+"F0.wireOp",EDGE,"E902"),sQuery(id+"F0.wireOp",EDGE,"E903"),sQuery(id+"F0.wireOp",EDGE,"E904"),sQuery(id+"F0.wireOp",EDGE,"E905"),sQuery(id+"F0.wireOp",EDGE,"E906"),sQuery(id+"F0.wireOp",EDGE,"E907"),sQuery(id+"F0.wireOp",EDGE,"E908"),sQuery(id+"F0.wireOp",EDGE,"E909"),sQuery(id+"F0.wireOp",EDGE,"E910"),sQuery(id+"F0.wireOp",EDGE,"E911")])]});
            var Q1;
            Q1=sQuery(id+"F2.wireOp",EDGE,"E912");
            transform(context, id + "F3", {"entities" : qUnion([Q0]), "transformType" : TransformType.ROTATION, "transformAxis" : qUnion([Q1]), "angle" : 180 * degree, "makeCopy" : false});
        }
        {
            var Q0;
            Q0=makeQuery(id+"F1.opExtrude","CAP_FACE",FACE,{"disambiguationData":[OSD([sQuery(id+"F0.wireOp",EDGE,"E0"),sQuery(id+"F0.wireOp",EDGE,"E1"),sQuery(id+"F0.wireOp",EDGE,"E2"),sQuery(id+"F0.wireOp",EDGE,"E3"),sQuery(id+"F0.wireOp",EDGE,"E4"),sQuery(id+"F0.wireOp",EDGE,"E5"),sQuery(id+"F0.wireOp",EDGE,"E6"),sQuery(id+"F0.wireOp",EDGE,"E7"),sQuery(id+"F0.wireOp",EDGE,"E8"),sQuery(id+"F0.wireOp",EDGE,"E9"),sQuery(id+"F0.wireOp",EDGE,"E10"),sQuery(id+"F0.wireOp",EDGE,"E11"),sQuery(id+"F0.wireOp",EDGE,"E12"),sQuery(id+"F0.wireOp",EDGE,"E13"),sQuery(id+"F0.wireOp",EDGE,"E14"),sQuery(id+"F0.wireOp",EDGE,"E15"),sQuery(id+"F0.wireOp",EDGE,"E16"),sQuery(id+"F0.wireOp",EDGE,"E17"),sQuery(id+"F0.wireOp",EDGE,"E18"),sQuery(id+"F0.wireOp",EDGE,"E19"),sQuery(id+"F0.wireOp",EDGE,"E20"),sQuery(id+"F0.wireOp",EDGE,"E21"),sQuery(id+"F0.wireOp",EDGE,"E22"),sQuery(id+"F0.wireOp",EDGE,"E23"),sQuery(id+"F0.wireOp",EDGE,"E24"),sQuery(id+"F0.wireOp",EDGE,"E25"),sQuery(id+"F0.wireOp",EDGE,"E26"),sQuery(id+"F0.wireOp",EDGE,"E27"),sQuery(id+"F0.wireOp",EDGE,"E28"),sQuery(id+"F0.wireOp",EDGE,"E29"),sQuery(id+"F0.wireOp",EDGE,"E30"),sQuery(id+"F0.wireOp",EDGE,"E31"),sQuery(id+"F0.wireOp",EDGE,"E32"),sQuery(id+"F0.wireOp",EDGE,"E33"),sQuery(id+"F0.wireOp",EDGE,"E34"),sQuery(id+"F0.wireOp",EDGE,"E35"),sQuery(id+"F0.wireOp",EDGE,"E36"),sQuery(id+"F0.wireOp",EDGE,"E37"),sQuery(id+"F0.wireOp",EDGE,"E38"),sQuery(id+"F0.wireOp",EDGE,"E39"),sQuery(id+"F0.wireOp",EDGE,"E40"),sQuery(id+"F0.wireOp",EDGE,"E41"),sQuery(id+"F0.wireOp",EDGE,"E42"),sQuery(id+"F0.wireOp",EDGE,"E43"),sQuery(id+"F0.wireOp",EDGE,"E44"),sQuery(id+"F0.wireOp",EDGE,"E45"),sQuery(id+"F0.wireOp",EDGE,"E46"),sQuery(id+"F0.wireOp",EDGE,"E47"),sQuery(id+"F0.wireOp",EDGE,"E48"),sQuery(id+"F0.wireOp",EDGE,"E49"),sQuery(id+"F0.wireOp",EDGE,"E50"),sQuery(id+"F0.wireOp",EDGE,"E51"),sQuery(id+"F0.wireOp",EDGE,"E52"),sQuery(id+"F0.wireOp",EDGE,"E53"),sQuery(id+"F0.wireOp",EDGE,"E54"),sQuery(id+"F0.wireOp",EDGE,"E55"),sQuery(id+"F0.wireOp",EDGE,"E56"),sQuery(id+"F0.wireOp",EDGE,"E57"),sQuery(id+"F0.wireOp",EDGE,"E58"),sQuery(id+"F0.wireOp",EDGE,"E59"),sQuery(id+"F0.wireOp",EDGE,"E60"),sQuery(id+"F0.wireOp",EDGE,"E61"),sQuery(id+"F0.wireOp",EDGE,"E62"),sQuery(id+"F0.wireOp",EDGE,"E63"),sQuery(id+"F0.wireOp",EDGE,"E64"),sQuery(id+"F0.wireOp",EDGE,"E65"),sQuery(id+"F0.wireOp",EDGE,"E66"),sQuery(id+"F0.wireOp",EDGE,"E67"),sQuery(id+"F0.wireOp",EDGE,"E68"),sQuery(id+"F0.wireOp",EDGE,"E69"),sQuery(id+"F0.wireOp",EDGE,"E70"),sQuery(id+"F0.wireOp",EDGE,"E71"),sQuery(id+"F0.wireOp",EDGE,"E72"),sQuery(id+"F0.wireOp",EDGE,"E73"),sQuery(id+"F0.wireOp",EDGE,"E74"),sQuery(id+"F0.wireOp",EDGE,"E75"),sQuery(id+"F0.wireOp",EDGE,"E76"),sQuery(id+"F0.wireOp",EDGE,"E77"),sQuery(id+"F0.wireOp",EDGE,"E78"),sQuery(id+"F0.wireOp",EDGE,"E79"),sQuery(id+"F0.wireOp",EDGE,"E80"),sQuery(id+"F0.wireOp",EDGE,"E81"),sQuery(id+"F0.wireOp",EDGE,"E82"),sQuery(id+"F0.wireOp",EDGE,"E83"),sQuery(id+"F0.wireOp",EDGE,"E84"),sQuery(id+"F0.wireOp",EDGE,"E85"),sQuery(id+"F0.wireOp",EDGE,"E86"),sQuery(id+"F0.wireOp",EDGE,"E87"),sQuery(id+"F0.wireOp",EDGE,"E88"),sQuery(id+"F0.wireOp",EDGE,"E89"),sQuery(id+"F0.wireOp",EDGE,"E90"),sQuery(id+"F0.wireOp",EDGE,"E91"),sQuery(id+"F0.wireOp",EDGE,"E92"),sQuery(id+"F0.wireOp",EDGE,"E93"),sQuery(id+"F0.wireOp",EDGE,"E94"),sQuery(id+"F0.wireOp",EDGE,"E95"),sQuery(id+"F0.wireOp",EDGE,"E96"),sQuery(id+"F0.wireOp",EDGE,"E97"),sQuery(id+"F0.wireOp",EDGE,"E98"),sQuery(id+"F0.wireOp",EDGE,"E99"),sQuery(id+"F0.wireOp",EDGE,"E100"),sQuery(id+"F0.wireOp",EDGE,"E101"),sQuery(id+"F0.wireOp",EDGE,"E102"),sQuery(id+"F0.wireOp",EDGE,"E103"),sQuery(id+"F0.wireOp",EDGE,"E104"),sQuery(id+"F0.wireOp",EDGE,"E105"),sQuery(id+"F0.wireOp",EDGE,"E106"),sQuery(id+"F0.wireOp",EDGE,"E107"),sQuery(id+"F0.wireOp",EDGE,"E108"),sQuery(id+"F0.wireOp",EDGE,"E109"),sQuery(id+"F0.wireOp",EDGE,"E110"),sQuery(id+"F0.wireOp",EDGE,"E111"),sQuery(id+"F0.wireOp",EDGE,"E112"),sQuery(id+"F0.wireOp",EDGE,"E113"),sQuery(id+"F0.wireOp",EDGE,"E114"),sQuery(id+"F0.wireOp",EDGE,"E115"),sQuery(id+"F0.wireOp",EDGE,"E116"),sQuery(id+"F0.wireOp",EDGE,"E117"),sQuery(id+"F0.wireOp",EDGE,"E118"),sQuery(id+"F0.wireOp",EDGE,"E119"),sQuery(id+"F0.wireOp",EDGE,"E120"),sQuery(id+"F0.wireOp",EDGE,"E121"),sQuery(id+"F0.wireOp",EDGE,"E122"),sQuery(id+"F0.wireOp",EDGE,"E123"),sQuery(id+"F0.wireOp",EDGE,"E124"),sQuery(id+"F0.wireOp",EDGE,"E125"),sQuery(id+"F0.wireOp",EDGE,"E126"),sQuery(id+"F0.wireOp",EDGE,"E127"),sQuery(id+"F0.wireOp",EDGE,"E128"),sQuery(id+"F0.wireOp",EDGE,"E129"),sQuery(id+"F0.wireOp",EDGE,"E130"),sQuery(id+"F0.wireOp",EDGE,"E131"),sQuery(id+"F0.wireOp",EDGE,"E132"),sQuery(id+"F0.wireOp",EDGE,"E133"),sQuery(id+"F0.wireOp",EDGE,"E134"),sQuery(id+"F0.wireOp",EDGE,"E135"),sQuery(id+"F0.wireOp",EDGE,"E136"),sQuery(id+"F0.wireOp",EDGE,"E137"),sQuery(id+"F0.wireOp",EDGE,"E138"),sQuery(id+"F0.wireOp",EDGE,"E139"),sQuery(id+"F0.wireOp",EDGE,"E140"),sQuery(id+"F0.wireOp",EDGE,"E141"),sQuery(id+"F0.wireOp",EDGE,"E142"),sQuery(id+"F0.wireOp",EDGE,"E143"),sQuery(id+"F0.wireOp",EDGE,"E144"),sQuery(id+"F0.wireOp",EDGE,"E145"),sQuery(id+"F0.wireOp",EDGE,"E146"),sQuery(id+"F0.wireOp",EDGE,"E147"),sQuery(id+"F0.wireOp",EDGE,"E148"),sQuery(id+"F0.wireOp",EDGE,"E149"),sQuery(id+"F0.wireOp",EDGE,"E150"),sQuery(id+"F0.wireOp",EDGE,"E151"),sQuery(id+"F0.wireOp",EDGE,"E152"),sQuery(id+"F0.wireOp",EDGE,"E153"),sQuery(id+"F0.wireOp",EDGE,"E154"),sQuery(id+"F0.wireOp",EDGE,"E155"),sQuery(id+"F0.wireOp",EDGE,"E156"),sQuery(id+"F0.wireOp",EDGE,"E157"),sQuery(id+"F0.wireOp",EDGE,"E158"),sQuery(id+"F0.wireOp",EDGE,"E159"),sQuery(id+"F0.wireOp",EDGE,"E160"),sQuery(id+"F0.wireOp",EDGE,"E161"),sQuery(id+"F0.wireOp",EDGE,"E162"),sQuery(id+"F0.wireOp",EDGE,"E163"),sQuery(id+"F0.wireOp",EDGE,"E164"),sQuery(id+"F0.wireOp",EDGE,"E165"),sQuery(id+"F0.wireOp",EDGE,"E166"),sQuery(id+"F0.wireOp",EDGE,"E167"),sQuery(id+"F0.wireOp",EDGE,"E168"),sQuery(id+"F0.wireOp",EDGE,"E169"),sQuery(id+"F0.wireOp",EDGE,"E170"),sQuery(id+"F0.wireOp",EDGE,"E171"),sQuery(id+"F0.wireOp",EDGE,"E172"),sQuery(id+"F0.wireOp",EDGE,"E173"),sQuery(id+"F0.wireOp",EDGE,"E174"),sQuery(id+"F0.wireOp",EDGE,"E175"),sQuery(id+"F0.wireOp",EDGE,"E176"),sQuery(id+"F0.wireOp",EDGE,"E177"),sQuery(id+"F0.wireOp",EDGE,"E178"),sQuery(id+"F0.wireOp",EDGE,"E179"),sQuery(id+"F0.wireOp",EDGE,"E180"),sQuery(id+"F0.wireOp",EDGE,"E181"),sQuery(id+"F0.wireOp",EDGE,"E182"),sQuery(id+"F0.wireOp",EDGE,"E183"),sQuery(id+"F0.wireOp",EDGE,"E184"),sQuery(id+"F0.wireOp",EDGE,"E185"),sQuery(id+"F0.wireOp",EDGE,"E186"),sQuery(id+"F0.wireOp",EDGE,"E187"),sQuery(id+"F0.wireOp",EDGE,"E188"),sQuery(id+"F0.wireOp",EDGE,"E189"),sQuery(id+"F0.wireOp",EDGE,"E190"),sQuery(id+"F0.wireOp",EDGE,"E191"),sQuery(id+"F0.wireOp",EDGE,"E192"),sQuery(id+"F0.wireOp",EDGE,"E193"),sQuery(id+"F0.wireOp",EDGE,"E194"),sQuery(id+"F0.wireOp",EDGE,"E195"),sQuery(id+"F0.wireOp",EDGE,"E196"),sQuery(id+"F0.wireOp",EDGE,"E197"),sQuery(id+"F0.wireOp",EDGE,"E198"),sQuery(id+"F0.wireOp",EDGE,"E199"),sQuery(id+"F0.wireOp",EDGE,"E200"),sQuery(id+"F0.wireOp",EDGE,"E201"),sQuery(id+"F0.wireOp",EDGE,"E202"),sQuery(id+"F0.wireOp",EDGE,"E203"),sQuery(id+"F0.wireOp",EDGE,"E204"),sQuery(id+"F0.wireOp",EDGE,"E205"),sQuery(id+"F0.wireOp",EDGE,"E206"),sQuery(id+"F0.wireOp",EDGE,"E207"),sQuery(id+"F0.wireOp",EDGE,"E208"),sQuery(id+"F0.wireOp",EDGE,"E209"),sQuery(id+"F0.wireOp",EDGE,"E210"),sQuery(id+"F0.wireOp",EDGE,"E211"),sQuery(id+"F0.wireOp",EDGE,"E212"),sQuery(id+"F0.wireOp",EDGE,"E213"),sQuery(id+"F0.wireOp",EDGE,"E214"),sQuery(id+"F0.wireOp",EDGE,"E215"),sQuery(id+"F0.wireOp",EDGE,"E216"),sQuery(id+"F0.wireOp",EDGE,"E217"),sQuery(id+"F0.wireOp",EDGE,"E218"),sQuery(id+"F0.wireOp",EDGE,"E219"),sQuery(id+"F0.wireOp",EDGE,"E220"),sQuery(id+"F0.wireOp",EDGE,"E221"),sQuery(id+"F0.wireOp",EDGE,"E222"),sQuery(id+"F0.wireOp",EDGE,"E223"),sQuery(id+"F0.wireOp",EDGE,"E224"),sQuery(id+"F0.wireOp",EDGE,"E225"),sQuery(id+"F0.wireOp",EDGE,"E226"),sQuery(id+"F0.wireOp",EDGE,"E227"),sQuery(id+"F0.wireOp",EDGE,"E228"),sQuery(id+"F0.wireOp",EDGE,"E229"),sQuery(id+"F0.wireOp",EDGE,"E230"),sQuery(id+"F0.wireOp",EDGE,"E231"),sQuery(id+"F0.wireOp",EDGE,"E232"),sQuery(id+"F0.wireOp",EDGE,"E233"),sQuery(id+"F0.wireOp",EDGE,"E234"),sQuery(id+"F0.wireOp",EDGE,"E235"),sQuery(id+"F0.wireOp",EDGE,"E236"),sQuery(id+"F0.wireOp",EDGE,"E237"),sQuery(id+"F0.wireOp",EDGE,"E238"),sQuery(id+"F0.wireOp",EDGE,"E239"),sQuery(id+"F0.wireOp",EDGE,"E240"),sQuery(id+"F0.wireOp",EDGE,"E241"),sQuery(id+"F0.wireOp",EDGE,"E242"),sQuery(id+"F0.wireOp",EDGE,"E243"),sQuery(id+"F0.wireOp",EDGE,"E244"),sQuery(id+"F0.wireOp",EDGE,"E245"),sQuery(id+"F0.wireOp",EDGE,"E246"),sQuery(id+"F0.wireOp",EDGE,"E247"),sQuery(id+"F0.wireOp",EDGE,"E248"),sQuery(id+"F0.wireOp",EDGE,"E249"),sQuery(id+"F0.wireOp",EDGE,"E250"),sQuery(id+"F0.wireOp",EDGE,"E251"),sQuery(id+"F0.wireOp",EDGE,"E252"),sQuery(id+"F0.wireOp",EDGE,"E253"),sQuery(id+"F0.wireOp",EDGE,"E254"),sQuery(id+"F0.wireOp",EDGE,"E255"),sQuery(id+"F0.wireOp",EDGE,"E256"),sQuery(id+"F0.wireOp",EDGE,"E257"),sQuery(id+"F0.wireOp",EDGE,"E258"),sQuery(id+"F0.wireOp",EDGE,"E259"),sQuery(id+"F0.wireOp",EDGE,"E260"),sQuery(id+"F0.wireOp",EDGE,"E261"),sQuery(id+"F0.wireOp",EDGE,"E262"),sQuery(id+"F0.wireOp",EDGE,"E263"),sQuery(id+"F0.wireOp",EDGE,"E264"),sQuery(id+"F0.wireOp",EDGE,"E265"),sQuery(id+"F0.wireOp",EDGE,"E266"),sQuery(id+"F0.wireOp",EDGE,"E267"),sQuery(id+"F0.wireOp",EDGE,"E268"),sQuery(id+"F0.wireOp",EDGE,"E269"),sQuery(id+"F0.wireOp",EDGE,"E270"),sQuery(id+"F0.wireOp",EDGE,"E271"),sQuery(id+"F0.wireOp",EDGE,"E272"),sQuery(id+"F0.wireOp",EDGE,"E273"),sQuery(id+"F0.wireOp",EDGE,"E274"),sQuery(id+"F0.wireOp",EDGE,"E275"),sQuery(id+"F0.wireOp",EDGE,"E276"),sQuery(id+"F0.wireOp",EDGE,"E277"),sQuery(id+"F0.wireOp",EDGE,"E278"),sQuery(id+"F0.wireOp",EDGE,"E279"),sQuery(id+"F0.wireOp",EDGE,"E280"),sQuery(id+"F0.wireOp",EDGE,"E281"),sQuery(id+"F0.wireOp",EDGE,"E282"),sQuery(id+"F0.wireOp",EDGE,"E283"),sQuery(id+"F0.wireOp",EDGE,"E284"),sQuery(id+"F0.wireOp",EDGE,"E285"),sQuery(id+"F0.wireOp",EDGE,"E286"),sQuery(id+"F0.wireOp",EDGE,"E287"),sQuery(id+"F0.wireOp",EDGE,"E288"),sQuery(id+"F0.wireOp",EDGE,"E289"),sQuery(id+"F0.wireOp",EDGE,"E290"),sQuery(id+"F0.wireOp",EDGE,"E291"),sQuery(id+"F0.wireOp",EDGE,"E292"),sQuery(id+"F0.wireOp",EDGE,"E293"),sQuery(id+"F0.wireOp",EDGE,"E294"),sQuery(id+"F0.wireOp",EDGE,"E295"),sQuery(id+"F0.wireOp",EDGE,"E296"),sQuery(id+"F0.wireOp",EDGE,"E297"),sQuery(id+"F0.wireOp",EDGE,"E298"),sQuery(id+"F0.wireOp",EDGE,"E299"),sQuery(id+"F0.wireOp",EDGE,"E300"),sQuery(id+"F0.wireOp",EDGE,"E301"),sQuery(id+"F0.wireOp",EDGE,"E302"),sQuery(id+"F0.wireOp",EDGE,"E303"),sQuery(id+"F0.wireOp",EDGE,"E304"),sQuery(id+"F0.wireOp",EDGE,"E305"),sQuery(id+"F0.wireOp",EDGE,"E306"),sQuery(id+"F0.wireOp",EDGE,"E307"),sQuery(id+"F0.wireOp",EDGE,"E308"),sQuery(id+"F0.wireOp",EDGE,"E309"),sQuery(id+"F0.wireOp",EDGE,"E310"),sQuery(id+"F0.wireOp",EDGE,"E311"),sQuery(id+"F0.wireOp",EDGE,"E312"),sQuery(id+"F0.wireOp",EDGE,"E313"),sQuery(id+"F0.wireOp",EDGE,"E314"),sQuery(id+"F0.wireOp",EDGE,"E315"),sQuery(id+"F0.wireOp",EDGE,"E316"),sQuery(id+"F0.wireOp",EDGE,"E317"),sQuery(id+"F0.wireOp",EDGE,"E318"),sQuery(id+"F0.wireOp",EDGE,"E319"),sQuery(id+"F0.wireOp",EDGE,"E320"),sQuery(id+"F0.wireOp",EDGE,"E321"),sQuery(id+"F0.wireOp",EDGE,"E322"),sQuery(id+"F0.wireOp",EDGE,"E323"),sQuery(id+"F0.wireOp",EDGE,"E324"),sQuery(id+"F0.wireOp",EDGE,"E325"),sQuery(id+"F0.wireOp",EDGE,"E326"),sQuery(id+"F0.wireOp",EDGE,"E327"),sQuery(id+"F0.wireOp",EDGE,"E328"),sQuery(id+"F0.wireOp",EDGE,"E329"),sQuery(id+"F0.wireOp",EDGE,"E330"),sQuery(id+"F0.wireOp",EDGE,"E331"),sQuery(id+"F0.wireOp",EDGE,"E332"),sQuery(id+"F0.wireOp",EDGE,"E333"),sQuery(id+"F0.wireOp",EDGE,"E334"),sQuery(id+"F0.wireOp",EDGE,"E335"),sQuery(id+"F0.wireOp",EDGE,"E336"),sQuery(id+"F0.wireOp",EDGE,"E337"),sQuery(id+"F0.wireOp",EDGE,"E338"),sQuery(id+"F0.wireOp",EDGE,"E339"),sQuery(id+"F0.wireOp",EDGE,"E340"),sQuery(id+"F0.wireOp",EDGE,"E341"),sQuery(id+"F0.wireOp",EDGE,"E342"),sQuery(id+"F0.wireOp",EDGE,"E343"),sQuery(id+"F0.wireOp",EDGE,"E344"),sQuery(id+"F0.wireOp",EDGE,"E345"),sQuery(id+"F0.wireOp",EDGE,"E346"),sQuery(id+"F0.wireOp",EDGE,"E347"),sQuery(id+"F0.wireOp",EDGE,"E348"),sQuery(id+"F0.wireOp",EDGE,"E349"),sQuery(id+"F0.wireOp",EDGE,"E350"),sQuery(id+"F0.wireOp",EDGE,"E351"),sQuery(id+"F0.wireOp",EDGE,"E352"),sQuery(id+"F0.wireOp",EDGE,"E353"),sQuery(id+"F0.wireOp",EDGE,"E354"),sQuery(id+"F0.wireOp",EDGE,"E355"),sQuery(id+"F0.wireOp",EDGE,"E356"),sQuery(id+"F0.wireOp",EDGE,"E357"),sQuery(id+"F0.wireOp",EDGE,"E358"),sQuery(id+"F0.wireOp",EDGE,"E359"),sQuery(id+"F0.wireOp",EDGE,"E360"),sQuery(id+"F0.wireOp",EDGE,"E361"),sQuery(id+"F0.wireOp",EDGE,"E362"),sQuery(id+"F0.wireOp",EDGE,"E363"),sQuery(id+"F0.wireOp",EDGE,"E364"),sQuery(id+"F0.wireOp",EDGE,"E365"),sQuery(id+"F0.wireOp",EDGE,"E366"),sQuery(id+"F0.wireOp",EDGE,"E367"),sQuery(id+"F0.wireOp",EDGE,"E368"),sQuery(id+"F0.wireOp",EDGE,"E369"),sQuery(id+"F0.wireOp",EDGE,"E370"),sQuery(id+"F0.wireOp",EDGE,"E371"),sQuery(id+"F0.wireOp",EDGE,"E372"),sQuery(id+"F0.wireOp",EDGE,"E373"),sQuery(id+"F0.wireOp",EDGE,"E374"),sQuery(id+"F0.wireOp",EDGE,"E375"),sQuery(id+"F0.wireOp",EDGE,"E376"),sQuery(id+"F0.wireOp",EDGE,"E377"),sQuery(id+"F0.wireOp",EDGE,"E378"),sQuery(id+"F0.wireOp",EDGE,"E379"),sQuery(id+"F0.wireOp",EDGE,"E380"),sQuery(id+"F0.wireOp",EDGE,"E381"),sQuery(id+"F0.wireOp",EDGE,"E382"),sQuery(id+"F0.wireOp",EDGE,"E383"),sQuery(id+"F0.wireOp",EDGE,"E384"),sQuery(id+"F0.wireOp",EDGE,"E385"),sQuery(id+"F0.wireOp",EDGE,"E386"),sQuery(id+"F0.wireOp",EDGE,"E387"),sQuery(id+"F0.wireOp",EDGE,"E388"),sQuery(id+"F0.wireOp",EDGE,"E389"),sQuery(id+"F0.wireOp",EDGE,"E390"),sQuery(id+"F0.wireOp",EDGE,"E391"),sQuery(id+"F0.wireOp",EDGE,"E392"),sQuery(id+"F0.wireOp",EDGE,"E393"),sQuery(id+"F0.wireOp",EDGE,"E394"),sQuery(id+"F0.wireOp",EDGE,"E395"),sQuery(id+"F0.wireOp",EDGE,"E396"),sQuery(id+"F0.wireOp",EDGE,"E397"),sQuery(id+"F0.wireOp",EDGE,"E398"),sQuery(id+"F0.wireOp",EDGE,"E399"),sQuery(id+"F0.wireOp",EDGE,"E400"),sQuery(id+"F0.wireOp",EDGE,"E401"),sQuery(id+"F0.wireOp",EDGE,"E402"),sQuery(id+"F0.wireOp",EDGE,"E403"),sQuery(id+"F0.wireOp",EDGE,"E404"),sQuery(id+"F0.wireOp",EDGE,"E405"),sQuery(id+"F0.wireOp",EDGE,"E406"),sQuery(id+"F0.wireOp",EDGE,"E407"),sQuery(id+"F0.wireOp",EDGE,"E408"),sQuery(id+"F0.wireOp",EDGE,"E409"),sQuery(id+"F0.wireOp",EDGE,"E410"),sQuery(id+"F0.wireOp",EDGE,"E411"),sQuery(id+"F0.wireOp",EDGE,"E412"),sQuery(id+"F0.wireOp",EDGE,"E413"),sQuery(id+"F0.wireOp",EDGE,"E414"),sQuery(id+"F0.wireOp",EDGE,"E415"),sQuery(id+"F0.wireOp",EDGE,"E416"),sQuery(id+"F0.wireOp",EDGE,"E417"),sQuery(id+"F0.wireOp",EDGE,"E418"),sQuery(id+"F0.wireOp",EDGE,"E419"),sQuery(id+"F0.wireOp",EDGE,"E420"),sQuery(id+"F0.wireOp",EDGE,"E421"),sQuery(id+"F0.wireOp",EDGE,"E422"),sQuery(id+"F0.wireOp",EDGE,"E423"),sQuery(id+"F0.wireOp",EDGE,"E424"),sQuery(id+"F0.wireOp",EDGE,"E425"),sQuery(id+"F0.wireOp",EDGE,"E426"),sQuery(id+"F0.wireOp",EDGE,"E427"),sQuery(id+"F0.wireOp",EDGE,"E428"),sQuery(id+"F0.wireOp",EDGE,"E429"),sQuery(id+"F0.wireOp",EDGE,"E430"),sQuery(id+"F0.wireOp",EDGE,"E431"),sQuery(id+"F0.wireOp",EDGE,"E432"),sQuery(id+"F0.wireOp",EDGE,"E433"),sQuery(id+"F0.wireOp",EDGE,"E434"),sQuery(id+"F0.wireOp",EDGE,"E435"),sQuery(id+"F0.wireOp",EDGE,"E436"),sQuery(id+"F0.wireOp",EDGE,"E437"),sQuery(id+"F0.wireOp",EDGE,"E438"),sQuery(id+"F0.wireOp",EDGE,"E439"),sQuery(id+"F0.wireOp",EDGE,"E440"),sQuery(id+"F0.wireOp",EDGE,"E441"),sQuery(id+"F0.wireOp",EDGE,"E442"),sQuery(id+"F0.wireOp",EDGE,"E443"),sQuery(id+"F0.wireOp",EDGE,"E444"),sQuery(id+"F0.wireOp",EDGE,"E445"),sQuery(id+"F0.wireOp",EDGE,"E446"),sQuery(id+"F0.wireOp",EDGE,"E447"),sQuery(id+"F0.wireOp",EDGE,"E448"),sQuery(id+"F0.wireOp",EDGE,"E449"),sQuery(id+"F0.wireOp",EDGE,"E450"),sQuery(id+"F0.wireOp",EDGE,"E451"),sQuery(id+"F0.wireOp",EDGE,"E452"),sQuery(id+"F0.wireOp",EDGE,"E453"),sQuery(id+"F0.wireOp",EDGE,"E454"),sQuery(id+"F0.wireOp",EDGE,"E455"),sQuery(id+"F0.wireOp",EDGE,"E456"),sQuery(id+"F0.wireOp",EDGE,"E457"),sQuery(id+"F0.wireOp",EDGE,"E458"),sQuery(id+"F0.wireOp",EDGE,"E459"),sQuery(id+"F0.wireOp",EDGE,"E460"),sQuery(id+"F0.wireOp",EDGE,"E461"),sQuery(id+"F0.wireOp",EDGE,"E462"),sQuery(id+"F0.wireOp",EDGE,"E463"),sQuery(id+"F0.wireOp",EDGE,"E464"),sQuery(id+"F0.wireOp",EDGE,"E465"),sQuery(id+"F0.wireOp",EDGE,"E466"),sQuery(id+"F0.wireOp",EDGE,"E467"),sQuery(id+"F0.wireOp",EDGE,"E468"),sQuery(id+"F0.wireOp",EDGE,"E469"),sQuery(id+"F0.wireOp",EDGE,"E470"),sQuery(id+"F0.wireOp",EDGE,"E471"),sQuery(id+"F0.wireOp",EDGE,"E472"),sQuery(id+"F0.wireOp",EDGE,"E473"),sQuery(id+"F0.wireOp",EDGE,"E474"),sQuery(id+"F0.wireOp",EDGE,"E475"),sQuery(id+"F0.wireOp",EDGE,"E476"),sQuery(id+"F0.wireOp",EDGE,"E477"),sQuery(id+"F0.wireOp",EDGE,"E478"),sQuery(id+"F0.wireOp",EDGE,"E479"),sQuery(id+"F0.wireOp",EDGE,"E480"),sQuery(id+"F0.wireOp",EDGE,"E481"),sQuery(id+"F0.wireOp",EDGE,"E482"),sQuery(id+"F0.wireOp",EDGE,"E483"),sQuery(id+"F0.wireOp",EDGE,"E484"),sQuery(id+"F0.wireOp",EDGE,"E485"),sQuery(id+"F0.wireOp",EDGE,"E486"),sQuery(id+"F0.wireOp",EDGE,"E487"),sQuery(id+"F0.wireOp",EDGE,"E488"),sQuery(id+"F0.wireOp",EDGE,"E489"),sQuery(id+"F0.wireOp",EDGE,"E490"),sQuery(id+"F0.wireOp",EDGE,"E491"),sQuery(id+"F0.wireOp",EDGE,"E492"),sQuery(id+"F0.wireOp",EDGE,"E493"),sQuery(id+"F0.wireOp",EDGE,"E494"),sQuery(id+"F0.wireOp",EDGE,"E495"),sQuery(id+"F0.wireOp",EDGE,"E496"),sQuery(id+"F0.wireOp",EDGE,"E497"),sQuery(id+"F0.wireOp",EDGE,"E498"),sQuery(id+"F0.wireOp",EDGE,"E499"),sQuery(id+"F0.wireOp",EDGE,"E500"),sQuery(id+"F0.wireOp",EDGE,"E501"),sQuery(id+"F0.wireOp",EDGE,"E502"),sQuery(id+"F0.wireOp",EDGE,"E503"),sQuery(id+"F0.wireOp",EDGE,"E504"),sQuery(id+"F0.wireOp",EDGE,"E505"),sQuery(id+"F0.wireOp",EDGE,"E506"),sQuery(id+"F0.wireOp",EDGE,"E507"),sQuery(id+"F0.wireOp",EDGE,"E508"),sQuery(id+"F0.wireOp",EDGE,"E509"),sQuery(id+"F0.wireOp",EDGE,"E510"),sQuery(id+"F0.wireOp",EDGE,"E511"),sQuery(id+"F0.wireOp",EDGE,"E512"),sQuery(id+"F0.wireOp",EDGE,"E513"),sQuery(id+"F0.wireOp",EDGE,"E514"),sQuery(id+"F0.wireOp",EDGE,"E515"),sQuery(id+"F0.wireOp",EDGE,"E516"),sQuery(id+"F0.wireOp",EDGE,"E517"),sQuery(id+"F0.wireOp",EDGE,"E518"),sQuery(id+"F0.wireOp",EDGE,"E519"),sQuery(id+"F0.wireOp",EDGE,"E520"),sQuery(id+"F0.wireOp",EDGE,"E521"),sQuery(id+"F0.wireOp",EDGE,"E522"),sQuery(id+"F0.wireOp",EDGE,"E523"),sQuery(id+"F0.wireOp",EDGE,"E524"),sQuery(id+"F0.wireOp",EDGE,"E525"),sQuery(id+"F0.wireOp",EDGE,"E526"),sQuery(id+"F0.wireOp",EDGE,"E527"),sQuery(id+"F0.wireOp",EDGE,"E528"),sQuery(id+"F0.wireOp",EDGE,"E529"),sQuery(id+"F0.wireOp",EDGE,"E530"),sQuery(id+"F0.wireOp",EDGE,"E531"),sQuery(id+"F0.wireOp",EDGE,"E532"),sQuery(id+"F0.wireOp",EDGE,"E533"),sQuery(id+"F0.wireOp",EDGE,"E534"),sQuery(id+"F0.wireOp",EDGE,"E535"),sQuery(id+"F0.wireOp",EDGE,"E536"),sQuery(id+"F0.wireOp",EDGE,"E537"),sQuery(id+"F0.wireOp",EDGE,"E538"),sQuery(id+"F0.wireOp",EDGE,"E539"),sQuery(id+"F0.wireOp",EDGE,"E540"),sQuery(id+"F0.wireOp",EDGE,"E541"),sQuery(id+"F0.wireOp",EDGE,"E542"),sQuery(id+"F0.wireOp",EDGE,"E543"),sQuery(id+"F0.wireOp",EDGE,"E544"),sQuery(id+"F0.wireOp",EDGE,"E545"),sQuery(id+"F0.wireOp",EDGE,"E546"),sQuery(id+"F0.wireOp",EDGE,"E547"),sQuery(id+"F0.wireOp",EDGE,"E548"),sQuery(id+"F0.wireOp",EDGE,"E549"),sQuery(id+"F0.wireOp",EDGE,"E550"),sQuery(id+"F0.wireOp",EDGE,"E551"),sQuery(id+"F0.wireOp",EDGE,"E552"),sQuery(id+"F0.wireOp",EDGE,"E553"),sQuery(id+"F0.wireOp",EDGE,"E554"),sQuery(id+"F0.wireOp",EDGE,"E555"),sQuery(id+"F0.wireOp",EDGE,"E556"),sQuery(id+"F0.wireOp",EDGE,"E557"),sQuery(id+"F0.wireOp",EDGE,"E558"),sQuery(id+"F0.wireOp",EDGE,"E559"),sQuery(id+"F0.wireOp",EDGE,"E560"),sQuery(id+"F0.wireOp",EDGE,"E561"),sQuery(id+"F0.wireOp",EDGE,"E562"),sQuery(id+"F0.wireOp",EDGE,"E563"),sQuery(id+"F0.wireOp",EDGE,"E564"),sQuery(id+"F0.wireOp",EDGE,"E565"),sQuery(id+"F0.wireOp",EDGE,"E566"),sQuery(id+"F0.wireOp",EDGE,"E567"),sQuery(id+"F0.wireOp",EDGE,"E568"),sQuery(id+"F0.wireOp",EDGE,"E569"),sQuery(id+"F0.wireOp",EDGE,"E570"),sQuery(id+"F0.wireOp",EDGE,"E571"),sQuery(id+"F0.wireOp",EDGE,"E572"),sQuery(id+"F0.wireOp",EDGE,"E573"),sQuery(id+"F0.wireOp",EDGE,"E574"),sQuery(id+"F0.wireOp",EDGE,"E575"),sQuery(id+"F0.wireOp",EDGE,"E576"),sQuery(id+"F0.wireOp",EDGE,"E577"),sQuery(id+"F0.wireOp",EDGE,"E578"),sQuery(id+"F0.wireOp",EDGE,"E579"),sQuery(id+"F0.wireOp",EDGE,"E580"),sQuery(id+"F0.wireOp",EDGE,"E581"),sQuery(id+"F0.wireOp",EDGE,"E582"),sQuery(id+"F0.wireOp",EDGE,"E583"),sQuery(id+"F0.wireOp",EDGE,"E584"),sQuery(id+"F0.wireOp",EDGE,"E585"),sQuery(id+"F0.wireOp",EDGE,"E586"),sQuery(id+"F0.wireOp",EDGE,"E587"),sQuery(id+"F0.wireOp",EDGE,"E588"),sQuery(id+"F0.wireOp",EDGE,"E589"),sQuery(id+"F0.wireOp",EDGE,"E590"),sQuery(id+"F0.wireOp",EDGE,"E591"),sQuery(id+"F0.wireOp",EDGE,"E592"),sQuery(id+"F0.wireOp",EDGE,"E593"),sQuery(id+"F0.wireOp",EDGE,"E594"),sQuery(id+"F0.wireOp",EDGE,"E595"),sQuery(id+"F0.wireOp",EDGE,"E596"),sQuery(id+"F0.wireOp",EDGE,"E597"),sQuery(id+"F0.wireOp",EDGE,"E598"),sQuery(id+"F0.wireOp",EDGE,"E599"),sQuery(id+"F0.wireOp",EDGE,"E600"),sQuery(id+"F0.wireOp",EDGE,"E601"),sQuery(id+"F0.wireOp",EDGE,"E602"),sQuery(id+"F0.wireOp",EDGE,"E603"),sQuery(id+"F0.wireOp",EDGE,"E604"),sQuery(id+"F0.wireOp",EDGE,"E605"),sQuery(id+"F0.wireOp",EDGE,"E606"),sQuery(id+"F0.wireOp",EDGE,"E607"),sQuery(id+"F0.wireOp",EDGE,"E608"),sQuery(id+"F0.wireOp",EDGE,"E609"),sQuery(id+"F0.wireOp",EDGE,"E610"),sQuery(id+"F0.wireOp",EDGE,"E611"),sQuery(id+"F0.wireOp",EDGE,"E612"),sQuery(id+"F0.wireOp",EDGE,"E613"),sQuery(id+"F0.wireOp",EDGE,"E614"),sQuery(id+"F0.wireOp",EDGE,"E615"),sQuery(id+"F0.wireOp",EDGE,"E616"),sQuery(id+"F0.wireOp",EDGE,"E617"),sQuery(id+"F0.wireOp",EDGE,"E618"),sQuery(id+"F0.wireOp",EDGE,"E619"),sQuery(id+"F0.wireOp",EDGE,"E620"),sQuery(id+"F0.wireOp",EDGE,"E621"),sQuery(id+"F0.wireOp",EDGE,"E622"),sQuery(id+"F0.wireOp",EDGE,"E623"),sQuery(id+"F0.wireOp",EDGE,"E624"),sQuery(id+"F0.wireOp",EDGE,"E625"),sQuery(id+"F0.wireOp",EDGE,"E626"),sQuery(id+"F0.wireOp",EDGE,"E627"),sQuery(id+"F0.wireOp",EDGE,"E628"),sQuery(id+"F0.wireOp",EDGE,"E629"),sQuery(id+"F0.wireOp",EDGE,"E630"),sQuery(id+"F0.wireOp",EDGE,"E631"),sQuery(id+"F0.wireOp",EDGE,"E632"),sQuery(id+"F0.wireOp",EDGE,"E633"),sQuery(id+"F0.wireOp",EDGE,"E634"),sQuery(id+"F0.wireOp",EDGE,"E635"),sQuery(id+"F0.wireOp",EDGE,"E636"),sQuery(id+"F0.wireOp",EDGE,"E637"),sQuery(id+"F0.wireOp",EDGE,"E638"),sQuery(id+"F0.wireOp",EDGE,"E639"),sQuery(id+"F0.wireOp",EDGE,"E640"),sQuery(id+"F0.wireOp",EDGE,"E641"),sQuery(id+"F0.wireOp",EDGE,"E642"),sQuery(id+"F0.wireOp",EDGE,"E643"),sQuery(id+"F0.wireOp",EDGE,"E644"),sQuery(id+"F0.wireOp",EDGE,"E645"),sQuery(id+"F0.wireOp",EDGE,"E646"),sQuery(id+"F0.wireOp",EDGE,"E647"),sQuery(id+"F0.wireOp",EDGE,"E648"),sQuery(id+"F0.wireOp",EDGE,"E649"),sQuery(id+"F0.wireOp",EDGE,"E650"),sQuery(id+"F0.wireOp",EDGE,"E651"),sQuery(id+"F0.wireOp",EDGE,"E652"),sQuery(id+"F0.wireOp",EDGE,"E653"),sQuery(id+"F0.wireOp",EDGE,"E654"),sQuery(id+"F0.wireOp",EDGE,"E655"),sQuery(id+"F0.wireOp",EDGE,"E656"),sQuery(id+"F0.wireOp",EDGE,"E657"),sQuery(id+"F0.wireOp",EDGE,"E658"),sQuery(id+"F0.wireOp",EDGE,"E659"),sQuery(id+"F0.wireOp",EDGE,"E660"),sQuery(id+"F0.wireOp",EDGE,"E661"),sQuery(id+"F0.wireOp",EDGE,"E662"),sQuery(id+"F0.wireOp",EDGE,"E663"),sQuery(id+"F0.wireOp",EDGE,"E664"),sQuery(id+"F0.wireOp",EDGE,"E665"),sQuery(id+"F0.wireOp",EDGE,"E666"),sQuery(id+"F0.wireOp",EDGE,"E667"),sQuery(id+"F0.wireOp",EDGE,"E668"),sQuery(id+"F0.wireOp",EDGE,"E669"),sQuery(id+"F0.wireOp",EDGE,"E670"),sQuery(id+"F0.wireOp",EDGE,"E671"),sQuery(id+"F0.wireOp",EDGE,"E672"),sQuery(id+"F0.wireOp",EDGE,"E673"),sQuery(id+"F0.wireOp",EDGE,"E674"),sQuery(id+"F0.wireOp",EDGE,"E675"),sQuery(id+"F0.wireOp",EDGE,"E676"),sQuery(id+"F0.wireOp",EDGE,"E677"),sQuery(id+"F0.wireOp",EDGE,"E678"),sQuery(id+"F0.wireOp",EDGE,"E679"),sQuery(id+"F0.wireOp",EDGE,"E680"),sQuery(id+"F0.wireOp",EDGE,"E681"),sQuery(id+"F0.wireOp",EDGE,"E682"),sQuery(id+"F0.wireOp",EDGE,"E683"),sQuery(id+"F0.wireOp",EDGE,"E684"),sQuery(id+"F0.wireOp",EDGE,"E685"),sQuery(id+"F0.wireOp",EDGE,"E686"),sQuery(id+"F0.wireOp",EDGE,"E687"),sQuery(id+"F0.wireOp",EDGE,"E688"),sQuery(id+"F0.wireOp",EDGE,"E689"),sQuery(id+"F0.wireOp",EDGE,"E690"),sQuery(id+"F0.wireOp",EDGE,"E691"),sQuery(id+"F0.wireOp",EDGE,"E692"),sQuery(id+"F0.wireOp",EDGE,"E693"),sQuery(id+"F0.wireOp",EDGE,"E694"),sQuery(id+"F0.wireOp",EDGE,"E695"),sQuery(id+"F0.wireOp",EDGE,"E696"),sQuery(id+"F0.wireOp",EDGE,"E697"),sQuery(id+"F0.wireOp",EDGE,"E698"),sQuery(id+"F0.wireOp",EDGE,"E699"),sQuery(id+"F0.wireOp",EDGE,"E700"),sQuery(id+"F0.wireOp",EDGE,"E701"),sQuery(id+"F0.wireOp",EDGE,"E702"),sQuery(id+"F0.wireOp",EDGE,"E703"),sQuery(id+"F0.wireOp",EDGE,"E704"),sQuery(id+"F0.wireOp",EDGE,"E705"),sQuery(id+"F0.wireOp",EDGE,"E706"),sQuery(id+"F0.wireOp",EDGE,"E707"),sQuery(id+"F0.wireOp",EDGE,"E708"),sQuery(id+"F0.wireOp",EDGE,"E709"),sQuery(id+"F0.wireOp",EDGE,"E710"),sQuery(id+"F0.wireOp",EDGE,"E711"),sQuery(id+"F0.wireOp",EDGE,"E712"),sQuery(id+"F0.wireOp",EDGE,"E713"),sQuery(id+"F0.wireOp",EDGE,"E714"),sQuery(id+"F0.wireOp",EDGE,"E715"),sQuery(id+"F0.wireOp",EDGE,"E716"),sQuery(id+"F0.wireOp",EDGE,"E717"),sQuery(id+"F0.wireOp",EDGE,"E718"),sQuery(id+"F0.wireOp",EDGE,"E719"),sQuery(id+"F0.wireOp",EDGE,"E720"),sQuery(id+"F0.wireOp",EDGE,"E721"),sQuery(id+"F0.wireOp",EDGE,"E722"),sQuery(id+"F0.wireOp",EDGE,"E723"),sQuery(id+"F0.wireOp",EDGE,"E724"),sQuery(id+"F0.wireOp",EDGE,"E725"),sQuery(id+"F0.wireOp",EDGE,"E726"),sQuery(id+"F0.wireOp",EDGE,"E727"),sQuery(id+"F0.wireOp",EDGE,"E728"),sQuery(id+"F0.wireOp",EDGE,"E729"),sQuery(id+"F0.wireOp",EDGE,"E730"),sQuery(id+"F0.wireOp",EDGE,"E731"),sQuery(id+"F0.wireOp",EDGE,"E732"),sQuery(id+"F0.wireOp",EDGE,"E733"),sQuery(id+"F0.wireOp",EDGE,"E734"),sQuery(id+"F0.wireOp",EDGE,"E735"),sQuery(id+"F0.wireOp",EDGE,"E736"),sQuery(id+"F0.wireOp",EDGE,"E737"),sQuery(id+"F0.wireOp",EDGE,"E738"),sQuery(id+"F0.wireOp",EDGE,"E739"),sQuery(id+"F0.wireOp",EDGE,"E740"),sQuery(id+"F0.wireOp",EDGE,"E741"),sQuery(id+"F0.wireOp",EDGE,"E742"),sQuery(id+"F0.wireOp",EDGE,"E743"),sQuery(id+"F0.wireOp",EDGE,"E744"),sQuery(id+"F0.wireOp",EDGE,"E745"),sQuery(id+"F0.wireOp",EDGE,"E746"),sQuery(id+"F0.wireOp",EDGE,"E747"),sQuery(id+"F0.wireOp",EDGE,"E748"),sQuery(id+"F0.wireOp",EDGE,"E749"),sQuery(id+"F0.wireOp",EDGE,"E750"),sQuery(id+"F0.wireOp",EDGE,"E751"),sQuery(id+"F0.wireOp",EDGE,"E752"),sQuery(id+"F0.wireOp",EDGE,"E753"),sQuery(id+"F0.wireOp",EDGE,"E754"),sQuery(id+"F0.wireOp",EDGE,"E755"),sQuery(id+"F0.wireOp",EDGE,"E756"),sQuery(id+"F0.wireOp",EDGE,"E757"),sQuery(id+"F0.wireOp",EDGE,"E758"),sQuery(id+"F0.wireOp",EDGE,"E759"),sQuery(id+"F0.wireOp",EDGE,"E760"),sQuery(id+"F0.wireOp",EDGE,"E761"),sQuery(id+"F0.wireOp",EDGE,"E762"),sQuery(id+"F0.wireOp",EDGE,"E763"),sQuery(id+"F0.wireOp",EDGE,"E764"),sQuery(id+"F0.wireOp",EDGE,"E765"),sQuery(id+"F0.wireOp",EDGE,"E766"),sQuery(id+"F0.wireOp",EDGE,"E767"),sQuery(id+"F0.wireOp",EDGE,"E768"),sQuery(id+"F0.wireOp",EDGE,"E769"),sQuery(id+"F0.wireOp",EDGE,"E770"),sQuery(id+"F0.wireOp",EDGE,"E771"),sQuery(id+"F0.wireOp",EDGE,"E772"),sQuery(id+"F0.wireOp",EDGE,"E773"),sQuery(id+"F0.wireOp",EDGE,"E774"),sQuery(id+"F0.wireOp",EDGE,"E775"),sQuery(id+"F0.wireOp",EDGE,"E776"),sQuery(id+"F0.wireOp",EDGE,"E777"),sQuery(id+"F0.wireOp",EDGE,"E778"),sQuery(id+"F0.wireOp",EDGE,"E779"),sQuery(id+"F0.wireOp",EDGE,"E780"),sQuery(id+"F0.wireOp",EDGE,"E781"),sQuery(id+"F0.wireOp",EDGE,"E782"),sQuery(id+"F0.wireOp",EDGE,"E783"),sQuery(id+"F0.wireOp",EDGE,"E784"),sQuery(id+"F0.wireOp",EDGE,"E785"),sQuery(id+"F0.wireOp",EDGE,"E786"),sQuery(id+"F0.wireOp",EDGE,"E787"),sQuery(id+"F0.wireOp",EDGE,"E788"),sQuery(id+"F0.wireOp",EDGE,"E789"),sQuery(id+"F0.wireOp",EDGE,"E790"),sQuery(id+"F0.wireOp",EDGE,"E791"),sQuery(id+"F0.wireOp",EDGE,"E792"),sQuery(id+"F0.wireOp",EDGE,"E793"),sQuery(id+"F0.wireOp",EDGE,"E794"),sQuery(id+"F0.wireOp",EDGE,"E795"),sQuery(id+"F0.wireOp",EDGE,"E796"),sQuery(id+"F0.wireOp",EDGE,"E797"),sQuery(id+"F0.wireOp",EDGE,"E798"),sQuery(id+"F0.wireOp",EDGE,"E799"),sQuery(id+"F0.wireOp",EDGE,"E800"),sQuery(id+"F0.wireOp",EDGE,"E801"),sQuery(id+"F0.wireOp",EDGE,"E802"),sQuery(id+"F0.wireOp",EDGE,"E803"),sQuery(id+"F0.wireOp",EDGE,"E804"),sQuery(id+"F0.wireOp",EDGE,"E805"),sQuery(id+"F0.wireOp",EDGE,"E806"),sQuery(id+"F0.wireOp",EDGE,"E807"),sQuery(id+"F0.wireOp",EDGE,"E808"),sQuery(id+"F0.wireOp",EDGE,"E809"),sQuery(id+"F0.wireOp",EDGE,"E810"),sQuery(id+"F0.wireOp",EDGE,"E811"),sQuery(id+"F0.wireOp",EDGE,"E812"),sQuery(id+"F0.wireOp",EDGE,"E813"),sQuery(id+"F0.wireOp",EDGE,"E814"),sQuery(id+"F0.wireOp",EDGE,"E815"),sQuery(id+"F0.wireOp",EDGE,"E816"),sQuery(id+"F0.wireOp",EDGE,"E817"),sQuery(id+"F0.wireOp",EDGE,"E818"),sQuery(id+"F0.wireOp",EDGE,"E819"),sQuery(id+"F0.wireOp",EDGE,"E820"),sQuery(id+"F0.wireOp",EDGE,"E821"),sQuery(id+"F0.wireOp",EDGE,"E822"),sQuery(id+"F0.wireOp",EDGE,"E823"),sQuery(id+"F0.wireOp",EDGE,"E824"),sQuery(id+"F0.wireOp",EDGE,"E825"),sQuery(id+"F0.wireOp",EDGE,"E826"),sQuery(id+"F0.wireOp",EDGE,"E827"),sQuery(id+"F0.wireOp",EDGE,"E828"),sQuery(id+"F0.wireOp",EDGE,"E829"),sQuery(id+"F0.wireOp",EDGE,"E830"),sQuery(id+"F0.wireOp",EDGE,"E831"),sQuery(id+"F0.wireOp",EDGE,"E832"),sQuery(id+"F0.wireOp",EDGE,"E833"),sQuery(id+"F0.wireOp",EDGE,"E834"),sQuery(id+"F0.wireOp",EDGE,"E835"),sQuery(id+"F0.wireOp",EDGE,"E836"),sQuery(id+"F0.wireOp",EDGE,"E837"),sQuery(id+"F0.wireOp",EDGE,"E838"),sQuery(id+"F0.wireOp",EDGE,"E839"),sQuery(id+"F0.wireOp",EDGE,"E840"),sQuery(id+"F0.wireOp",EDGE,"E841"),sQuery(id+"F0.wireOp",EDGE,"E842"),sQuery(id+"F0.wireOp",EDGE,"E843"),sQuery(id+"F0.wireOp",EDGE,"E844"),sQuery(id+"F0.wireOp",EDGE,"E845"),sQuery(id+"F0.wireOp",EDGE,"E846"),sQuery(id+"F0.wireOp",EDGE,"E847"),sQuery(id+"F0.wireOp",EDGE,"E848"),sQuery(id+"F0.wireOp",EDGE,"E849"),sQuery(id+"F0.wireOp",EDGE,"E850"),sQuery(id+"F0.wireOp",EDGE,"E851"),sQuery(id+"F0.wireOp",EDGE,"E852"),sQuery(id+"F0.wireOp",EDGE,"E853"),sQuery(id+"F0.wireOp",EDGE,"E854"),sQuery(id+"F0.wireOp",EDGE,"E855"),sQuery(id+"F0.wireOp",EDGE,"E856"),sQuery(id+"F0.wireOp",EDGE,"E857"),sQuery(id+"F0.wireOp",EDGE,"E858"),sQuery(id+"F0.wireOp",EDGE,"E859"),sQuery(id+"F0.wireOp",EDGE,"E860"),sQuery(id+"F0.wireOp",EDGE,"E861"),sQuery(id+"F0.wireOp",EDGE,"E862"),sQuery(id+"F0.wireOp",EDGE,"E863"),sQuery(id+"F0.wireOp",EDGE,"E864"),sQuery(id+"F0.wireOp",EDGE,"E865"),sQuery(id+"F0.wireOp",EDGE,"E866"),sQuery(id+"F0.wireOp",EDGE,"E867"),sQuery(id+"F0.wireOp",EDGE,"E868"),sQuery(id+"F0.wireOp",EDGE,"E869"),sQuery(id+"F0.wireOp",EDGE,"E870"),sQuery(id+"F0.wireOp",EDGE,"E871"),sQuery(id+"F0.wireOp",EDGE,"E872"),sQuery(id+"F0.wireOp",EDGE,"E873"),sQuery(id+"F0.wireOp",EDGE,"E874"),sQuery(id+"F0.wireOp",EDGE,"E875"),sQuery(id+"F0.wireOp",EDGE,"E876"),sQuery(id+"F0.wireOp",EDGE,"E877"),sQuery(id+"F0.wireOp",EDGE,"E878"),sQuery(id+"F0.wireOp",EDGE,"E879"),sQuery(id+"F0.wireOp",EDGE,"E880"),sQuery(id+"F0.wireOp",EDGE,"E881"),sQuery(id+"F0.wireOp",EDGE,"E882"),sQuery(id+"F0.wireOp",EDGE,"E883"),sQuery(id+"F0.wireOp",EDGE,"E884"),sQuery(id+"F0.wireOp",EDGE,"E885"),sQuery(id+"F0.wireOp",EDGE,"E886"),sQuery(id+"F0.wireOp",EDGE,"E887"),sQuery(id+"F0.wireOp",EDGE,"E888"),sQuery(id+"F0.wireOp",EDGE,"E889"),sQuery(id+"F0.wireOp",EDGE,"E890"),sQuery(id+"F0.wireOp",EDGE,"E891"),sQuery(id+"F0.wireOp",EDGE,"E892"),sQuery(id+"F0.wireOp",EDGE,"E893"),sQuery(id+"F0.wireOp",EDGE,"E894"),sQuery(id+"F0.wireOp",EDGE,"E895"),sQuery(id+"F0.wireOp",EDGE,"E896"),sQuery(id+"F0.wireOp",EDGE,"E897"),sQuery(id+"F0.wireOp",EDGE,"E898"),sQuery(id+"F0.wireOp",EDGE,"E899"),sQuery(id+"F0.wireOp",EDGE,"E900"),sQuery(id+"F0.wireOp",EDGE,"E901"),sQuery(id+"F0.wireOp",EDGE,"E902"),sQuery(id+"F0.wireOp",EDGE,"E903"),sQuery(id+"F0.wireOp",EDGE,"E904"),sQuery(id+"F0.wireOp",EDGE,"E905"),sQuery(id+"F0.wireOp",EDGE,"E906"),sQuery(id+"F0.wireOp",EDGE,"E907"),sQuery(id+"F0.wireOp",EDGE,"E908"),sQuery(id+"F0.wireOp",EDGE,"E909"),sQuery(id+"F0.wireOp",EDGE,"E910"),sQuery(id+"F0.wireOp",EDGE,"E911")])],"isStart":true});
            var sketch = newSketch(context, id + "F4", { "sketchPlane" : qUnion([Q0])});
            skPoint(sketch, "E913.firstSnap0", {"position": v(-35.06, 35.4) * mm});
            skLineSegment(sketch, "E913.bottom", {"start": v(-35.06, 57.42) * mm, "end": v(-31.61, 57.42) * mm});
            skLineSegment(sketch, "E913.top", {"start": v(-35.06, -57.27) * mm, "end": v(-31.61, -57.27) * mm});
            skLineSegment(sketch, "E913.left", {"start": v(-35.06, 57.42) * mm, "end": v(-35.06, -57.27) * mm});
            skLineSegment(sketch, "E913.right", {"start": v(-31.61, 57.42) * mm, "end": v(-31.61, -57.27) * mm});
            skLineSegment(sketch, "E914.bottom", {"start": v(-54.11, 57.48) * mm, "end": v(-50.66, 57.48) * mm});
            skLineSegment(sketch, "E914.top", {"start": v(-54.11, -57.12) * mm, "end": v(-50.66, -57.12) * mm});
            skLineSegment(sketch, "E914.left", {"start": v(-54.11, 57.48) * mm, "end": v(-54.11, -57.12) * mm});
            skLineSegment(sketch, "E914.right", {"start": v(-50.66, 57.48) * mm, "end": v(-50.66, -57.12) * mm});
            skLineSegment(sketch, "E915.bottom", {"start": v(-12.56, 57.64) * mm, "end": v(-16.01, 57.64) * mm});
            skLineSegment(sketch, "E915.top", {"start": v(-12.56, -57.65) * mm, "end": v(-16.01, -57.65) * mm});
            skLineSegment(sketch, "E915.left", {"start": v(-12.56, 57.64) * mm, "end": v(-12.56, -57.65) * mm});
            skLineSegment(sketch, "E915.right", {"start": v(-16.01, 57.64) * mm, "end": v(-16.01, -57.65) * mm});
            skPoint(sketch, "E916.oppositeSnap0", {"position": v(6.49, 21.74) * mm});
            skLineSegment(sketch, "E916.bottom", {"start": v(3.04, 57.9) * mm, "end": v(6.49, 57.9) * mm});
            skLineSegment(sketch, "E916.top", {"start": v(3.04, -57.52) * mm, "end": v(6.49, -57.52) * mm});
            skLineSegment(sketch, "E916.left", {"start": v(3.04, 57.9) * mm, "end": v(3.04, -57.52) * mm});
            skLineSegment(sketch, "E916.right", {"start": v(6.49, 57.9) * mm, "end": v(6.49, -57.52) * mm});
            skLineSegment(sketch, "E917.bottom", {"start": v(22.09, 57.5) * mm, "end": v(25.54, 57.5) * mm});
            skLineSegment(sketch, "E917.top", {"start": v(22.09, -57.52) * mm, "end": v(25.54, -57.52) * mm});
            skLineSegment(sketch, "E917.left", {"start": v(22.09, 57.5) * mm, "end": v(22.09, -57.52) * mm});
            skLineSegment(sketch, "E917.right", {"start": v(25.54, 57.5) * mm, "end": v(25.54, -57.52) * mm});
            skLineSegment(sketch, "E918", {"start": v(-102.13, -57.5) * mm, "end": v(98.6, -57.5) * mm, "construction": true});
            skLineSegment(sketch, "E919", {"start": v(-100.65, 57.5) * mm, "end": v(99.4, 57.5) * mm, "construction": true});
            skLineSegment(sketch, "E920.bottom", {"start": v(44.59, -57.5) * mm, "end": v(41.14, -57.5) * mm});
            skLineSegment(sketch, "E920.top", {"start": v(44.59, 57.5) * mm, "end": v(41.14, 57.5) * mm});
            skLineSegment(sketch, "E920.left", {"start": v(44.59, -57.5) * mm, "end": v(44.59, 57.5) * mm});
            skLineSegment(sketch, "E920.right", {"start": v(41.14, -57.5) * mm, "end": v(41.14, 57.5) * mm});
            skCircle(sketch, "E921", {"center": v(-52.39, 30.72) * mm, "radius": 1.72 * mm});
            skPoint(sketch, "E921.centerSnap0", {"position": v(-52.39, 57.48) * mm});
            skCircle(sketch, "E922", {"center": v(-52.39, 12.34) * mm, "radius": 1.72 * mm});
            skCircle(sketch, "E923", {"center": v(-52.39, -7.38) * mm, "radius": 1.72 * mm});
            skCircle(sketch, "E924", {"center": v(-52.39, -26.2) * mm, "radius": 1.72 * mm});
            skCircle(sketch, "E925", {"center": v(-52.39, -45.48) * mm, "radius": 1.72 * mm});
            skCircle(sketch, "E926", {"center": v(-33.34, 47.34) * mm, "radius": 1.72 * mm});
            skPoint(sketch, "E926.centerSnap0", {"position": v(-33.34, 57.42) * mm});
            skCircle(sketch, "E927", {"center": v(-33.34, 26.48) * mm, "radius": 1.72 * mm});
            skCircle(sketch, "E928", {"center": v(-33.34, -11.9) * mm, "radius": 1.72 * mm});
            skCircle(sketch, "E929", {"center": v(-33.34, -53.88) * mm, "radius": 1.72 * mm});
            skCircle(sketch, "E930", {"center": v(-14.29, 39.32) * mm, "radius": 1.72 * mm});
            skPoint(sketch, "E930.centerSnap0", {"position": v(-14.29, 57.64) * mm});
            skCircle(sketch, "E931", {"center": v(-14.29, 12.17) * mm, "radius": 1.72 * mm});
            skCircle(sketch, "E932", {"center": v(-14.29, -25.67) * mm, "radius": 1.72 * mm});
            skCircle(sketch, "E933", {"center": v(-14.29, -45.48) * mm, "radius": 1.72 * mm});
            skCircle(sketch, "E934", {"center": v(4.76, 48.17) * mm, "radius": 1.72 * mm});
            skPoint(sketch, "E934.centerSnap0", {"position": v(4.76, 57.9) * mm});
            skCircle(sketch, "E935", {"center": v(4.76, 26.48) * mm, "radius": 1.72 * mm});
            skCircle(sketch, "E936", {"center": v(4.76, -11.9) * mm, "radius": 1.72 * mm});
            skPoint(sketch, "E936.centerSnap0", {"position": v(4.76, -57.52) * mm});
            skCircle(sketch, "E937", {"center": v(4.76, -53.88) * mm, "radius": 1.72 * mm});
            skPoint(sketch, "E938.centerSnap0", {"position": v(-11.76, 40.48) * mm});
            skPoint(sketch, "E938.centerSnap1", {"position": v(23.81, 57.5) * mm});
            skCircle(sketch, "E939", {"center": v(23.81, -21.25) * mm, "radius": 1.72 * mm});
            skPoint(sketch, "E939.centerSnap0", {"position": v(23.81, -57.52) * mm});
            skCircle(sketch, "E940", {"center": v(23.81, 16.45) * mm, "radius": 1.72 * mm});
            skCircle(sketch, "E941", {"center": v(23.81, 44.93) * mm, "radius": 1.72 * mm});
            skPoint(sketch, "E941.centerSnap0", {"position": v(3.04, 44.93) * mm});
            skCircle(sketch, "E942", {"center": v(23.81, -45.48) * mm, "radius": 1.72 * mm});
            skCircle(sketch, "E943", {"center": v(42.86, 44.93) * mm, "radius": 1.72 * mm});
            skPoint(sketch, "E943.centerSnap0", {"position": v(42.86, 57.5) * mm});
            skCircle(sketch, "E944", {"center": v(42.86, 26.35) * mm, "radius": 1.72 * mm});
            skCircle(sketch, "E945", {"center": v(42.86, -2.8) * mm, "radius": 1.72 * mm});
            skCircle(sketch, "E946", {"center": v(42.86, -53.88) * mm, "radius": 1.72 * mm});
            skLineSegment(sketch, "E947.bottom", {"start": v(59.39, -28.06) * mm, "end": v(69.2, -28.06) * mm, "construction": true});
            skLineSegment(sketch, "E947.top", {"start": v(59.39, -33.86) * mm, "end": v(69.2, -33.86) * mm, "construction": true});
            skLineSegment(sketch, "E947.left", {"start": v(59.39, -28.06) * mm, "end": v(59.39, -33.86) * mm, "construction": true});
            skLineSegment(sketch, "E947.right", {"start": v(69.2, -28.06) * mm, "end": v(69.2, -33.86) * mm, "construction": true});
            skCircle(sketch, "E948", {"center": v(64.3, -30.96) * mm, "radius": 1.72 * mm});
            skPoint(sketch, "E948.centerSnap0", {"position": v(59.39, -30.96) * mm});
            skPoint(sketch, "E948.centerSnap1", {"position": v(64.3, -28.06) * mm});
            skCircle(sketch, "E949", {"center": v(61.91, 7.63) * mm, "radius": 1.72 * mm});
            skCircle(sketch, "E950", {"center": v(64.3, 35.57) * mm, "radius": 1.72 * mm});
            skPoint(sketch, "E950.centerSnap0", {"position": v(64.3, 38.24) * mm});
            skCircle(sketch, "E951", {"center": v(-52.39, 30.72) * mm, "radius": 1 * mm});
            skCircle(sketch, "E952", {"center": v(-52.39, 12.34) * mm, "radius": 1 * mm});
            skCircle(sketch, "E953", {"center": v(-52.39, -7.38) * mm, "radius": 1 * mm});
            skCircle(sketch, "E954", {"center": v(-52.39, -26.2) * mm, "radius": 1 * mm});
            skCircle(sketch, "E955", {"center": v(-52.39, -45.48) * mm, "radius": 1 * mm});
            skCircle(sketch, "E956", {"center": v(-33.34, 47.34) * mm, "radius": 1 * mm});
            skCircle(sketch, "E957", {"center": v(-33.34, 26.48) * mm, "radius": 1 * mm});
            skCircle(sketch, "E958", {"center": v(-33.34, -11.9) * mm, "radius": 1 * mm});
            skCircle(sketch, "E959", {"center": v(-33.34, -53.88) * mm, "radius": 1 * mm});
            skCircle(sketch, "E960", {"center": v(-14.29, -45.48) * mm, "radius": 1 * mm});
            skCircle(sketch, "E961", {"center": v(-14.29, -25.67) * mm, "radius": 1 * mm});
            skCircle(sketch, "E962", {"center": v(-14.29, 12.17) * mm, "radius": 1 * mm});
            skCircle(sketch, "E963", {"center": v(-14.29, 39.32) * mm, "radius": 1 * mm});
            skCircle(sketch, "E964", {"center": v(4.76, 48.17) * mm, "radius": 1 * mm});
            skCircle(sketch, "E965", {"center": v(4.76, 26.48) * mm, "radius": 1 * mm});
            skCircle(sketch, "E966", {"center": v(4.76, -11.9) * mm, "radius": 1 * mm});
            skCircle(sketch, "E967", {"center": v(4.76, -53.88) * mm, "radius": 1 * mm});
            skCircle(sketch, "E968", {"center": v(23.81, -45.48) * mm, "radius": 1 * mm});
            skCircle(sketch, "E969", {"center": v(23.81, -21.25) * mm, "radius": 1 * mm});
            skCircle(sketch, "E970", {"center": v(42.86, -53.88) * mm, "radius": 1 * mm});
            skCircle(sketch, "E971", {"center": v(42.86, -2.8) * mm, "radius": 1 * mm});
            skCircle(sketch, "E972", {"center": v(23.81, 16.45) * mm, "radius": 1 * mm});
            skCircle(sketch, "E973", {"center": v(42.86, 26.35) * mm, "radius": 1 * mm});
            skCircle(sketch, "E974", {"center": v(23.81, 44.93) * mm, "radius": 1 * mm});
            skCircle(sketch, "E975", {"center": v(42.86, 44.93) * mm, "radius": 1 * mm});
            skCircle(sketch, "E976", {"center": v(64.3, 35.57) * mm, "radius": 1 * mm});
            skCircle(sketch, "E977", {"center": v(61.91, 7.63) * mm, "radius": 1 * mm});
            skCircle(sketch, "E978", {"center": v(64.3, -30.96) * mm, "radius": 1 * mm});
            skLineSegment(sketch, "E979", {"start": v(93.22, 64.28) * mm, "end": v(93.22, -63.45) * mm, "construction": true});
            skLineSegment(sketch, "E980", {"start": v(-93.22, 64.43) * mm, "end": v(-93.22, -64.48) * mm, "construction": true});
            skPoint(sketch, "E981.first.point", {"position": v(-93.22, 57.5) * mm});
            skPoint(sketch, "E981.second.point", {"position": v(-93.22, 57.5) * mm});
            skCircle(sketch, "E982", {"center": v(-91.3, 55.57) * mm, "radius": 2 * mm});
            skPoint(sketch, "E982.first.point", {"position": v(-89.45, 54.8) * mm});
            skPoint(sketch, "E982.second.point", {"position": v(-93.22, 55) * mm});
            skPoint(sketch, "E982.third.point", {"position": v(-91.81, 57.5) * mm});
            skCircle(sketch, "E983", {"center": v(-91.3, 55.57) * mm, "radius": 1 * mm});
            skCircle(sketch, "E984", {"center": v(-91.23, -55.54) * mm, "radius": 2 * mm});
            skPoint(sketch, "E984.first.point", {"position": v(-90.28, -53.78) * mm});
            skPoint(sketch, "E984.second.point", {"position": v(-90.83, -57.5) * mm});
            skPoint(sketch, "E984.third.point", {"position": v(-93.22, -55.36) * mm});
            skCircle(sketch, "E985", {"center": v(-91.23, -55.54) * mm, "radius": 1 * mm});
            skCircle(sketch, "E986", {"center": v(91.22, -55.5) * mm, "radius": 2 * mm});
            skPoint(sketch, "E986.first.point", {"position": v(89.23, -55.34) * mm});
            skPoint(sketch, "E986.second.point", {"position": v(93.22, -55.38) * mm});
            skPoint(sketch, "E986.third.point", {"position": v(91.28, -57.5) * mm});
            skCircle(sketch, "E987", {"center": v(91.22, -55.5) * mm, "radius": 1 * mm});
            skCircle(sketch, "E988", {"center": v(91.31, 55.6) * mm, "radius": 2 * mm});
            skPoint(sketch, "E988.first.point", {"position": v(89.54, 54.67) * mm});
            skPoint(sketch, "E988.second.point", {"position": v(93.22, 55) * mm});
            skPoint(sketch, "E988.third.point", {"position": v(90.7, 57.5) * mm});
            skCircle(sketch, "E989", {"center": v(91.31, 55.6) * mm, "radius": 1 * mm});
            skLineSegment(sketch, "E990", {"start": v(6.5, -2.37) * mm, "end": v(109.11, -2.37) * mm, "construction": true});
            skLineSegment(sketch, "E991.bottom", {"start": v(6.5, -1.33) * mm, "end": v(93.22, -1.33) * mm});
            skLineSegment(sketch, "E991.top", {"start": v(6.5, -3.33) * mm, "end": v(93.22, -3.33) * mm});
            skLineSegment(sketch, "E991.left", {"start": v(6.5, -1.33) * mm, "end": v(6.5, -3.33) * mm});
            skLineSegment(sketch, "E991.right", {"start": v(93.22, -1.33) * mm, "end": v(93.22, -3.33) * mm});
            skLineSegment(sketch, "E992.bottom", {"start": v(6.49, 17.84) * mm, "end": v(93.22, 17.84) * mm});
            skLineSegment(sketch, "E992.top", {"start": v(6.49, 15.84) * mm, "end": v(93.22, 15.84) * mm});
            skLineSegment(sketch, "E992.left", {"start": v(6.49, 17.84) * mm, "end": v(6.49, 15.84) * mm});
            skLineSegment(sketch, "E992.right", {"start": v(93.22, 17.84) * mm, "end": v(93.22, 15.84) * mm});
            skCircle(sketch, "E993", {"center": v(91.3, 8.36) * mm, "radius": 2 * mm});
            skPoint(sketch, "E993.first.point", {"position": v(89.3, 8.55) * mm});
            skPoint(sketch, "E993.second.point", {"position": v(90.4, 6.58) * mm});
            skPoint(sketch, "E993.third.point", {"position": v(93.22, 7.82) * mm});
            skCircle(sketch, "E994", {"center": v(91.3, 8.36) * mm, "radius": 1 * mm});
            skLineSegment(sketch, "E995", {"start": v(108.43, 8.36) * mm, "end": v(36.7, 6.58) * mm, "construction": true});
            skCircle(sketch, "E996", {"center": v(-91.22, 3.4) * mm, "radius": 2 * mm});
            skCircle(sketch, "E997", {"center": v(-91.22, 3.4) * mm, "radius": 1 * mm});
            skLineSegment(sketch, "E998.bottom", {"start": v(-31.61, 8.3) * mm, "end": v(-16.01, 8.3) * mm});
            skLineSegment(sketch, "E998.top", {"start": v(-31.61, 6.3) * mm, "end": v(-16.01, 6.3) * mm});
            skLineSegment(sketch, "E998.left", {"start": v(-31.61, 8.3) * mm, "end": v(-31.61, 6.3) * mm});
            skLineSegment(sketch, "E998.right", {"start": v(-16.01, 8.3) * mm, "end": v(-16.01, 6.3) * mm});
            skLineSegment(sketch, "E999.bottom", {"start": v(-31.61, -10.9) * mm, "end": v(-16.01, -10.9) * mm});
            skLineSegment(sketch, "E999.top", {"start": v(-31.61, -12.9) * mm, "end": v(-16.01, -12.9) * mm});
            skLineSegment(sketch, "E999.left", {"start": v(-31.61, -10.9) * mm, "end": v(-31.61, -12.9) * mm});
            skLineSegment(sketch, "E999.right", {"start": v(-16.01, -10.9) * mm, "end": v(-16.01, -12.9) * mm});
            skLineSegment(sketch, "E1000.bottom", {"start": v(-50.66, 22.44) * mm, "end": v(-35.06, 22.44) * mm});
            skLineSegment(sketch, "E1000.top", {"start": v(-50.66, 20.44) * mm, "end": v(-35.06, 20.44) * mm});
            skLineSegment(sketch, "E1000.left", {"start": v(-50.66, 22.44) * mm, "end": v(-50.66, 20.44) * mm});
            skLineSegment(sketch, "E1000.right", {"start": v(-35.06, 22.44) * mm, "end": v(-35.06, 20.44) * mm});
            skLineSegment(sketch, "E1001.bottom", {"start": v(-50.66, 3.48) * mm, "end": v(-35.06, 3.48) * mm});
            skLineSegment(sketch, "E1001.top", {"start": v(-50.66, 1.48) * mm, "end": v(-35.06, 1.48) * mm});
            skLineSegment(sketch, "E1001.left", {"start": v(-50.66, 3.48) * mm, "end": v(-50.66, 1.48) * mm});
            skLineSegment(sketch, "E1001.right", {"start": v(-35.06, 3.48) * mm, "end": v(-35.06, 1.48) * mm});
            skLineSegment(sketch, "E1002.bottom", {"start": v(-93.22, -25.17) * mm, "end": v(-54.11, -25.17) * mm});
            skLineSegment(sketch, "E1002.top", {"start": v(-93.22, -27.17) * mm, "end": v(-54.11, -27.17) * mm});
            skLineSegment(sketch, "E1002.left", {"start": v(-93.22, -25.17) * mm, "end": v(-93.22, -27.17) * mm});
            skLineSegment(sketch, "E1002.right", {"start": v(-54.11, -25.17) * mm, "end": v(-54.11, -27.17) * mm});
            skLineSegment(sketch, "E1003.bottom", {"start": v(-12.56, 32.17) * mm, "end": v(3.04, 32.17) * mm});
            skLineSegment(sketch, "E1003.top", {"start": v(-12.56, 30.17) * mm, "end": v(3.04, 30.17) * mm});
            skLineSegment(sketch, "E1003.left", {"start": v(-12.56, 32.17) * mm, "end": v(-12.56, 30.17) * mm});
            skLineSegment(sketch, "E1003.right", {"start": v(3.04, 32.17) * mm, "end": v(3.04, 30.17) * mm});
            skLineSegment(sketch, "E1004.bottom", {"start": v(-12.56, -6.1) * mm, "end": v(3.04, -6.1) * mm});
            skLineSegment(sketch, "E1004.top", {"start": v(-12.56, -8.1) * mm, "end": v(3.04, -8.1) * mm});
            skLineSegment(sketch, "E1004.left", {"start": v(-12.56, -6.1) * mm, "end": v(-12.56, -8.1) * mm});
            skLineSegment(sketch, "E1004.right", {"start": v(3.04, -6.1) * mm, "end": v(3.04, -8.1) * mm});
            skSolve(sketch);
        }
        {
            var Q0;
            {var subQ0=sQuery(id+"F4.wireOp",EDGE,"E921");var subQ1=makeQuery(id+"F4.imprint","INTERSECT",VERTEX,{"derivedFrom":[sQuery(id+"F4.wireOp",EDGE,"E914.left"),subQ0]});Q0=makeQuery(id+"F4.imprint","IMPRINT",FACE,{"disambiguationData":[TD([[makeQuery(id+"F4.imprint","IMPRINT",EDGE,{"disambiguationData":[TD([[subQ1,1.0]])],"derivedFrom":subQ0}),1.0]])]});}
            var Q1;
            {var subQ6=sQuery(id+"F4.wireOp",EDGE,"E921");var subQ8=sQuery(id+"F4.wireOp",EDGE,"E914.left");var subQ11=makeQuery(id+"F4.imprint","INTERSECT",VERTEX,{"derivedFrom":[subQ8,subQ6]});var subQ15=makeQuery(id+"F4.imprint","INTERSECT",VERTEX,{"derivedFrom":[makeQuery(id+"F1.opExtrude","CAP_EDGE",EDGE,{"disambiguationData":[OSD([sQuery(id+"F0.wireOp",EDGE,"E187")])],"isStart":true}),subQ8]});Q1=makeQuery(id+"F4.imprint","IMPRINT",FACE,{"disambiguationData":[TD([[makeQuery(id+"F4.imprint","IMPRINT",EDGE,{"disambiguationData":[TD([[subQ15,1.0],[subQ11,-1.0]])],"derivedFrom":subQ8}),1.0]])]});}
            var Q2;
            {var subQ2=sQuery(id+"F4.wireOp",EDGE,"E914.bottom");Q2=makeQuery(id+"F4.imprint","IMPRINT",FACE,{"disambiguationData":[TD([[makeQuery(id+"F4.imprint","IMPRINT",EDGE,{"derivedFrom":subQ2}),-1.0]])]});}
            var Q3;
            {var subQ0=sQuery(id+"F4.wireOp",EDGE,"E924");var subQ1=makeQuery(id+"F4.imprint","INTERSECT",VERTEX,{"derivedFrom":[sQuery(id+"F4.wireOp",EDGE,"E914.left"),subQ0]});Q3=makeQuery(id+"F4.imprint","IMPRINT",FACE,{"disambiguationData":[TD([[makeQuery(id+"F4.imprint","IMPRINT",EDGE,{"disambiguationData":[TD([[subQ1,1.0]])],"derivedFrom":subQ0}),1.0]])]});}
            var Q4;
            {var subQ0=sQuery(id+"F4.wireOp",EDGE,"E923");var subQ1=makeQuery(id+"F4.imprint","INTERSECT",VERTEX,{"derivedFrom":[sQuery(id+"F4.wireOp",EDGE,"E914.left"),subQ0]});Q4=makeQuery(id+"F4.imprint","IMPRINT",FACE,{"disambiguationData":[TD([[makeQuery(id+"F4.imprint","IMPRINT",EDGE,{"disambiguationData":[TD([[subQ1,1.0]])],"derivedFrom":subQ0}),1.0]])]});}
            var Q5;
            {var subQ0=sQuery(id+"F4.wireOp",EDGE,"E925");var subQ1=makeQuery(id+"F4.imprint","INTERSECT",VERTEX,{"derivedFrom":[sQuery(id+"F4.wireOp",EDGE,"E914.left"),subQ0]});Q5=makeQuery(id+"F4.imprint","IMPRINT",FACE,{"disambiguationData":[TD([[makeQuery(id+"F4.imprint","IMPRINT",EDGE,{"disambiguationData":[TD([[subQ1,1.0]])],"derivedFrom":subQ0}),1.0]])]});}
            var Q6;
            {var subQ6=sQuery(id+"F4.wireOp",EDGE,"E914.top");Q6=makeQuery(id+"F4.imprint","IMPRINT",FACE,{"disambiguationData":[TD([[makeQuery(id+"F4.imprint","IMPRINT",EDGE,{"derivedFrom":subQ6}),1.0]])]});}
            var Q7;
            {var subQ5=sQuery(id+"F4.wireOp",EDGE,"E922");var subQ7=sQuery(id+"F4.wireOp",EDGE,"E914.left");var subQ12=makeQuery(id+"F4.imprint","INTERSECT",VERTEX,{"derivedFrom":[makeQuery(id+"F1.opExtrude","CAP_EDGE",EDGE,{"disambiguationData":[OSD([sQuery(id+"F0.wireOp",EDGE,"E167")])],"isStart":true}),subQ7]});var subQ15=makeQuery(id+"F4.imprint","INTERSECT",VERTEX,{"derivedFrom":[subQ7,subQ5]});Q7=makeQuery(id+"F4.imprint","IMPRINT",FACE,{"disambiguationData":[TD([[makeQuery(id+"F4.imprint","IMPRINT",EDGE,{"disambiguationData":[TD([[subQ12,1.0],[subQ15,-1.0]])],"derivedFrom":subQ7}),1.0]])]});}
            var Q8;
            {var subQ0=sQuery(id+"F4.wireOp",EDGE,"E922");var subQ1=makeQuery(id+"F4.imprint","INTERSECT",VERTEX,{"derivedFrom":[sQuery(id+"F4.wireOp",EDGE,"E914.left"),subQ0]});Q8=makeQuery(id+"F4.imprint","IMPRINT",FACE,{"disambiguationData":[TD([[makeQuery(id+"F4.imprint","IMPRINT",EDGE,{"disambiguationData":[TD([[subQ1,1.0]])],"derivedFrom":subQ0}),1.0]])]});}
            var Q9;
            {var subQ5=sQuery(id+"F4.wireOp",EDGE,"E914.left");var subQ6=makeQuery(id+"F4.imprint","INTERSECT",VERTEX,{"derivedFrom":[makeQuery(id+"F1.opExtrude","CAP_EDGE",EDGE,{"disambiguationData":[OSD([sQuery(id+"F0.wireOp",EDGE,"E121")])],"isStart":true}),subQ5]});var subQ7=makeQuery(id+"F4.imprint","INTERSECT",VERTEX,{"derivedFrom":[makeQuery(id+"F1.opExtrude","CAP_EDGE",EDGE,{"disambiguationData":[OSD([sQuery(id+"F0.wireOp",EDGE,"E123")])],"isStart":true}),subQ5]});Q9=makeQuery(id+"F4.imprint","IMPRINT",FACE,{"disambiguationData":[TD([[makeQuery(id+"F4.imprint","IMPRINT",EDGE,{"disambiguationData":[TD([[subQ6,-1.0],[subQ7,1.0]])],"derivedFrom":subQ5}),-1.0]])]});}
            var Q10;
            {var subQ9=sQuery(id+"F4.wireOp",EDGE,"E914.left");var subQ10=makeQuery(id+"F4.imprint","INTERSECT",VERTEX,{"derivedFrom":[makeQuery(id+"F1.opExtrude","CAP_EDGE",EDGE,{"disambiguationData":[OSD([sQuery(id+"F0.wireOp",EDGE,"E141")])],"isStart":true}),subQ9]});var subQ15=makeQuery(id+"F4.imprint","INTERSECT",VERTEX,{"derivedFrom":[makeQuery(id+"F1.opExtrude","CAP_EDGE",EDGE,{"disambiguationData":[OSD([sQuery(id+"F0.wireOp",EDGE,"E143")])],"isStart":true}),subQ9]});Q10=makeQuery(id+"F4.imprint","IMPRINT",FACE,{"disambiguationData":[TD([[makeQuery(id+"F4.imprint","IMPRINT",EDGE,{"disambiguationData":[TD([[subQ10,-1.0],[subQ15,1.0]])],"derivedFrom":subQ9}),-1.0]])]});}
            var Q11;
            {var subQ0=sQuery(id+"F4.wireOp",EDGE,"E913.bottom");Q11=makeQuery(id+"F4.imprint","IMPRINT",FACE,{"disambiguationData":[TD([[makeQuery(id+"F4.imprint","IMPRINT",EDGE,{"derivedFrom":subQ0}),-1.0]])]});}
            var Q12;
            {var subQ0=sQuery(id+"F4.wireOp",EDGE,"E926");var subQ1=makeQuery(id+"F4.imprint","INTERSECT",VERTEX,{"derivedFrom":[sQuery(id+"F4.wireOp",EDGE,"E913.left"),subQ0]});Q12=makeQuery(id+"F4.imprint","IMPRINT",FACE,{"disambiguationData":[TD([[makeQuery(id+"F4.imprint","IMPRINT",EDGE,{"disambiguationData":[TD([[subQ1,1.0]])],"derivedFrom":subQ0}),1.0]])]});}
            var Q13;
            {var subQ6=sQuery(id+"F4.wireOp",EDGE,"E926");var subQ9=sQuery(id+"F4.wireOp",EDGE,"E913.left");var subQ12=makeQuery(id+"F4.imprint","INTERSECT",VERTEX,{"derivedFrom":[subQ9,subQ6]});var subQ14=makeQuery(id+"F4.imprint","INTERSECT",VERTEX,{"derivedFrom":[makeQuery(id+"F1.opExtrude","CAP_EDGE",EDGE,{"disambiguationData":[OSD([sQuery(id+"F0.wireOp",EDGE,"E287")])],"isStart":true}),subQ9]});Q13=makeQuery(id+"F4.imprint","IMPRINT",FACE,{"disambiguationData":[TD([[makeQuery(id+"F4.imprint","IMPRINT",EDGE,{"disambiguationData":[TD([[subQ14,1.0],[subQ12,-1.0]])],"derivedFrom":subQ9}),1.0]])]});}
            var Q14;
            {var subQ0=sQuery(id+"F4.wireOp",EDGE,"E927");var subQ1=makeQuery(id+"F4.imprint","INTERSECT",VERTEX,{"derivedFrom":[sQuery(id+"F4.wireOp",EDGE,"E913.left"),subQ0]});Q14=makeQuery(id+"F4.imprint","IMPRINT",FACE,{"disambiguationData":[TD([[makeQuery(id+"F4.imprint","IMPRINT",EDGE,{"disambiguationData":[TD([[subQ1,1.0]])],"derivedFrom":subQ0}),1.0]])]});}
            var Q15;
            {var subQ0=sQuery(id+"F4.wireOp",EDGE,"E913.left");var subQ10=makeQuery(id+"F4.imprint","INTERSECT",VERTEX,{"derivedFrom":[makeQuery(id+"F1.opExtrude","CAP_EDGE",EDGE,{"disambiguationData":[OSD([sQuery(id+"F0.wireOp",EDGE,"E267")])],"isStart":true}),subQ0]});var subQ14=makeQuery(id+"F4.imprint","INTERSECT",VERTEX,{"derivedFrom":[makeQuery(id+"F1.opExtrude","CAP_EDGE",EDGE,{"disambiguationData":[OSD([sQuery(id+"F0.wireOp",EDGE,"E281")])],"isStart":true}),subQ0]});Q15=makeQuery(id+"F4.imprint","IMPRINT",FACE,{"disambiguationData":[TD([[makeQuery(id+"F4.imprint","IMPRINT",EDGE,{"disambiguationData":[TD([[subQ10,1.0],[subQ14,-1.0]])],"derivedFrom":subQ0}),1.0]])]});}
            var Q16;
            {var subQ0=sQuery(id+"F4.wireOp",EDGE,"E928");var subQ1=makeQuery(id+"F4.imprint","INTERSECT",VERTEX,{"derivedFrom":[sQuery(id+"F4.wireOp",EDGE,"E913.left"),subQ0]});Q16=makeQuery(id+"F4.imprint","IMPRINT",FACE,{"disambiguationData":[TD([[makeQuery(id+"F4.imprint","IMPRINT",EDGE,{"disambiguationData":[TD([[subQ1,1.0]])],"derivedFrom":subQ0}),1.0]])]});}
            var Q17;
            {var subQ0=sQuery(id+"F4.wireOp",EDGE,"E913.left");var subQ1=makeQuery(id+"F4.imprint","INTERSECT",VERTEX,{"derivedFrom":[makeQuery(id+"F1.opExtrude","CAP_EDGE",EDGE,{"disambiguationData":[OSD([sQuery(id+"F0.wireOp",EDGE,"E201")])],"isStart":true}),subQ0]});var subQ4=makeQuery(id+"F4.imprint","INTERSECT",VERTEX,{"derivedFrom":[makeQuery(id+"F1.opExtrude","CAP_EDGE",EDGE,{"disambiguationData":[OSD([sQuery(id+"F0.wireOp",EDGE,"E203")])],"isStart":true}),subQ0]});Q17=makeQuery(id+"F4.imprint","IMPRINT",FACE,{"disambiguationData":[TD([[makeQuery(id+"F4.imprint","IMPRINT",EDGE,{"disambiguationData":[TD([[subQ1,-1.0],[subQ4,1.0]])],"derivedFrom":subQ0}),-1.0]])]});}
            var Q18;
            {var subQ0=sQuery(id+"F4.wireOp",EDGE,"E913.top");Q18=makeQuery(id+"F4.imprint","IMPRINT",FACE,{"disambiguationData":[TD([[makeQuery(id+"F4.imprint","IMPRINT",EDGE,{"derivedFrom":subQ0}),1.0]])]});}
            var Q19;
            {var subQ0=sQuery(id+"F4.wireOp",EDGE,"E929");var subQ1=makeQuery(id+"F4.imprint","INTERSECT",VERTEX,{"derivedFrom":[sQuery(id+"F4.wireOp",EDGE,"E913.left"),subQ0]});Q19=makeQuery(id+"F4.imprint","IMPRINT",FACE,{"disambiguationData":[TD([[makeQuery(id+"F4.imprint","IMPRINT",EDGE,{"disambiguationData":[TD([[subQ1,1.0]])],"derivedFrom":subQ0}),1.0]])]});}
            var Q20;
            {var subQ5=sQuery(id+"F4.wireOp",EDGE,"E915.bottom");Q20=makeQuery(id+"F4.imprint","IMPRINT",FACE,{"disambiguationData":[TD([[makeQuery(id+"F4.imprint","IMPRINT",EDGE,{"derivedFrom":subQ5}),1.0]])]});}
            var Q21;
            {var subQ0=sQuery(id+"F4.wireOp",EDGE,"E930");var subQ1=makeQuery(id+"F4.imprint","INTERSECT",VERTEX,{"derivedFrom":[sQuery(id+"F4.wireOp",EDGE,"E915.left"),subQ0]});Q21=makeQuery(id+"F4.imprint","IMPRINT",FACE,{"disambiguationData":[TD([[makeQuery(id+"F4.imprint","IMPRINT",EDGE,{"disambiguationData":[TD([[subQ1,-1.0]])],"derivedFrom":subQ0}),1.0]])]});}
            var Q22;
            {var subQ5=sQuery(id+"F4.wireOp",EDGE,"E915.left");var subQ8=makeQuery(id+"F4.imprint","INTERSECT",VERTEX,{"derivedFrom":[makeQuery(id+"F1.opExtrude","CAP_EDGE",EDGE,{"disambiguationData":[OSD([sQuery(id+"F0.wireOp",EDGE,"E475")])],"isStart":true}),subQ5]});Q22=makeQuery(id+"F4.imprint","IMPRINT",FACE,{"disambiguationData":[TD([[makeQuery(id+"F4.imprint","IMPRINT",EDGE,{"disambiguationData":[TD([[subQ8,1.0]])],"derivedFrom":subQ5}),-1.0]])]});}
            var Q23;
            {var subQ0=sQuery(id+"F4.wireOp",EDGE,"E931");var subQ1=makeQuery(id+"F4.imprint","INTERSECT",VERTEX,{"derivedFrom":[sQuery(id+"F4.wireOp",EDGE,"E915.left"),subQ0]});Q23=makeQuery(id+"F4.imprint","IMPRINT",FACE,{"disambiguationData":[TD([[makeQuery(id+"F4.imprint","IMPRINT",EDGE,{"disambiguationData":[TD([[subQ1,-1.0]])],"derivedFrom":subQ0}),1.0]])]});}
            var Q24;
            {var subQ0=sQuery(id+"F4.wireOp",EDGE,"E915.left");var subQ9=makeQuery(id+"F4.imprint","INTERSECT",VERTEX,{"derivedFrom":[makeQuery(id+"F1.opExtrude","CAP_EDGE",EDGE,{"disambiguationData":[OSD([sQuery(id+"F0.wireOp",EDGE,"E431")])],"isStart":true}),subQ0]});Q24=makeQuery(id+"F4.imprint","IMPRINT",FACE,{"disambiguationData":[TD([[makeQuery(id+"F4.imprint","IMPRINT",EDGE,{"disambiguationData":[TD([[subQ9,1.0]])],"derivedFrom":subQ0}),-1.0]])]});}
            var Q25;
            {var subQ0=sQuery(id+"F4.wireOp",EDGE,"E932");var subQ1=makeQuery(id+"F4.imprint","INTERSECT",VERTEX,{"derivedFrom":[sQuery(id+"F4.wireOp",EDGE,"E915.left"),subQ0]});Q25=makeQuery(id+"F4.imprint","IMPRINT",FACE,{"disambiguationData":[TD([[makeQuery(id+"F4.imprint","IMPRINT",EDGE,{"disambiguationData":[TD([[subQ1,-1.0]])],"derivedFrom":subQ0}),1.0]])]});}
            var Q26;
            {var subQ6=sQuery(id+"F4.wireOp",EDGE,"E915.left");var subQ12=makeQuery(id+"F4.imprint","INTERSECT",VERTEX,{"derivedFrom":[makeQuery(id+"F1.opExtrude","CAP_EDGE",EDGE,{"disambiguationData":[OSD([sQuery(id+"F0.wireOp",EDGE,"E395")])],"isStart":true}),subQ6]});Q26=makeQuery(id+"F4.imprint","IMPRINT",FACE,{"disambiguationData":[TD([[makeQuery(id+"F4.imprint","IMPRINT",EDGE,{"disambiguationData":[TD([[subQ12,-1.0]])],"derivedFrom":subQ6}),-1.0]])]});}
            var Q27;
            {var subQ0=sQuery(id+"F4.wireOp",EDGE,"E933");var subQ1=makeQuery(id+"F4.imprint","INTERSECT",VERTEX,{"derivedFrom":[sQuery(id+"F4.wireOp",EDGE,"E915.left"),subQ0]});Q27=makeQuery(id+"F4.imprint","IMPRINT",FACE,{"disambiguationData":[TD([[makeQuery(id+"F4.imprint","IMPRINT",EDGE,{"disambiguationData":[TD([[subQ1,-1.0]])],"derivedFrom":subQ0}),1.0]])]});}
            var Q28;
            {var subQ1=sQuery(id+"F4.wireOp",EDGE,"E915.top");Q28=makeQuery(id+"F4.imprint","IMPRINT",FACE,{"disambiguationData":[TD([[makeQuery(id+"F4.imprint","IMPRINT",EDGE,{"derivedFrom":subQ1}),-1.0]])]});}
            var Q29;
            {var subQ5=sQuery(id+"F4.wireOp",EDGE,"E916.bottom");Q29=makeQuery(id+"F4.imprint","IMPRINT",FACE,{"disambiguationData":[TD([[makeQuery(id+"F4.imprint","IMPRINT",EDGE,{"derivedFrom":subQ5}),-1.0]])]});}
            var Q30;
            {var subQ0=sQuery(id+"F4.wireOp",EDGE,"E934");var subQ1=sQuery(id+"F4.wireOp",EDGE,"E916.left");var subQ2=makeQuery(id+"F4.imprint","INTERSECT",VERTEX,{"disambiguationData":[OD(0.0)],"derivedFrom":[subQ1,subQ0]});var subQ3=makeQuery(id+"F4.imprint","INTERSECT",VERTEX,{"disambiguationData":[OD(1.0)],"derivedFrom":[subQ1,subQ0]});Q30=makeQuery(id+"F4.imprint","IMPRINT",FACE,{"disambiguationData":[TD([[makeQuery(id+"F4.imprint","IMPRINT",EDGE,{"disambiguationData":[TD([[subQ2,-1.0],[subQ3,1.0]])],"derivedFrom":subQ1}),1.0]])]});}
            var Q31;
            {var subQ6=sQuery(id+"F4.wireOp",EDGE,"E916.left");var subQ9=sQuery(id+"F4.wireOp",EDGE,"E934");var subQ14=makeQuery(id+"F4.imprint","INTERSECT",VERTEX,{"derivedFrom":[makeQuery(id+"F1.opExtrude","CAP_EDGE",EDGE,{"disambiguationData":[OSD([sQuery(id+"F0.wireOp",EDGE,"E487")])],"isStart":true}),subQ6]});var subQ15=makeQuery(id+"F4.imprint","INTERSECT",VERTEX,{"disambiguationData":[OD(1.0)],"derivedFrom":[subQ6,subQ9]});Q31=makeQuery(id+"F4.imprint","IMPRINT",FACE,{"disambiguationData":[TD([[makeQuery(id+"F4.imprint","IMPRINT",EDGE,{"disambiguationData":[TD([[subQ14,1.0],[subQ15,-1.0]])],"derivedFrom":subQ6}),1.0]])]});}
            var Q32;
            {var subQ0=sQuery(id+"F4.wireOp",EDGE,"E935");var subQ1=makeQuery(id+"F4.imprint","INTERSECT",VERTEX,{"derivedFrom":[sQuery(id+"F4.wireOp",EDGE,"E916.left"),subQ0]});Q32=makeQuery(id+"F4.imprint","IMPRINT",FACE,{"disambiguationData":[TD([[makeQuery(id+"F4.imprint","IMPRINT",EDGE,{"disambiguationData":[TD([[subQ1,1.0]])],"derivedFrom":subQ0}),1.0]])]});}
            var Q33;
            {var subQ4=sQuery(id+"F4.wireOp",EDGE,"E916.left");var subQ7=makeQuery(id+"F4.imprint","INTERSECT",VERTEX,{"derivedFrom":[makeQuery(id+"F1.opExtrude","CAP_EDGE",EDGE,{"disambiguationData":[OSD([sQuery(id+"F0.wireOp",EDGE,"E465")])],"isStart":true}),subQ4]});var subQ10=makeQuery(id+"F4.imprint","INTERSECT",VERTEX,{"derivedFrom":[makeQuery(id+"F1.opExtrude","CAP_EDGE",EDGE,{"disambiguationData":[OSD([sQuery(id+"F0.wireOp",EDGE,"E463")])],"isStart":true}),subQ4]});Q33=makeQuery(id+"F4.imprint","IMPRINT",FACE,{"disambiguationData":[TD([[makeQuery(id+"F4.imprint","IMPRINT",EDGE,{"disambiguationData":[TD([[subQ10,1.0],[subQ7,-1.0]])],"derivedFrom":subQ4}),1.0]])]});}
            var Q34;
            {var subQ0=sQuery(id+"F4.wireOp",EDGE,"E936");var subQ1=makeQuery(id+"F4.imprint","INTERSECT",VERTEX,{"derivedFrom":[sQuery(id+"F4.wireOp",EDGE,"E916.left"),subQ0]});Q34=makeQuery(id+"F4.imprint","IMPRINT",FACE,{"disambiguationData":[TD([[makeQuery(id+"F4.imprint","IMPRINT",EDGE,{"disambiguationData":[TD([[subQ1,1.0]])],"derivedFrom":subQ0}),1.0]])]});}
            var Q35;
            {var subQ3=sQuery(id+"F4.wireOp",EDGE,"E916.left");var subQ9=makeQuery(id+"F4.imprint","INTERSECT",VERTEX,{"derivedFrom":[makeQuery(id+"F1.opExtrude","CAP_EDGE",EDGE,{"disambiguationData":[OSD([sQuery(id+"F0.wireOp",EDGE,"E425")])],"isStart":true}),subQ3]});var subQ12=sQuery(id+"F4.wireOp",EDGE,"E936");var subQ13=makeQuery(id+"F4.imprint","INTERSECT",VERTEX,{"derivedFrom":[subQ3,subQ12]});Q35=makeQuery(id+"F4.imprint","IMPRINT",FACE,{"disambiguationData":[TD([[makeQuery(id+"F4.imprint","IMPRINT",EDGE,{"disambiguationData":[TD([[subQ9,-1.0],[subQ13,1.0]])],"derivedFrom":subQ3}),-1.0]])]});}
            var Q36;
            {var subQ0=sQuery(id+"F4.wireOp",EDGE,"E937");var subQ1=makeQuery(id+"F4.imprint","INTERSECT",VERTEX,{"derivedFrom":[sQuery(id+"F4.wireOp",EDGE,"E916.left"),subQ0]});Q36=makeQuery(id+"F4.imprint","IMPRINT",FACE,{"disambiguationData":[TD([[makeQuery(id+"F4.imprint","IMPRINT",EDGE,{"disambiguationData":[TD([[subQ1,1.0]])],"derivedFrom":subQ0}),1.0]])]});}
            var Q37;
            {var subQ0=sQuery(id+"F4.wireOp",EDGE,"E916.top");Q37=makeQuery(id+"F4.imprint","IMPRINT",FACE,{"disambiguationData":[TD([[makeQuery(id+"F4.imprint","IMPRINT",EDGE,{"derivedFrom":subQ0}),1.0]])]});}
            var Q38;
            {var subQ0=sQuery(id+"F4.wireOp",EDGE,"E917.top");Q38=makeQuery(id+"F4.imprint","IMPRINT",FACE,{"disambiguationData":[TD([[makeQuery(id+"F4.imprint","IMPRINT",EDGE,{"derivedFrom":subQ0}),1.0]])]});}
            var Q39;
            {var subQ0=sQuery(id+"F4.wireOp",EDGE,"E942");var subQ1=makeQuery(id+"F4.imprint","INTERSECT",VERTEX,{"derivedFrom":[sQuery(id+"F4.wireOp",EDGE,"E917.left"),subQ0]});Q39=makeQuery(id+"F4.imprint","IMPRINT",FACE,{"disambiguationData":[TD([[makeQuery(id+"F4.imprint","IMPRINT",EDGE,{"disambiguationData":[TD([[subQ1,1.0]])],"derivedFrom":subQ0}),1.0]])]});}
            var Q40;
            {var subQ6=sQuery(id+"F4.wireOp",EDGE,"E917.left");var subQ12=makeQuery(id+"F4.imprint","INTERSECT",VERTEX,{"derivedFrom":[makeQuery(id+"F1.opExtrude","CAP_EDGE",EDGE,{"disambiguationData":[OSD([sQuery(id+"F0.wireOp",EDGE,"E505")])],"isStart":true}),subQ6]});var subQ13=makeQuery(id+"F4.imprint","INTERSECT",VERTEX,{"derivedFrom":[makeQuery(id+"F1.opExtrude","CAP_EDGE",EDGE,{"disambiguationData":[OSD([sQuery(id+"F0.wireOp",EDGE,"E507")])],"isStart":true}),subQ6]});Q40=makeQuery(id+"F4.imprint","IMPRINT",FACE,{"disambiguationData":[TD([[makeQuery(id+"F4.imprint","IMPRINT",EDGE,{"disambiguationData":[TD([[subQ12,-1.0],[subQ13,1.0]])],"derivedFrom":subQ6}),-1.0]])]});}
            var Q41;
            {var subQ0=sQuery(id+"F4.wireOp",EDGE,"E939");var subQ1=makeQuery(id+"F4.imprint","INTERSECT",VERTEX,{"derivedFrom":[sQuery(id+"F4.wireOp",EDGE,"E917.left"),subQ0]});Q41=makeQuery(id+"F4.imprint","IMPRINT",FACE,{"disambiguationData":[TD([[makeQuery(id+"F4.imprint","IMPRINT",EDGE,{"disambiguationData":[TD([[subQ1,1.0]])],"derivedFrom":subQ0}),1.0]])]});}
            var Q42;
            {var subQ0=sQuery(id+"F4.wireOp",EDGE,"E917.left");var subQ6=sQuery(id+"F4.wireOp",EDGE,"E940");var subQ12=makeQuery(id+"F4.imprint","INTERSECT",VERTEX,{"derivedFrom":[makeQuery(id+"F1.opExtrude","CAP_EDGE",EDGE,{"disambiguationData":[OSD([sQuery(id+"F0.wireOp",EDGE,"E547")])],"isStart":true}),subQ0]});var subQ18=makeQuery(id+"F4.imprint","INTERSECT",VERTEX,{"derivedFrom":[subQ0,subQ6]});Q42=makeQuery(id+"F4.imprint","IMPRINT",FACE,{"disambiguationData":[TD([[makeQuery(id+"F4.imprint","IMPRINT",EDGE,{"disambiguationData":[TD([[subQ12,1.0],[subQ18,-1.0]])],"derivedFrom":subQ0}),1.0]])]});}
            var Q43;
            {var subQ0=sQuery(id+"F4.wireOp",EDGE,"E940");var subQ1=makeQuery(id+"F4.imprint","INTERSECT",VERTEX,{"derivedFrom":[sQuery(id+"F4.wireOp",EDGE,"E917.left"),subQ0]});Q43=makeQuery(id+"F4.imprint","IMPRINT",FACE,{"disambiguationData":[TD([[makeQuery(id+"F4.imprint","IMPRINT",EDGE,{"disambiguationData":[TD([[subQ1,1.0]])],"derivedFrom":subQ0}),1.0]])]});}
            var Q44;
            {var subQ6=sQuery(id+"F4.wireOp",EDGE,"E941");var subQ8=sQuery(id+"F4.wireOp",EDGE,"E917.left");var subQ12=makeQuery(id+"F4.imprint","INTERSECT",VERTEX,{"derivedFrom":[makeQuery(id+"F1.opExtrude","CAP_EDGE",EDGE,{"disambiguationData":[OSD([sQuery(id+"F0.wireOp",EDGE,"E583")])],"isStart":true}),subQ8]});var subQ13=makeQuery(id+"F4.imprint","INTERSECT",VERTEX,{"derivedFrom":[subQ8,subQ6]});Q44=makeQuery(id+"F4.imprint","IMPRINT",FACE,{"disambiguationData":[TD([[makeQuery(id+"F4.imprint","IMPRINT",EDGE,{"disambiguationData":[TD([[subQ12,1.0],[subQ13,-1.0]])],"derivedFrom":subQ8}),1.0]])]});}
            var Q45;
            {var subQ0=sQuery(id+"F4.wireOp",EDGE,"E941");var subQ1=makeQuery(id+"F4.imprint","INTERSECT",VERTEX,{"derivedFrom":[sQuery(id+"F4.wireOp",EDGE,"E917.left"),subQ0]});Q45=makeQuery(id+"F4.imprint","IMPRINT",FACE,{"disambiguationData":[TD([[makeQuery(id+"F4.imprint","IMPRINT",EDGE,{"disambiguationData":[TD([[subQ1,1.0]])],"derivedFrom":subQ0}),1.0]])]});}
            var Q46;
            {var subQ3=sQuery(id+"F4.wireOp",EDGE,"E917.bottom");Q46=makeQuery(id+"F4.imprint","IMPRINT",FACE,{"disambiguationData":[TD([[makeQuery(id+"F4.imprint","IMPRINT",EDGE,{"derivedFrom":subQ3}),-1.0]])]});}
            var Q47;
            {var subQ6=sQuery(id+"F4.wireOp",EDGE,"E920.top");Q47=makeQuery(id+"F4.imprint","IMPRINT",FACE,{"disambiguationData":[TD([[makeQuery(id+"F4.imprint","IMPRINT",EDGE,{"derivedFrom":subQ6}),1.0]])]});}
            var Q48;
            {var subQ0=sQuery(id+"F4.wireOp",EDGE,"E943");var subQ1=makeQuery(id+"F4.imprint","INTERSECT",VERTEX,{"derivedFrom":[sQuery(id+"F4.wireOp",EDGE,"E920.left"),subQ0]});Q48=makeQuery(id+"F4.imprint","IMPRINT",FACE,{"disambiguationData":[TD([[makeQuery(id+"F4.imprint","IMPRINT",EDGE,{"disambiguationData":[TD([[subQ1,-1.0]])],"derivedFrom":subQ0}),1.0]])]});}
            var Q49;
            {var subQ5=sQuery(id+"F4.wireOp",EDGE,"E944");var subQ7=sQuery(id+"F4.wireOp",EDGE,"E920.left");var subQ8=makeQuery(id+"F4.imprint","INTERSECT",VERTEX,{"derivedFrom":[subQ7,subQ5]});var subQ9=sQuery(id+"F4.wireOp",EDGE,"E943");var subQ10=makeQuery(id+"F4.imprint","INTERSECT",VERTEX,{"derivedFrom":[subQ7,subQ9]});Q49=makeQuery(id+"F4.imprint","IMPRINT",FACE,{"disambiguationData":[TD([[makeQuery(id+"F4.imprint","IMPRINT",EDGE,{"disambiguationData":[TD([[subQ8,-1.0],[subQ10,1.0]])],"derivedFrom":subQ7}),1.0]])]});}
            var Q50;
            {var subQ0=sQuery(id+"F4.wireOp",EDGE,"E944");var subQ1=makeQuery(id+"F4.imprint","INTERSECT",VERTEX,{"derivedFrom":[sQuery(id+"F4.wireOp",EDGE,"E920.left"),subQ0]});Q50=makeQuery(id+"F4.imprint","IMPRINT",FACE,{"disambiguationData":[TD([[makeQuery(id+"F4.imprint","IMPRINT",EDGE,{"disambiguationData":[TD([[subQ1,-1.0]])],"derivedFrom":subQ0}),1.0]])]});}
            var Q51;
            {var subQ6=sQuery(id+"F4.wireOp",EDGE,"E920.left");var subQ12=makeQuery(id+"F4.imprint","INTERSECT",VERTEX,{"derivedFrom":[makeQuery(id+"F1.opExtrude","CAP_EDGE",EDGE,{"disambiguationData":[OSD([sQuery(id+"F0.wireOp",EDGE,"E737")])],"isStart":true}),subQ6]});var subQ13=sQuery(id+"F4.wireOp",EDGE,"E945");var subQ14=makeQuery(id+"F4.imprint","INTERSECT",VERTEX,{"derivedFrom":[subQ6,subQ13]});Q51=makeQuery(id+"F4.imprint","IMPRINT",FACE,{"disambiguationData":[TD([[makeQuery(id+"F4.imprint","IMPRINT",EDGE,{"disambiguationData":[TD([[subQ12,1.0],[subQ14,-1.0]])],"derivedFrom":subQ6}),1.0]])]});}
            var Q52;
            {var subQ0=sQuery(id+"F4.wireOp",EDGE,"E945");var subQ1=makeQuery(id+"F4.imprint","INTERSECT",VERTEX,{"derivedFrom":[sQuery(id+"F4.wireOp",EDGE,"E920.left"),subQ0]});Q52=makeQuery(id+"F4.imprint","IMPRINT",FACE,{"disambiguationData":[TD([[makeQuery(id+"F4.imprint","IMPRINT",EDGE,{"disambiguationData":[TD([[subQ1,-1.0]])],"derivedFrom":subQ0}),1.0]])]});}
            var Q53;
            {var subQ2=sQuery(id+"F4.wireOp",EDGE,"E946");var subQ4=sQuery(id+"F4.wireOp",EDGE,"E920.left");var subQ9=makeQuery(id+"F4.imprint","INTERSECT",VERTEX,{"derivedFrom":[makeQuery(id+"F1.opExtrude","CAP_EDGE",EDGE,{"disambiguationData":[OSD([sQuery(id+"F0.wireOp",EDGE,"E697")])],"isStart":true}),subQ4]});var subQ10=makeQuery(id+"F4.imprint","INTERSECT",VERTEX,{"derivedFrom":[subQ4,subQ2]});Q53=makeQuery(id+"F4.imprint","IMPRINT",FACE,{"disambiguationData":[TD([[makeQuery(id+"F4.imprint","IMPRINT",EDGE,{"disambiguationData":[TD([[subQ9,1.0],[subQ10,-1.0]])],"derivedFrom":subQ4}),1.0]])]});}
            var Q54;
            {var subQ0=sQuery(id+"F4.wireOp",EDGE,"E946");var subQ1=makeQuery(id+"F4.imprint","INTERSECT",VERTEX,{"derivedFrom":[sQuery(id+"F4.wireOp",EDGE,"E920.left"),subQ0]});Q54=makeQuery(id+"F4.imprint","IMPRINT",FACE,{"disambiguationData":[TD([[makeQuery(id+"F4.imprint","IMPRINT",EDGE,{"disambiguationData":[TD([[subQ1,-1.0]])],"derivedFrom":subQ0}),1.0]])]});}
            var Q55;
            {var subQ0=sQuery(id+"F4.wireOp",EDGE,"E920.bottom");Q55=makeQuery(id+"F4.imprint","IMPRINT",FACE,{"disambiguationData":[TD([[makeQuery(id+"F4.imprint","IMPRINT",EDGE,{"derivedFrom":subQ0}),-1.0]])]});}
            var Q56;
            Q56=makeQuery(id+"F4.imprint","IMPRINT",FACE,{"disambiguationData":[TD([[makeQuery(id+"F4.imprint","IMPRINT",EDGE,{"derivedFrom":sQuery(id+"F4.wireOp",EDGE,"E948")}),1.0]])]});
            var Q57;
            Q57=makeQuery(id+"F4.imprint","IMPRINT",FACE,{"disambiguationData":[TD([[makeQuery(id+"F4.imprint","IMPRINT",EDGE,{"derivedFrom":sQuery(id+"F4.wireOp",EDGE,"E949")}),1.0]])]});
            var Q58;
            Q58=makeQuery(id+"F4.imprint","IMPRINT",FACE,{"disambiguationData":[TD([[makeQuery(id+"F4.imprint","IMPRINT",EDGE,{"derivedFrom":sQuery(id+"F4.wireOp",EDGE,"E950")}),1.0]])]});
            var Q59;
            {var subQ5=sQuery(id+"F4.wireOp",EDGE,"E991.left");Q59=makeQuery(id+"F4.imprint","IMPRINT",FACE,{"disambiguationData":[TD([[makeQuery(id+"F4.imprint","IMPRINT",EDGE,{"derivedFrom":subQ5}),1.0]])]});}
            var Q60;
            {var subQ0=sQuery(id+"F4.wireOp",EDGE,"E991.bottom");var subQ1=sQuery(id+"F4.wireOp",EDGE,"E917.left");var subQ2=makeQuery(id+"F4.imprint","INTERSECT",VERTEX,{"derivedFrom":[subQ1,subQ0]});var subQ3=sQuery(id+"F4.wireOp",EDGE,"E991.top");var subQ4=makeQuery(id+"F4.imprint","INTERSECT",VERTEX,{"derivedFrom":[subQ1,subQ3]});Q60=makeQuery(id+"F4.imprint","IMPRINT",FACE,{"disambiguationData":[TD([[makeQuery(id+"F4.imprint","IMPRINT",EDGE,{"disambiguationData":[TD([[subQ2,-1.0],[subQ4,1.0]])],"derivedFrom":subQ1}),1.0]])]});}
            var Q61;
            {var subQ0=sQuery(id+"F4.wireOp",EDGE,"E991.bottom");var subQ1=sQuery(id+"F4.wireOp",EDGE,"E917.right");var subQ2=makeQuery(id+"F4.imprint","INTERSECT",VERTEX,{"derivedFrom":[subQ1,subQ0]});Q61=makeQuery(id+"F4.imprint","IMPRINT",FACE,{"disambiguationData":[TD([[makeQuery(id+"F4.imprint","IMPRINT",EDGE,{"disambiguationData":[TD([[subQ2,-1.0]])],"derivedFrom":subQ1}),1.0]])]});}
            var Q62;
            {var subQ0=sQuery(id+"F4.wireOp",EDGE,"E991.top");var subQ1=sQuery(id+"F4.wireOp",EDGE,"E945");var subQ2=makeQuery(id+"F4.imprint","INTERSECT",VERTEX,{"disambiguationData":[OD(0.0)],"derivedFrom":[subQ1,subQ0]});Q62=makeQuery(id+"F4.imprint","IMPRINT",FACE,{"disambiguationData":[TD([[makeQuery(id+"F4.imprint","IMPRINT",EDGE,{"disambiguationData":[TD([[subQ2,-1.0]])],"derivedFrom":subQ1}),1.0]])]});}
            var Q63;
            {var subQ0=sQuery(id+"F4.wireOp",EDGE,"E991.right");Q63=makeQuery(id+"F4.imprint","IMPRINT",FACE,{"disambiguationData":[TD([[makeQuery(id+"F4.imprint","IMPRINT",EDGE,{"derivedFrom":subQ0}),-1.0]])]});}
            var Q64;
            {var subQ3=sQuery(id+"F4.wireOp",EDGE,"E991.bottom");var subQ9=sQuery(id+"F4.wireOp",EDGE,"E920.left");var subQ10=makeQuery(id+"F4.imprint","INTERSECT",VERTEX,{"derivedFrom":[makeQuery(id+"F1.opExtrude","CAP_EDGE",EDGE,{"disambiguationData":[OSD([sQuery(id+"F0.wireOp",EDGE,"E737")])],"isStart":true}),subQ9]});var subQ11=makeQuery(id+"F4.imprint","INTERSECT",VERTEX,{"derivedFrom":[subQ9,subQ3]});Q64=makeQuery(id+"F4.imprint","IMPRINT",FACE,{"disambiguationData":[TD([[makeQuery(id+"F4.imprint","IMPRINT",EDGE,{"disambiguationData":[TD([[subQ10,1.0],[subQ11,-1.0]])],"derivedFrom":subQ9}),1.0]])]});}
            var Q65;
            {var subQ0=sQuery(id+"F4.wireOp",EDGE,"E945");var subQ1=sQuery(id+"F4.wireOp",EDGE,"E920.right");var subQ2=makeQuery(id+"F4.imprint","INTERSECT",VERTEX,{"derivedFrom":[subQ1,subQ0]});Q65=makeQuery(id+"F4.imprint","IMPRINT",FACE,{"disambiguationData":[TD([[makeQuery(id+"F4.imprint","IMPRINT",EDGE,{"disambiguationData":[TD([[subQ2,-1.0]])],"derivedFrom":subQ1}),-1.0]])]});}
            var Q66;
            {var subQ0=sQuery(id+"F4.wireOp",EDGE,"E991.bottom");var subQ1=sQuery(id+"F4.wireOp",EDGE,"E945");var subQ2=makeQuery(id+"F4.imprint","INTERSECT",VERTEX,{"disambiguationData":[OD(0.0)],"derivedFrom":[subQ1,subQ0]});Q66=makeQuery(id+"F4.imprint","IMPRINT",FACE,{"disambiguationData":[TD([[makeQuery(id+"F4.imprint","IMPRINT",EDGE,{"disambiguationData":[TD([[subQ2,-1.0]])],"derivedFrom":subQ1}),1.0]])]});}
            var Q67;
            {var subQ0=sQuery(id+"F4.wireOp",EDGE,"E991.top");var subQ1=sQuery(id+"F4.wireOp",EDGE,"E920.right");var subQ2=makeQuery(id+"F4.imprint","INTERSECT",VERTEX,{"derivedFrom":[subQ1,subQ0]});Q67=makeQuery(id+"F4.imprint","IMPRINT",FACE,{"disambiguationData":[TD([[makeQuery(id+"F4.imprint","IMPRINT",EDGE,{"disambiguationData":[TD([[subQ2,-1.0]])],"derivedFrom":subQ1}),-1.0]])]});}
            var Q68;
            {var subQ5=sQuery(id+"F4.wireOp",EDGE,"E917.left");var subQ8=makeQuery(id+"F4.imprint","INTERSECT",VERTEX,{"derivedFrom":[makeQuery(id+"F1.opExtrude","CAP_EDGE",EDGE,{"disambiguationData":[OSD([sQuery(id+"F0.wireOp",EDGE,"E521")])],"isStart":true}),subQ5]});var subQ13=makeQuery(id+"F4.imprint","INTERSECT",VERTEX,{"derivedFrom":[makeQuery(id+"F1.opExtrude","CAP_EDGE",EDGE,{"disambiguationData":[OSD([sQuery(id+"F0.wireOp",EDGE,"E523")])],"isStart":true}),subQ5]});Q68=makeQuery(id+"F4.imprint","IMPRINT",FACE,{"disambiguationData":[TD([[makeQuery(id+"F4.imprint","IMPRINT",EDGE,{"disambiguationData":[TD([[subQ8,-1.0],[subQ13,1.0]])],"derivedFrom":subQ5}),-1.0]])]});}
            var Q69;
            {var subQ3=sQuery(id+"F4.wireOp",EDGE,"E917.left");var subQ7=makeQuery(id+"F4.imprint","INTERSECT",VERTEX,{"derivedFrom":[makeQuery(id+"F1.opExtrude","CAP_EDGE",EDGE,{"disambiguationData":[OSD([sQuery(id+"F0.wireOp",EDGE,"E547")])],"isStart":true}),subQ3]});var subQ8=sQuery(id+"F4.wireOp",EDGE,"E992.top");var subQ9=makeQuery(id+"F4.imprint","INTERSECT",VERTEX,{"derivedFrom":[subQ3,subQ8]});Q69=makeQuery(id+"F4.imprint","IMPRINT",FACE,{"disambiguationData":[TD([[makeQuery(id+"F4.imprint","IMPRINT",EDGE,{"disambiguationData":[TD([[subQ7,1.0],[subQ9,-1.0]])],"derivedFrom":subQ3}),1.0]])]});}
            var Q70;
            {var subQ0=sQuery(id+"F4.wireOp",EDGE,"E992.bottom");var subQ1=sQuery(id+"F4.wireOp",EDGE,"E940");var subQ2=makeQuery(id+"F4.imprint","INTERSECT",VERTEX,{"disambiguationData":[OD(0.0)],"derivedFrom":[subQ1,subQ0]});Q70=makeQuery(id+"F4.imprint","IMPRINT",FACE,{"disambiguationData":[TD([[makeQuery(id+"F4.imprint","IMPRINT",EDGE,{"disambiguationData":[TD([[subQ2,-1.0]])],"derivedFrom":subQ1}),1.0]])]});}
            var Q71;
            {var subQ0=sQuery(id+"F4.wireOp",EDGE,"E992.top");var subQ1=sQuery(id+"F4.wireOp",EDGE,"E940");var subQ2=makeQuery(id+"F4.imprint","INTERSECT",VERTEX,{"disambiguationData":[OD(0.0)],"derivedFrom":[subQ1,subQ0]});Q71=makeQuery(id+"F4.imprint","IMPRINT",FACE,{"disambiguationData":[TD([[makeQuery(id+"F4.imprint","IMPRINT",EDGE,{"disambiguationData":[TD([[subQ2,-1.0]])],"derivedFrom":subQ1}),1.0]])]});}
            var Q72;
            {var subQ0=sQuery(id+"F4.wireOp",EDGE,"E992.bottom");var subQ1=sQuery(id+"F4.wireOp",EDGE,"E917.right");var subQ2=makeQuery(id+"F4.imprint","INTERSECT",VERTEX,{"derivedFrom":[subQ1,subQ0]});Q72=makeQuery(id+"F4.imprint","IMPRINT",FACE,{"disambiguationData":[TD([[makeQuery(id+"F4.imprint","IMPRINT",EDGE,{"disambiguationData":[TD([[subQ2,-1.0]])],"derivedFrom":subQ1}),-1.0]])]});}
            var Q73;
            {var subQ0=sQuery(id+"F4.wireOp",EDGE,"E992.bottom");var subQ1=sQuery(id+"F4.wireOp",EDGE,"E917.left");var subQ2=makeQuery(id+"F4.imprint","INTERSECT",VERTEX,{"derivedFrom":[subQ1,subQ0]});var subQ3=sQuery(id+"F4.wireOp",EDGE,"E940");var subQ4=makeQuery(id+"F4.imprint","INTERSECT",VERTEX,{"derivedFrom":[subQ1,subQ3]});Q73=makeQuery(id+"F4.imprint","IMPRINT",FACE,{"disambiguationData":[TD([[makeQuery(id+"F4.imprint","IMPRINT",EDGE,{"disambiguationData":[TD([[subQ2,-1.0],[subQ4,1.0]])],"derivedFrom":subQ1}),1.0]])]});}
            var Q74;
            {var subQ0=sQuery(id+"F4.wireOp",EDGE,"E940");var subQ1=sQuery(id+"F4.wireOp",EDGE,"E917.right");var subQ2=makeQuery(id+"F4.imprint","INTERSECT",VERTEX,{"derivedFrom":[subQ1,subQ0]});Q74=makeQuery(id+"F4.imprint","IMPRINT",FACE,{"disambiguationData":[TD([[makeQuery(id+"F4.imprint","IMPRINT",EDGE,{"disambiguationData":[TD([[subQ2,-1.0]])],"derivedFrom":subQ1}),-1.0]])]});}
            var Q75;
            {var subQ2=sQuery(id+"F4.wireOp",EDGE,"E944");var subQ5=sQuery(id+"F4.wireOp",EDGE,"E992.bottom");var subQ7=sQuery(id+"F4.wireOp",EDGE,"E920.left");var subQ8=makeQuery(id+"F4.imprint","INTERSECT",VERTEX,{"derivedFrom":[subQ7,subQ5]});var subQ9=makeQuery(id+"F4.imprint","INTERSECT",VERTEX,{"derivedFrom":[subQ7,subQ2]});Q75=makeQuery(id+"F4.imprint","IMPRINT",FACE,{"disambiguationData":[TD([[makeQuery(id+"F4.imprint","IMPRINT",EDGE,{"disambiguationData":[TD([[subQ8,-1.0],[subQ9,1.0]])],"derivedFrom":subQ7}),1.0]])]});}
            var Q76;
            {var subQ0=sQuery(id+"F4.wireOp",EDGE,"E992.top");var subQ1=sQuery(id+"F4.wireOp",EDGE,"E920.left");var subQ2=makeQuery(id+"F4.imprint","INTERSECT",VERTEX,{"derivedFrom":[subQ1,subQ0]});var subQ3=sQuery(id+"F4.wireOp",EDGE,"E992.bottom");var subQ4=makeQuery(id+"F4.imprint","INTERSECT",VERTEX,{"derivedFrom":[subQ1,subQ3]});Q76=makeQuery(id+"F4.imprint","IMPRINT",FACE,{"disambiguationData":[TD([[makeQuery(id+"F4.imprint","IMPRINT",EDGE,{"disambiguationData":[TD([[subQ2,-1.0],[subQ4,1.0]])],"derivedFrom":subQ1}),1.0]])]});}
            var Q77;
            {var subQ0=sQuery(id+"F4.wireOp",EDGE,"E992.bottom");var subQ1=sQuery(id+"F4.wireOp",EDGE,"E917.right");var subQ2=makeQuery(id+"F4.imprint","INTERSECT",VERTEX,{"derivedFrom":[subQ1,subQ0]});Q77=makeQuery(id+"F4.imprint","IMPRINT",FACE,{"disambiguationData":[TD([[makeQuery(id+"F4.imprint","IMPRINT",EDGE,{"disambiguationData":[TD([[subQ2,-1.0]])],"derivedFrom":subQ1}),1.0]])]});}
            var Q78;
            {var subQ0=sQuery(id+"F4.wireOp",EDGE,"E992.left");Q78=makeQuery(id+"F4.imprint","IMPRINT",FACE,{"disambiguationData":[TD([[makeQuery(id+"F4.imprint","IMPRINT",EDGE,{"derivedFrom":subQ0}),1.0]])]});}
            var Q79;
            {var subQ5=sQuery(id+"F4.wireOp",EDGE,"E992.right");Q79=makeQuery(id+"F4.imprint","IMPRINT",FACE,{"disambiguationData":[TD([[makeQuery(id+"F4.imprint","IMPRINT",EDGE,{"derivedFrom":subQ5}),-1.0]])]});}
            var Q80;
            {var subQ0=sQuery(id+"F4.wireOp",EDGE,"E991.top");var subQ1=sQuery(id+"F4.wireOp",EDGE,"E920.left");var subQ2=makeQuery(id+"F4.imprint","INTERSECT",VERTEX,{"derivedFrom":[subQ1,subQ0]});var subQ3=sQuery(id+"F4.wireOp",EDGE,"E945");var subQ4=makeQuery(id+"F4.imprint","INTERSECT",VERTEX,{"derivedFrom":[subQ1,subQ3]});Q80=makeQuery(id+"F4.imprint","IMPRINT",FACE,{"disambiguationData":[TD([[makeQuery(id+"F4.imprint","IMPRINT",EDGE,{"disambiguationData":[TD([[subQ2,-1.0],[subQ4,1.0]])],"derivedFrom":subQ1}),1.0]])]});}
            var Q81;
            {var subQ4=sQuery(id+"F4.wireOp",EDGE,"E999.bottom");Q81=makeQuery(id+"F4.imprint","IMPRINT",FACE,{"disambiguationData":[TD([[makeQuery(id+"F4.imprint","IMPRINT",EDGE,{"derivedFrom":subQ4}),-1.0]])]});}
            var Q82;
            {var subQ1=sQuery(id+"F4.wireOp",EDGE,"E1002.bottom");Q82=makeQuery(id+"F4.imprint","IMPRINT",FACE,{"disambiguationData":[TD([[makeQuery(id+"F4.imprint","IMPRINT",EDGE,{"derivedFrom":subQ1}),-1.0]])]});}
            var Q83;
            Q83=makeQuery(id+"F4.imprint","IMPRINT",FACE,{"disambiguationData":[TD([[makeQuery(id+"F4.imprint","IMPRINT",EDGE,{"derivedFrom":sQuery(id+"F4.wireOp",EDGE,"E1001.bottom")}),-1.0]])]});
            var Q84;
            Q84=makeQuery(id+"F4.imprint","IMPRINT",FACE,{"disambiguationData":[TD([[makeQuery(id+"F4.imprint","IMPRINT",EDGE,{"derivedFrom":sQuery(id+"F4.wireOp",EDGE,"E1000.bottom")}),-1.0]])]});
            var Q85;
            Q85=makeQuery(id+"F4.imprint","IMPRINT",FACE,{"disambiguationData":[TD([[makeQuery(id+"F4.imprint","IMPRINT",EDGE,{"derivedFrom":sQuery(id+"F4.wireOp",EDGE,"E998.bottom")}),-1.0]])]});
            var Q86;
            Q86=makeQuery(id+"F4.imprint","IMPRINT",FACE,{"disambiguationData":[TD([[makeQuery(id+"F4.imprint","IMPRINT",EDGE,{"derivedFrom":sQuery(id+"F4.wireOp",EDGE,"E1003.bottom")}),-1.0]])]});
            var Q87;
            Q87=makeQuery(id+"F4.imprint","IMPRINT",FACE,{"disambiguationData":[TD([[makeQuery(id+"F4.imprint","IMPRINT",EDGE,{"derivedFrom":sQuery(id+"F4.wireOp",EDGE,"E1004.bottom")}),-1.0]])]});
            extrude(context, id + "F5", {"entities" : qUnion([Q0, Q1, Q2, Q3, Q4, Q5, Q6, Q7, Q8, Q9, Q10, Q11, Q12, Q13, Q14, Q15, Q16, Q17, Q18, Q19, Q20, Q21, Q22, Q23, Q24, Q25, Q26, Q27, Q28, Q29, Q30, Q31, Q32, Q33, Q34, Q35, Q36, Q37, Q38, Q39, Q40, Q41, Q42, Q43, Q44, Q45, Q46, Q47, Q48, Q49, Q50, Q51, Q52, Q53, Q54, Q55, Q56, Q57, Q58, Q59, Q60, Q61, Q62, Q63, Q64, Q65, Q66, Q67, Q68, Q69, Q70, Q71, Q72, Q73, Q74, Q75, Q76, Q77, Q78, Q79, Q80, Q81, Q82, Q83, Q84, Q85, Q86, Q87]), "operationType" : NewBodyOperationType.ADD, "depth" : 3 * mm});
        }
        {
            var Q0;
            Q0=makeQuery(id+"F4.imprint","IMPRINT",FACE,{"disambiguationData":[TD([[makeQuery(id+"F4.imprint","IMPRINT",EDGE,{"derivedFrom":sQuery(id+"F4.wireOp",EDGE,"E951")}),-1.0]])]});
            var Q1;
            Q1=makeQuery(id+"F4.imprint","IMPRINT",FACE,{"disambiguationData":[TD([[makeQuery(id+"F4.imprint","IMPRINT",EDGE,{"derivedFrom":sQuery(id+"F4.wireOp",EDGE,"E952")}),-1.0]])]});
            var Q2;
            Q2=makeQuery(id+"F4.imprint","IMPRINT",FACE,{"disambiguationData":[TD([[makeQuery(id+"F4.imprint","IMPRINT",EDGE,{"derivedFrom":sQuery(id+"F4.wireOp",EDGE,"E957")}),-1.0]])]});
            var Q3;
            Q3=makeQuery(id+"F4.imprint","IMPRINT",FACE,{"disambiguationData":[TD([[makeQuery(id+"F4.imprint","IMPRINT",EDGE,{"derivedFrom":sQuery(id+"F4.wireOp",EDGE,"E962")}),-1.0]])]});
            var Q4;
            Q4=makeQuery(id+"F4.imprint","IMPRINT",FACE,{"disambiguationData":[TD([[makeQuery(id+"F4.imprint","IMPRINT",EDGE,{"derivedFrom":sQuery(id+"F4.wireOp",EDGE,"E953")}),-1.0]])]});
            var Q5;
            Q5=makeQuery(id+"F4.imprint","IMPRINT",FACE,{"disambiguationData":[TD([[makeQuery(id+"F4.imprint","IMPRINT",EDGE,{"derivedFrom":sQuery(id+"F4.wireOp",EDGE,"E958")}),-1.0]])]});
            var Q6;
            Q6=makeQuery(id+"F4.imprint","IMPRINT",FACE,{"disambiguationData":[TD([[makeQuery(id+"F4.imprint","IMPRINT",EDGE,{"derivedFrom":sQuery(id+"F4.wireOp",EDGE,"E956")}),-1.0]])]});
            var Q7;
            Q7=makeQuery(id+"F4.imprint","IMPRINT",FACE,{"disambiguationData":[TD([[makeQuery(id+"F4.imprint","IMPRINT",EDGE,{"derivedFrom":sQuery(id+"F4.wireOp",EDGE,"E963")}),-1.0]])]});
            var Q8;
            Q8=makeQuery(id+"F4.imprint","IMPRINT",FACE,{"disambiguationData":[TD([[makeQuery(id+"F4.imprint","IMPRINT",EDGE,{"derivedFrom":sQuery(id+"F4.wireOp",EDGE,"E965")}),-1.0]])]});
            var Q9;
            Q9=makeQuery(id+"F4.imprint","IMPRINT",FACE,{"disambiguationData":[TD([[makeQuery(id+"F4.imprint","IMPRINT",EDGE,{"derivedFrom":sQuery(id+"F4.wireOp",EDGE,"E974")}),-1.0]])]});
            var Q10;
            Q10=makeQuery(id+"F4.imprint","IMPRINT",FACE,{"disambiguationData":[TD([[makeQuery(id+"F4.imprint","IMPRINT",EDGE,{"derivedFrom":sQuery(id+"F4.wireOp",EDGE,"E972")}),-1.0]])]});
            var Q11;
            Q11=makeQuery(id+"F4.imprint","IMPRINT",FACE,{"disambiguationData":[TD([[makeQuery(id+"F4.imprint","IMPRINT",EDGE,{"derivedFrom":sQuery(id+"F4.wireOp",EDGE,"E973")}),-1.0]])]});
            var Q12;
            Q12=makeQuery(id+"F4.imprint","IMPRINT",FACE,{"disambiguationData":[TD([[makeQuery(id+"F4.imprint","IMPRINT",EDGE,{"derivedFrom":sQuery(id+"F4.wireOp",EDGE,"E975")}),-1.0]])]});
            var Q13;
            Q13=makeQuery(id+"F4.imprint","IMPRINT",FACE,{"disambiguationData":[TD([[makeQuery(id+"F4.imprint","IMPRINT",EDGE,{"derivedFrom":sQuery(id+"F4.wireOp",EDGE,"E954")}),-1.0]])]});
            var Q14;
            Q14=makeQuery(id+"F4.imprint","IMPRINT",FACE,{"disambiguationData":[TD([[makeQuery(id+"F4.imprint","IMPRINT",EDGE,{"derivedFrom":sQuery(id+"F4.wireOp",EDGE,"E961")}),-1.0]])]});
            var Q15;
            Q15=makeQuery(id+"F4.imprint","IMPRINT",FACE,{"disambiguationData":[TD([[makeQuery(id+"F4.imprint","IMPRINT",EDGE,{"derivedFrom":sQuery(id+"F4.wireOp",EDGE,"E955")}),-1.0]])]});
            var Q16;
            Q16=makeQuery(id+"F4.imprint","IMPRINT",FACE,{"disambiguationData":[TD([[makeQuery(id+"F4.imprint","IMPRINT",EDGE,{"derivedFrom":sQuery(id+"F4.wireOp",EDGE,"E959")}),-1.0]])]});
            var Q17;
            Q17=makeQuery(id+"F4.imprint","IMPRINT",FACE,{"disambiguationData":[TD([[makeQuery(id+"F4.imprint","IMPRINT",EDGE,{"derivedFrom":sQuery(id+"F4.wireOp",EDGE,"E960")}),-1.0]])]});
            var Q18;
            Q18=makeQuery(id+"F4.imprint","IMPRINT",FACE,{"disambiguationData":[TD([[makeQuery(id+"F4.imprint","IMPRINT",EDGE,{"derivedFrom":sQuery(id+"F4.wireOp",EDGE,"E967")}),-1.0]])]});
            var Q19;
            Q19=makeQuery(id+"F4.imprint","IMPRINT",FACE,{"disambiguationData":[TD([[makeQuery(id+"F4.imprint","IMPRINT",EDGE,{"derivedFrom":sQuery(id+"F4.wireOp",EDGE,"E966")}),-1.0]])]});
            var Q20;
            Q20=makeQuery(id+"F4.imprint","IMPRINT",FACE,{"disambiguationData":[TD([[makeQuery(id+"F4.imprint","IMPRINT",EDGE,{"derivedFrom":sQuery(id+"F4.wireOp",EDGE,"E969")}),-1.0]])]});
            var Q21;
            Q21=makeQuery(id+"F4.imprint","IMPRINT",FACE,{"disambiguationData":[TD([[makeQuery(id+"F4.imprint","IMPRINT",EDGE,{"derivedFrom":sQuery(id+"F4.wireOp",EDGE,"E968")}),-1.0]])]});
            var Q22;
            Q22=makeQuery(id+"F4.imprint","IMPRINT",FACE,{"disambiguationData":[TD([[makeQuery(id+"F4.imprint","IMPRINT",EDGE,{"derivedFrom":sQuery(id+"F4.wireOp",EDGE,"E970")}),-1.0]])]});
            var Q23;
            Q23=makeQuery(id+"F4.imprint","IMPRINT",FACE,{"disambiguationData":[TD([[makeQuery(id+"F4.imprint","IMPRINT",EDGE,{"derivedFrom":sQuery(id+"F4.wireOp",EDGE,"E971")}),-1.0]])]});
            var Q24;
            Q24=makeQuery(id+"F4.imprint","IMPRINT",FACE,{"disambiguationData":[TD([[makeQuery(id+"F4.imprint","IMPRINT",EDGE,{"derivedFrom":sQuery(id+"F4.wireOp",EDGE,"E948")}),1.0]])]});
            var Q25;
            Q25=makeQuery(id+"F4.imprint","IMPRINT",FACE,{"disambiguationData":[TD([[makeQuery(id+"F4.imprint","IMPRINT",EDGE,{"derivedFrom":sQuery(id+"F4.wireOp",EDGE,"E949")}),1.0]])]});
            var Q26;
            Q26=makeQuery(id+"F4.imprint","IMPRINT",FACE,{"disambiguationData":[TD([[makeQuery(id+"F4.imprint","IMPRINT",EDGE,{"derivedFrom":sQuery(id+"F4.wireOp",EDGE,"E950")}),1.0]])]});
            var Q27;
            Q27=makeQuery(id+"F4.imprint","IMPRINT",FACE,{"disambiguationData":[TD([[makeQuery(id+"F4.imprint","IMPRINT",EDGE,{"derivedFrom":sQuery(id+"F4.wireOp",EDGE,"E964")}),-1.0]])]});
            var Q28;
            Q28=makeQuery(id+"F4.imprint","IMPRINT",FACE,{"disambiguationData":[TD([[makeQuery(id+"F4.imprint","IMPRINT",EDGE,{"derivedFrom":sQuery(id+"F4.wireOp",EDGE,"E982")}),1.0]])]});
            var Q29;
            Q29=makeQuery(id+"F4.imprint","IMPRINT",FACE,{"disambiguationData":[TD([[makeQuery(id+"F4.imprint","IMPRINT",EDGE,{"derivedFrom":sQuery(id+"F4.wireOp",EDGE,"E984")}),1.0]])]});
            var Q30;
            Q30=makeQuery(id+"F4.imprint","IMPRINT",FACE,{"disambiguationData":[TD([[makeQuery(id+"F4.imprint","IMPRINT",EDGE,{"derivedFrom":sQuery(id+"F4.wireOp",EDGE,"E986")}),1.0]])]});
            var Q31;
            Q31=makeQuery(id+"F4.imprint","IMPRINT",FACE,{"disambiguationData":[TD([[makeQuery(id+"F4.imprint","IMPRINT",EDGE,{"derivedFrom":sQuery(id+"F4.wireOp",EDGE,"E988")}),1.0]])]});
            var Q32;
            Q32=makeQuery(id+"F4.imprint","IMPRINT",FACE,{"disambiguationData":[TD([[makeQuery(id+"F4.imprint","IMPRINT",EDGE,{"derivedFrom":sQuery(id+"F4.wireOp",EDGE,"E993")}),1.0]])]});
            var Q33;
            Q33=makeQuery(id+"F4.imprint","IMPRINT",FACE,{"disambiguationData":[TD([[makeQuery(id+"F4.imprint","IMPRINT",EDGE,{"derivedFrom":sQuery(id+"F4.wireOp",EDGE,"E996")}),1.0]])]});
            extrude(context, id + "F6", {"entities" : qUnion([Q0, Q1, Q2, Q3, Q4, Q5, Q6, Q7, Q8, Q9, Q10, Q11, Q12, Q13, Q14, Q15, Q16, Q17, Q18, Q19, Q20, Q21, Q22, Q23, Q24, Q25, Q26, Q27, Q28, Q29, Q30, Q31, Q32, Q33]), "operationType" : NewBodyOperationType.ADD, "depth" : 12 * mm});
        }
    });
